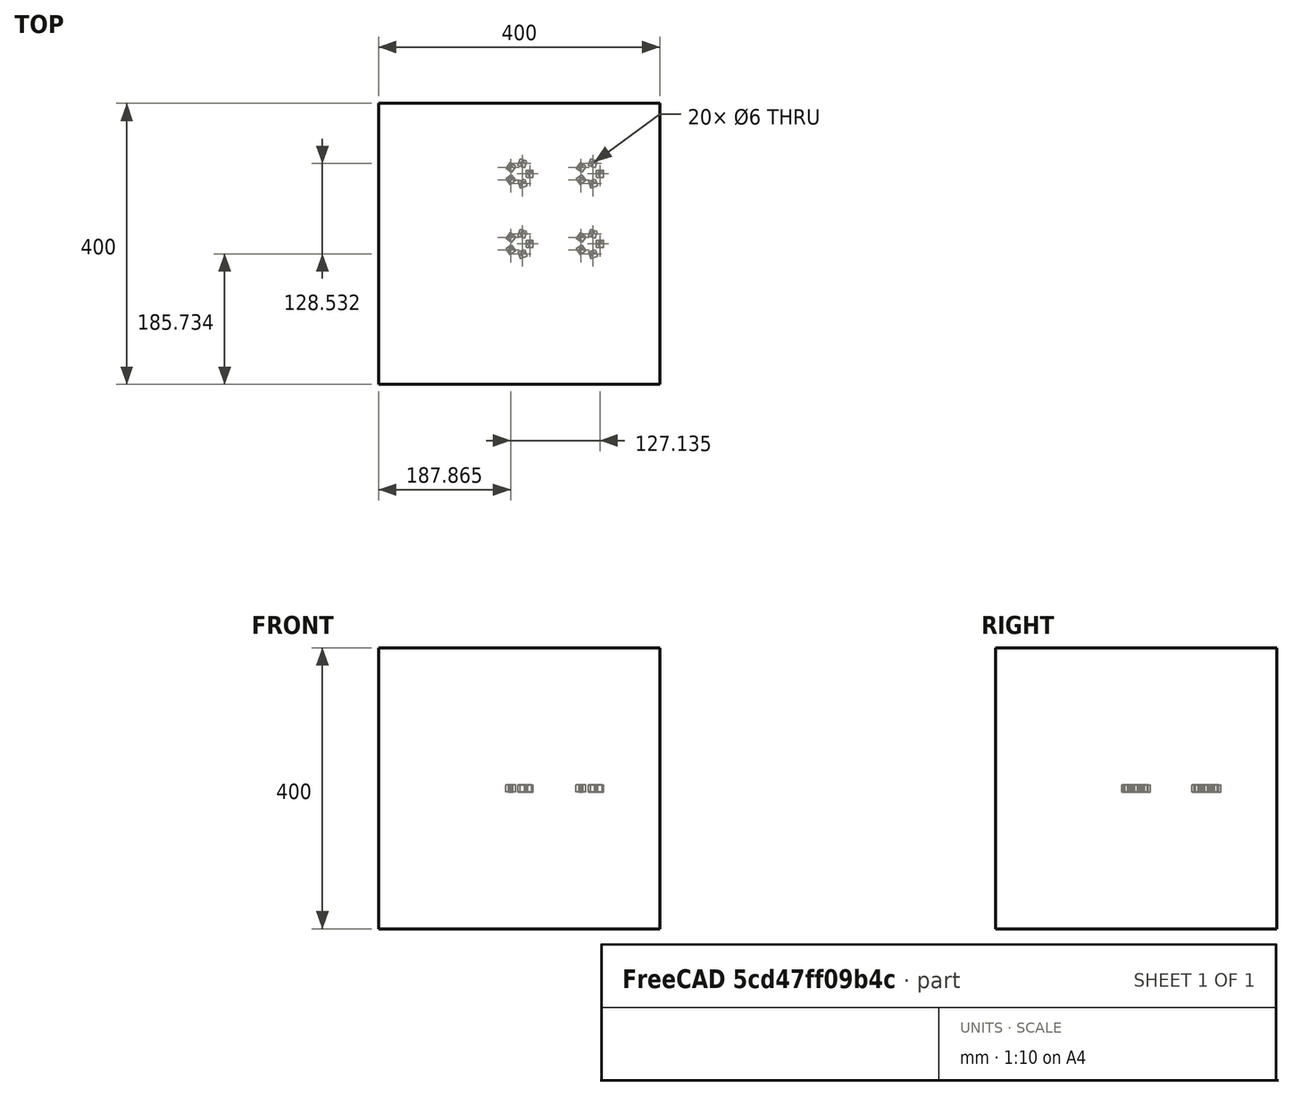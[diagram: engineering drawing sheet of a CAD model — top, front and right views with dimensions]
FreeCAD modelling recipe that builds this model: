
FCSTD DOCUMENT  (FreeCAD 0.19RUnknown)
Label: orthoArray_of_polarArray
License: All rights reserved
LicenseURL: http://en.wikipedia.org/wiki/All_rights_reserved
objects: App::DocumentObjectGroupPython×1248, Part::FeaturePython×5, App::Part×2, Part::Cut×1
note: 6 computed .brp shape members not serialized (recipe doc carries the construction recipe); baked Part::Feature solids carry a one-line shape summary decoded from their .brp

FEATURE [App::DocumentObjectGroupPython] HALFPI  # scripted group (container) (typed FeaturePython)
  name = HALFPI
  value = pi/2.
FEATURE [App::DocumentObjectGroupPython] PI  # scripted group (container) (typed FeaturePython)
  name = PI
  value = 1.*pi
FEATURE [App::DocumentObjectGroupPython] TWOPI  # scripted group (container) (typed FeaturePython)
  name = TWOPI
  value = 2.*pi
FEATURE [App::DocumentObjectGroupPython] Constants  # scripted group (container) (typed FeaturePython)
  Group = -> [HALFPI,PI,TWOPI]
FEATURE [App::DocumentObjectGroupPython] Variables  # scripted group (container) (typed FeaturePython)
FEATURE [App::DocumentObjectGroupPython] Quantities  # scripted group (container) (typed FeaturePython)
FEATURE [App::DocumentObjectGroupPython] Isotopes  # scripted group (container) (typed FeaturePython)
FEATURE [App::DocumentObjectGroupPython] Elements  # scripted group (container) (typed FeaturePython)
FEATURE [App::DocumentObjectGroupPython] G4Isotopes  # scripted group (container) (typed FeaturePython)
FEATURE [App::DocumentObjectGroupPython] H_element  # scripted group (container) (typed FeaturePython)
  Z = 1
  atom_value = 1.008
  formula = H
  name = H_element
FEATURE [App::DocumentObjectGroupPython] He_element  # scripted group (container) (typed FeaturePython)
  Z = 2
  atom_value = 4.0026
  formula = He
  name = He_element
FEATURE [App::DocumentObjectGroupPython] Li_element  # scripted group (container) (typed FeaturePython)
  Z = 3
  atom_value = 6.94
  formula = Li
  name = Li_element
FEATURE [App::DocumentObjectGroupPython] Be_element  # scripted group (container) (typed FeaturePython)
  Z = 4
  atom_value = 9.01218
  formula = Be
  name = Be_element
FEATURE [App::DocumentObjectGroupPython] B_element  # scripted group (container) (typed FeaturePython)
  Z = 5
  atom_value = 10.81
  formula = B
  name = B_element
FEATURE [App::DocumentObjectGroupPython] C_element  # scripted group (container) (typed FeaturePython)
  Z = 6
  atom_value = 12.011
  formula = C
  name = C_element
FEATURE [App::DocumentObjectGroupPython] N_element  # scripted group (container) (typed FeaturePython)
  Z = 7
  atom_value = 14.007
  formula = N
  name = N_element
FEATURE [App::DocumentObjectGroupPython] O_element  # scripted group (container) (typed FeaturePython)
  Z = 8
  atom_value = 15.999
  formula = O
  name = O_element
FEATURE [App::DocumentObjectGroupPython] F_element  # scripted group (container) (typed FeaturePython)
  Z = 9
  atom_value = 18.9984
  formula = F
  name = F_element
FEATURE [App::DocumentObjectGroupPython] Ne_element  # scripted group (container) (typed FeaturePython)
  Z = 10
  atom_value = 20.1797
  formula = Ne
  name = Ne_element
FEATURE [App::DocumentObjectGroupPython] Na_element  # scripted group (container) (typed FeaturePython)
  Z = 11
  atom_value = 22.9898
  formula = Na
  name = Na_element
FEATURE [App::DocumentObjectGroupPython] Mg_element  # scripted group (container) (typed FeaturePython)
  Z = 12
  atom_value = 24.305
  formula = Mg
  name = Mg_element
FEATURE [App::DocumentObjectGroupPython] Al_element  # scripted group (container) (typed FeaturePython)
  Z = 13
  atom_value = 26.9815
  formula = Al
  name = Al_element
FEATURE [App::DocumentObjectGroupPython] Si_element  # scripted group (container) (typed FeaturePython)
  Z = 14
  atom_value = 28.085
  formula = Si
  name = Si_element
FEATURE [App::DocumentObjectGroupPython] P_element  # scripted group (container) (typed FeaturePython)
  Z = 15
  atom_value = 30.9738
  formula = P
  name = P_element
FEATURE [App::DocumentObjectGroupPython] S_element  # scripted group (container) (typed FeaturePython)
  Z = 16
  atom_value = 32.06
  formula = S
  name = S_element
FEATURE [App::DocumentObjectGroupPython] Cl_element  # scripted group (container) (typed FeaturePython)
  Z = 17
  atom_value = 35.45
  formula = Cl
  name = Cl_element
FEATURE [App::DocumentObjectGroupPython] Ar_element  # scripted group (container) (typed FeaturePython)
  Z = 18
  atom_value = 39.95
  formula = Ar
  name = Ar_element
FEATURE [App::DocumentObjectGroupPython] K_element  # scripted group (container) (typed FeaturePython)
  Z = 19
  atom_value = 39.0983
  formula = K
  name = K_element
FEATURE [App::DocumentObjectGroupPython] Ca_element  # scripted group (container) (typed FeaturePython)
  Z = 20
  atom_value = 40.078
  formula = Ca
  name = Ca_element
FEATURE [App::DocumentObjectGroupPython] Sc_element  # scripted group (container) (typed FeaturePython)
  Z = 21
  atom_value = 44.9559
  formula = Sc
  name = Sc_element
FEATURE [App::DocumentObjectGroupPython] Ti_element  # scripted group (container) (typed FeaturePython)
  Z = 22
  atom_value = 47.867
  formula = Ti
  name = Ti_element
FEATURE [App::DocumentObjectGroupPython] V_element  # scripted group (container) (typed FeaturePython)
  Z = 23
  atom_value = 50.9415
  formula = V
  name = V_element
FEATURE [App::DocumentObjectGroupPython] Cr_element  # scripted group (container) (typed FeaturePython)
  Z = 24
  atom_value = 51.9961
  formula = Cr
  name = Cr_element
FEATURE [App::DocumentObjectGroupPython] Mn_element  # scripted group (container) (typed FeaturePython)
  Z = 25
  atom_value = 54.938
  formula = Mn
  name = Mn_element
FEATURE [App::DocumentObjectGroupPython] Fe_element  # scripted group (container) (typed FeaturePython)
  Z = 26
  atom_value = 55.845
  formula = Fe
  name = Fe_element
FEATURE [App::DocumentObjectGroupPython] Co_element  # scripted group (container) (typed FeaturePython)
  Z = 27
  atom_value = 58.9332
  formula = Co
  name = Co_element
FEATURE [App::DocumentObjectGroupPython] Ni_element  # scripted group (container) (typed FeaturePython)
  Z = 28
  atom_value = 58.6934
  formula = Ni
  name = Ni_element
FEATURE [App::DocumentObjectGroupPython] Cu_element  # scripted group (container) (typed FeaturePython)
  Z = 29
  atom_value = 63.546
  formula = Cu
  name = Cu_element
FEATURE [App::DocumentObjectGroupPython] Zn_element  # scripted group (container) (typed FeaturePython)
  Z = 30
  atom_value = 65.38
  formula = Zn
  name = Zn_element
FEATURE [App::DocumentObjectGroupPython] Ga_element  # scripted group (container) (typed FeaturePython)
  Z = 31
  atom_value = 69.723
  formula = Ga
  name = Ga_element
FEATURE [App::DocumentObjectGroupPython] Ge_element  # scripted group (container) (typed FeaturePython)
  Z = 32
  atom_value = 72.63
  formula = Ge
  name = Ge_element
FEATURE [App::DocumentObjectGroupPython] As_element  # scripted group (container) (typed FeaturePython)
  Z = 33
  atom_value = 74.9216
  formula = As
  name = As_element
FEATURE [App::DocumentObjectGroupPython] Se_element  # scripted group (container) (typed FeaturePython)
  Z = 34
  atom_value = 78.971
  formula = Se
  name = Se_element
FEATURE [App::DocumentObjectGroupPython] Br_element  # scripted group (container) (typed FeaturePython)
  Z = 35
  atom_value = 79.904
  formula = Br
  name = Br_element
FEATURE [App::DocumentObjectGroupPython] Kr_element  # scripted group (container) (typed FeaturePython)
  Z = 36
  atom_value = 83.798
  formula = Kr
  name = Kr_element
FEATURE [App::DocumentObjectGroupPython] Rb_element  # scripted group (container) (typed FeaturePython)
  Z = 37
  atom_value = 85.4678
  formula = Rb
  name = Rb_element
FEATURE [App::DocumentObjectGroupPython] Sr_element  # scripted group (container) (typed FeaturePython)
  Z = 38
  atom_value = 87.62
  formula = Sr
  name = Sr_element
FEATURE [App::DocumentObjectGroupPython] Y_element  # scripted group (container) (typed FeaturePython)
  Z = 39
  atom_value = 88.9058
  formula = Y
  name = Y_element
FEATURE [App::DocumentObjectGroupPython] Zr_element  # scripted group (container) (typed FeaturePython)
  Z = 40
  atom_value = 91.224
  formula = Zr
  name = Zr_element
FEATURE [App::DocumentObjectGroupPython] Nb_element  # scripted group (container) (typed FeaturePython)
  Z = 41
  atom_value = 92.9064
  formula = Nb
  name = Nb_element
FEATURE [App::DocumentObjectGroupPython] Mo_element  # scripted group (container) (typed FeaturePython)
  Z = 42
  atom_value = 95.95
  formula = Mo
  name = Mo_element
FEATURE [App::DocumentObjectGroupPython] Tc_element  # scripted group (container) (typed FeaturePython)
  Z = 43
  atom_value = 97
  formula = Tc
  name = Tc_element
FEATURE [App::DocumentObjectGroupPython] Ru_element  # scripted group (container) (typed FeaturePython)
  Z = 44
  atom_value = 101.07
  formula = Ru
  name = Ru_element
FEATURE [App::DocumentObjectGroupPython] Rh_element  # scripted group (container) (typed FeaturePython)
  Z = 45
  atom_value = 102.905
  formula = Rh
  name = Rh_element
FEATURE [App::DocumentObjectGroupPython] Pd_element  # scripted group (container) (typed FeaturePython)
  Z = 46
  atom_value = 106.42
  formula = Pd
  name = Pd_element
FEATURE [App::DocumentObjectGroupPython] Ag_element  # scripted group (container) (typed FeaturePython)
  Z = 47
  atom_value = 107.868
  formula = Ag
  name = Ag_element
FEATURE [App::DocumentObjectGroupPython] Cd_element  # scripted group (container) (typed FeaturePython)
  Z = 48
  atom_value = 112.414
  formula = Cd
  name = Cd_element
FEATURE [App::DocumentObjectGroupPython] In_element  # scripted group (container) (typed FeaturePython)
  Z = 49
  atom_value = 114.818
  formula = In
  name = In_element
FEATURE [App::DocumentObjectGroupPython] Sn_element  # scripted group (container) (typed FeaturePython)
  Z = 50
  atom_value = 118.71
  formula = Sn
  name = Sn_element
FEATURE [App::DocumentObjectGroupPython] Sb_element  # scripted group (container) (typed FeaturePython)
  Z = 51
  atom_value = 121.76
  formula = Sb
  name = Sb_element
FEATURE [App::DocumentObjectGroupPython] Te_element  # scripted group (container) (typed FeaturePython)
  Z = 52
  atom_value = 127.6
  formula = Te
  name = Te_element
FEATURE [App::DocumentObjectGroupPython] I_element  # scripted group (container) (typed FeaturePython)
  Z = 53
  atom_value = 126.904
  formula = I
  name = I_element
FEATURE [App::DocumentObjectGroupPython] Xe_element  # scripted group (container) (typed FeaturePython)
  Z = 54
  atom_value = 131.293
  formula = Xe
  name = Xe_element
FEATURE [App::DocumentObjectGroupPython] Cs_element  # scripted group (container) (typed FeaturePython)
  Z = 55
  atom_value = 132.905
  formula = Cs
  name = Cs_element
FEATURE [App::DocumentObjectGroupPython] Ba_element  # scripted group (container) (typed FeaturePython)
  Z = 56
  atom_value = 137.327
  formula = Ba
  name = Ba_element
FEATURE [App::DocumentObjectGroupPython] La_element  # scripted group (container) (typed FeaturePython)
  Z = 57
  atom_value = 138.905
  formula = La
  name = La_element
FEATURE [App::DocumentObjectGroupPython] Ce_element  # scripted group (container) (typed FeaturePython)
  Z = 58
  atom_value = 140.116
  formula = Ce
  name = Ce_element
FEATURE [App::DocumentObjectGroupPython] Pr_element  # scripted group (container) (typed FeaturePython)
  Z = 59
  atom_value = 140.908
  formula = Pr
  name = Pr_element
FEATURE [App::DocumentObjectGroupPython] Nd_element  # scripted group (container) (typed FeaturePython)
  Z = 60
  atom_value = 144.242
  formula = Nd
  name = Nd_element
FEATURE [App::DocumentObjectGroupPython] Pm_element  # scripted group (container) (typed FeaturePython)
  Z = 61
  atom_value = 145
  formula = Pm
  name = Pm_element
FEATURE [App::DocumentObjectGroupPython] Sm_element  # scripted group (container) (typed FeaturePython)
  Z = 62
  atom_value = 150.36
  formula = Sm
  name = Sm_element
FEATURE [App::DocumentObjectGroupPython] Eu_element  # scripted group (container) (typed FeaturePython)
  Z = 63
  atom_value = 151.964
  formula = Eu
  name = Eu_element
FEATURE [App::DocumentObjectGroupPython] Gd_element  # scripted group (container) (typed FeaturePython)
  Z = 64
  atom_value = 157.25
  formula = Gd
  name = Gd_element
FEATURE [App::DocumentObjectGroupPython] Tb_element  # scripted group (container) (typed FeaturePython)
  Z = 65
  atom_value = 158.925
  formula = Tb
  name = Tb_element
FEATURE [App::DocumentObjectGroupPython] Dy_element  # scripted group (container) (typed FeaturePython)
  Z = 66
  atom_value = 162.5
  formula = Dy
  name = Dy_element
FEATURE [App::DocumentObjectGroupPython] Ho_element  # scripted group (container) (typed FeaturePython)
  Z = 67
  atom_value = 164.93
  formula = Ho
  name = Ho_element
FEATURE [App::DocumentObjectGroupPython] Er_element  # scripted group (container) (typed FeaturePython)
  Z = 68
  atom_value = 167.259
  formula = Er
  name = Er_element
FEATURE [App::DocumentObjectGroupPython] Tm_element  # scripted group (container) (typed FeaturePython)
  Z = 69
  atom_value = 168.934
  formula = Tm
  name = Tm_element
FEATURE [App::DocumentObjectGroupPython] Yb_element  # scripted group (container) (typed FeaturePython)
  Z = 70
  atom_value = 173.045
  formula = Yb
  name = Yb_element
FEATURE [App::DocumentObjectGroupPython] Lu_element  # scripted group (container) (typed FeaturePython)
  Z = 71
  atom_value = 174.967
  formula = Lu
  name = Lu_element
FEATURE [App::DocumentObjectGroupPython] Hf_element  # scripted group (container) (typed FeaturePython)
  Z = 72
  atom_value = 178.49
  formula = Hf
  name = Hf_element
FEATURE [App::DocumentObjectGroupPython] Ta_element  # scripted group (container) (typed FeaturePython)
  Z = 73
  atom_value = 180.948
  formula = Ta
  name = Ta_element
FEATURE [App::DocumentObjectGroupPython] W_element  # scripted group (container) (typed FeaturePython)
  Z = 74
  atom_value = 183.84
  formula = W
  name = W_element
FEATURE [App::DocumentObjectGroupPython] Re_element  # scripted group (container) (typed FeaturePython)
  Z = 75
  atom_value = 186.207
  formula = Re
  name = Re_element
FEATURE [App::DocumentObjectGroupPython] Os_element  # scripted group (container) (typed FeaturePython)
  Z = 76
  atom_value = 190.23
  formula = Os
  name = Os_element
FEATURE [App::DocumentObjectGroupPython] Ir_element  # scripted group (container) (typed FeaturePython)
  Z = 77
  atom_value = 192.217
  formula = Ir
  name = Ir_element
FEATURE [App::DocumentObjectGroupPython] Pt_element  # scripted group (container) (typed FeaturePython)
  Z = 78
  atom_value = 195.084
  formula = Pt
  name = Pt_element
FEATURE [App::DocumentObjectGroupPython] Au_element  # scripted group (container) (typed FeaturePython)
  Z = 79
  atom_value = 196.967
  formula = Au
  name = Au_element
FEATURE [App::DocumentObjectGroupPython] Hg_element  # scripted group (container) (typed FeaturePython)
  Z = 80
  atom_value = 200.592
  formula = Hg
  name = Hg_element
FEATURE [App::DocumentObjectGroupPython] Tl_element  # scripted group (container) (typed FeaturePython)
  Z = 81
  atom_value = 204.38
  formula = Tl
  name = Tl_element
FEATURE [App::DocumentObjectGroupPython] Pb_element  # scripted group (container) (typed FeaturePython)
  Z = 82
  atom_value = 207.2
  formula = Pb
  name = Pb_element
FEATURE [App::DocumentObjectGroupPython] Bi_element  # scripted group (container) (typed FeaturePython)
  Z = 83
  atom_value = 208.98
  formula = Bi
  name = Bi_element
FEATURE [App::DocumentObjectGroupPython] Po_element  # scripted group (container) (typed FeaturePython)
  Z = 84
  atom_value = 209
  formula = Po
  name = Po_element
FEATURE [App::DocumentObjectGroupPython] At_element  # scripted group (container) (typed FeaturePython)
  Z = 85
  atom_value = 210
  formula = At
  name = At_element
FEATURE [App::DocumentObjectGroupPython] Rn_element  # scripted group (container) (typed FeaturePython)
  Z = 86
  atom_value = 222
  formula = Rn
  name = Rn_element
FEATURE [App::DocumentObjectGroupPython] Fr_element  # scripted group (container) (typed FeaturePython)
  Z = 87
  atom_value = 223
  formula = Fr
  name = Fr_element
FEATURE [App::DocumentObjectGroupPython] Ra_element  # scripted group (container) (typed FeaturePython)
  Z = 88
  atom_value = 226
  formula = Ra
  name = Ra_element
FEATURE [App::DocumentObjectGroupPython] Ac_element  # scripted group (container) (typed FeaturePython)
  Z = 89
  atom_value = 227
  formula = Ac
  name = Ac_element
FEATURE [App::DocumentObjectGroupPython] Th_element  # scripted group (container) (typed FeaturePython)
  Z = 90
  atom_value = 232.038
  formula = Th
  name = Th_element
FEATURE [App::DocumentObjectGroupPython] Pa_element  # scripted group (container) (typed FeaturePython)
  Z = 91
  atom_value = 231.036
  formula = Pa
  name = Pa_element
FEATURE [App::DocumentObjectGroupPython] U_element  # scripted group (container) (typed FeaturePython)
  Z = 92
  atom_value = 238.029
  formula = U
  name = U_element
FEATURE [App::DocumentObjectGroupPython] Np_element  # scripted group (container) (typed FeaturePython)
  Z = 93
  atom_value = 237
  formula = Np
  name = Np_element
FEATURE [App::DocumentObjectGroupPython] Pu_element  # scripted group (container) (typed FeaturePython)
  Z = 94
  atom_value = 244
  formula = Pu
  name = Pu_element
FEATURE [App::DocumentObjectGroupPython] Am_element  # scripted group (container) (typed FeaturePython)
  Z = 95
  atom_value = 243
  formula = Am
  name = Am_element
FEATURE [App::DocumentObjectGroupPython] Cm_element  # scripted group (container) (typed FeaturePython)
  Z = 96
  atom_value = 247
  formula = Cm
  name = Cm_element
FEATURE [App::DocumentObjectGroupPython] Bk_element  # scripted group (container) (typed FeaturePython)
  Z = 97
  atom_value = 247
  formula = Bk
  name = Bk_element
FEATURE [App::DocumentObjectGroupPython] Cf_element  # scripted group (container) (typed FeaturePython)
  Z = 98
  atom_value = 251
  formula = Cf
  name = Cf_element
FEATURE [App::DocumentObjectGroupPython] G4Elements  # scripted group (container) (typed FeaturePython)
  Group = -> [H_element,He_element,Li_element,Be_element,B_element,C_element,N_element,O_element,F_element,Ne_element,Na_element,Mg_element,Al_element,Si_element,P_element,S_element,Cl_element,Ar_element,K_element,Ca_element,Sc_element,Ti_element,V_element,Cr_element,Mn_element,Fe_element,Co_element,Ni_element,Cu_element,Zn_element,Ga_element,Ge_element,As_element,Se_element,Br_element,Kr_element,Rb_element,+61 more]
FEATURE [App::DocumentObjectGroupPython] H_element001  label="H_element : 0.101"  # scripted group (container) (typed FeaturePython)
  n = 0.101327
FEATURE [App::DocumentObjectGroupPython] C_element001  label="C_element : 0.775"  # scripted group (container) (typed FeaturePython)
  n = 0.7755
FEATURE [App::DocumentObjectGroupPython] N_element001  label="N_element : 0.035"  # scripted group (container) (typed FeaturePython)
  n = 0.035057
FEATURE [App::DocumentObjectGroupPython] O_element001  label="O_element : 0.052"  # scripted group (container) (typed FeaturePython)
  n = 0.0523159
FEATURE [App::DocumentObjectGroupPython] F_element001  label="F_element : 0.017"  # scripted group (container) (typed FeaturePython)
  n = 0.017422
FEATURE [App::DocumentObjectGroupPython] Ca_element001  label="Ca_element : 0.018"  # scripted group (container) (typed FeaturePython)
  n = 0.018378
FEATURE [App::DocumentObjectGroupPython] G4_A_150_TISSUE  label="G4_A-150_TISSUE"  # scripted group (container) (typed FeaturePython)
  Dunit = g/cm3
  Dvalue = 1.127
  Group = -> [H_element001,C_element001,N_element001,O_element001,F_element001,Ca_element001]
  conduct = 2
  density = 1
  expand = 3
  formula = G4_A-150_TISSUE
  name = G4_A-150_TISSUE
  specific = 4
FEATURE [App::DocumentObjectGroupPython] C_element002  label="C_element : 3"  # scripted group (container) (typed FeaturePython)
  n = 3
  ref = C_element
FEATURE [App::DocumentObjectGroupPython] H_element002  label="H_element : 6"  # scripted group (container) (typed FeaturePython)
  n = 6
  ref = H_element
FEATURE [App::DocumentObjectGroupPython] O_element002  label="O_element : 1"  # scripted group (container) (typed FeaturePython)
  n = 1
  ref = O_element
FEATURE [App::DocumentObjectGroupPython] G4_ACETONE  # scripted group (container) (typed FeaturePython)
  Dunit = g/cm3
  Dvalue = 0.7899
  Group = -> [C_element002,H_element002,O_element002]
  conduct = 2
  density = 1
  expand = 3
  formula = G4_ACETONE
  name = G4_ACETONE
  specific = 4
FEATURE [App::DocumentObjectGroupPython] C_element003  label="C_element : 2"  # scripted group (container) (typed FeaturePython)
  n = 2
  ref = C_element
FEATURE [App::DocumentObjectGroupPython] H_element003  label="H_element : 2"  # scripted group (container) (typed FeaturePython)
  n = 2
  ref = H_element
FEATURE [App::DocumentObjectGroupPython] G4_ACETYLENE  # scripted group (container) (typed FeaturePython)
  Dunit = g/cm3
  Dvalue = 0.0010967
  Group = -> [C_element003,H_element003]
  conduct = 2
  density = 1
  expand = 3
  formula = G4_ACETYLENE
  name = G4_ACETYLENE
  specific = 4
FEATURE [App::DocumentObjectGroupPython] C_element004  label="C_element : 5"  # scripted group (container) (typed FeaturePython)
  n = 5
  ref = C_element
FEATURE [App::DocumentObjectGroupPython] H_element004  label="H_element : 5"  # scripted group (container) (typed FeaturePython)
  n = 5
  ref = H_element
FEATURE [App::DocumentObjectGroupPython] N_element002  label="N_element : 5"  # scripted group (container) (typed FeaturePython)
  n = 5
  ref = N_element
FEATURE [App::DocumentObjectGroupPython] G4_ADENINE  # scripted group (container) (typed FeaturePython)
  Dunit = g/cm3
  Dvalue = 1.6
  Group = -> [C_element004,H_element004,N_element002]
  conduct = 2
  density = 1
  expand = 3
  formula = G4_ADENINE
  name = G4_ADENINE
  specific = 4
FEATURE [App::DocumentObjectGroupPython] H_element005  label="H_element : 0.114"  # scripted group (container) (typed FeaturePython)
  n = 0.114
FEATURE [App::DocumentObjectGroupPython] C_element005  label="C_element : 0.598"  # scripted group (container) (typed FeaturePython)
  n = 0.598
FEATURE [App::DocumentObjectGroupPython] N_element003  label="N_element : 0.007"  # scripted group (container) (typed FeaturePython)
  n = 0.007
FEATURE [App::DocumentObjectGroupPython] O_element003  label="O_element : 0.278"  # scripted group (container) (typed FeaturePython)
  n = 0.278
FEATURE [App::DocumentObjectGroupPython] Na_element001  label="Na_element : 0.001"  # scripted group (container) (typed FeaturePython)
  n = 0.001
FEATURE [App::DocumentObjectGroupPython] S_element001  label="S_element : 0.001"  # scripted group (container) (typed FeaturePython)
  n = 0.001
FEATURE [App::DocumentObjectGroupPython] Cl_element001  label="Cl_element : 0.001"  # scripted group (container) (typed FeaturePython)
  n = 0.001
FEATURE [App::DocumentObjectGroupPython] G4_ADIPOSE_TISSUE_ICRP  # scripted group (container) (typed FeaturePython)
  Dunit = g/cm3
  Dvalue = 0.95
  Group = -> [H_element005,C_element005,N_element003,O_element003,Na_element001,S_element001,Cl_element001]
  conduct = 2
  density = 1
  expand = 3
  formula = G4_ADIPOSE_TISSUE_ICRP
  name = G4_ADIPOSE_TISSUE_ICRP
  specific = 4
FEATURE [App::DocumentObjectGroupPython] C_element006  label="C_element : 0.000"  # scripted group (container) (typed FeaturePython)
  n = 0.000124
FEATURE [App::DocumentObjectGroupPython] N_element004  label="N_element : 0.755"  # scripted group (container) (typed FeaturePython)
  n = 0.755268
FEATURE [App::DocumentObjectGroupPython] O_element004  label="O_element : 0.232"  # scripted group (container) (typed FeaturePython)
  n = 0.231781
FEATURE [App::DocumentObjectGroupPython] Ar_element001  label="Ar_element : 0.013"  # scripted group (container) (typed FeaturePython)
  n = 0.012827
FEATURE [App::DocumentObjectGroupPython] G4_AIR  # scripted group (container) (typed FeaturePython)
  Dunit = g/cm3
  Dvalue = 0.00120479
  Group = -> [C_element006,N_element004,O_element004,Ar_element001]
  conduct = 2
  density = 1
  expand = 3
  formula = G4_AIR
  name = G4_AIR
  specific = 4
FEATURE [App::DocumentObjectGroupPython] C_element007  label="C_element : 006"  # scripted group (container) (typed FeaturePython)
  n = 3
  ref = C_element
FEATURE [App::DocumentObjectGroupPython] H_element006  label="H_element : 7"  # scripted group (container) (typed FeaturePython)
  n = 7
  ref = H_element
FEATURE [App::DocumentObjectGroupPython] N_element005  label="N_element : 1"  # scripted group (container) (typed FeaturePython)
  n = 1
  ref = N_element
FEATURE [App::DocumentObjectGroupPython] O_element005  label="O_element : 2"  # scripted group (container) (typed FeaturePython)
  n = 2
  ref = O_element
FEATURE [App::DocumentObjectGroupPython] G4_ALANINE  # scripted group (container) (typed FeaturePython)
  Dunit = g/cm3
  Dvalue = 1.42
  Group = -> [C_element007,H_element006,N_element005,O_element005]
  conduct = 2
  density = 1
  expand = 3
  formula = G4_ALANINE
  name = G4_ALANINE
  specific = 4
FEATURE [App::DocumentObjectGroupPython] Al_element001  label="Al_element : 2"  # scripted group (container) (typed FeaturePython)
  n = 2
  ref = Al_element
FEATURE [App::DocumentObjectGroupPython] O_element006  label="O_element : 3"  # scripted group (container) (typed FeaturePython)
  n = 3
  ref = O_element
FEATURE [App::DocumentObjectGroupPython] G4_ALUMINUM_OXIDE  # scripted group (container) (typed FeaturePython)
  Dunit = g/cm3
  Dvalue = 3.97
  Group = -> [Al_element001,O_element006]
  conduct = 2
  density = 1
  expand = 3
  formula = G4_ALUMINUM_OXIDE
  name = G4_ALUMINUM_OXIDE
  specific = 4
FEATURE [App::DocumentObjectGroupPython] H_element007  label="H_element : 0.106"  # scripted group (container) (typed FeaturePython)
  n = 0.10593
FEATURE [App::DocumentObjectGroupPython] C_element008  label="C_element : 0.789"  # scripted group (container) (typed FeaturePython)
  n = 0.788974
FEATURE [App::DocumentObjectGroupPython] O_element007  label="O_element : 0.105"  # scripted group (container) (typed FeaturePython)
  n = 0.105096
FEATURE [App::DocumentObjectGroupPython] G4_AMBER  # scripted group (container) (typed FeaturePython)
  Dunit = g/cm3
  Dvalue = 1.1
  Group = -> [H_element007,C_element008,O_element007]
  conduct = 2
  density = 1
  expand = 3
  formula = G4_AMBER
  name = G4_AMBER
  specific = 4
FEATURE [App::DocumentObjectGroupPython] N_element006  label="N_element : 006"  # scripted group (container) (typed FeaturePython)
  n = 1
  ref = N_element
FEATURE [App::DocumentObjectGroupPython] H_element008  label="H_element : 3"  # scripted group (container) (typed FeaturePython)
  n = 3
  ref = H_element
FEATURE [App::DocumentObjectGroupPython] G4_AMMONIA  # scripted group (container) (typed FeaturePython)
  Dunit = g/cm3
  Dvalue = 0.000826019
  Group = -> [N_element006,H_element008]
  conduct = 2
  density = 1
  expand = 3
  formula = G4_AMMONIA
  name = G4_AMMONIA
  specific = 4
FEATURE [App::DocumentObjectGroupPython] C_element009  label="C_element : 6"  # scripted group (container) (typed FeaturePython)
  n = 6
  ref = C_element
FEATURE [App::DocumentObjectGroupPython] H_element009  label="H_element : 008"  # scripted group (container) (typed FeaturePython)
  n = 7
  ref = H_element
FEATURE [App::DocumentObjectGroupPython] N_element007  label="N_element : 007"  # scripted group (container) (typed FeaturePython)
  n = 1
  ref = N_element
FEATURE [App::DocumentObjectGroupPython] G4_ANILINE  # scripted group (container) (typed FeaturePython)
  Dunit = g/cm3
  Dvalue = 1.0235
  Group = -> [C_element009,H_element009,N_element007]
  conduct = 2
  density = 1
  expand = 3
  formula = G4_ANILINE
  name = G4_ANILINE
  specific = 4
FEATURE [App::DocumentObjectGroupPython] C_element010  label="C_element : 14"  # scripted group (container) (typed FeaturePython)
  n = 14
  ref = C_element
FEATURE [App::DocumentObjectGroupPython] H_element010  label="H_element : 10"  # scripted group (container) (typed FeaturePython)
  n = 10
  ref = H_element
FEATURE [App::DocumentObjectGroupPython] G4_ANTHRACENE  # scripted group (container) (typed FeaturePython)
  Dunit = g/cm3
  Dvalue = 1.283
  Group = -> [C_element010,H_element010]
  conduct = 2
  density = 1
  expand = 3
  formula = G4_ANTHRACENE
  name = G4_ANTHRACENE
  specific = 4
FEATURE [App::DocumentObjectGroupPython] H_element011  label="H_element : 0.065"  # scripted group (container) (typed FeaturePython)
  n = 0.0654709
FEATURE [App::DocumentObjectGroupPython] C_element011  label="C_element : 0.537"  # scripted group (container) (typed FeaturePython)
  n = 0.536944
FEATURE [App::DocumentObjectGroupPython] N_element008  label="N_element : 0.021"  # scripted group (container) (typed FeaturePython)
  n = 0.0215
FEATURE [App::DocumentObjectGroupPython] O_element008  label="O_element : 0.032"  # scripted group (container) (typed FeaturePython)
  n = 0.032085
FEATURE [App::DocumentObjectGroupPython] F_element002  label="F_element : 0.167"  # scripted group (container) (typed FeaturePython)
  n = 0.167411
FEATURE [App::DocumentObjectGroupPython] Ca_element002  label="Ca_element : 0.177"  # scripted group (container) (typed FeaturePython)
  n = 0.176589
FEATURE [App::DocumentObjectGroupPython] G4_B_100_BONE  label="G4_B-100_BONE"  # scripted group (container) (typed FeaturePython)
  Dunit = g/cm3
  Dvalue = 1.45
  Group = -> [H_element011,C_element011,N_element008,O_element008,F_element002,Ca_element002]
  conduct = 2
  density = 1
  expand = 3
  formula = G4_B-100_BONE
  name = G4_B-100_BONE
  specific = 4
FEATURE [App::DocumentObjectGroupPython] H_element012  label="H_element : 0.057"  # scripted group (container) (typed FeaturePython)
  n = 0.057441
FEATURE [App::DocumentObjectGroupPython] C_element012  label="C_element : 0.790"  # scripted group (container) (typed FeaturePython)
  n = 0.774591
FEATURE [App::DocumentObjectGroupPython] O_element009  label="O_element : 0.168"  # scripted group (container) (typed FeaturePython)
  n = 0.167968
FEATURE [App::DocumentObjectGroupPython] G4_BAKELITE  # scripted group (container) (typed FeaturePython)
  Dunit = g/cm3
  Dvalue = 1.25
  Group = -> [H_element012,C_element012,O_element009]
  conduct = 2
  density = 1
  expand = 3
  formula = G4_BAKELITE
  name = G4_BAKELITE
  specific = 4
FEATURE [App::DocumentObjectGroupPython] Ba_element001  label="Ba_element : 1"  # scripted group (container) (typed FeaturePython)
  n = 1
  ref = Ba_element
FEATURE [App::DocumentObjectGroupPython] F_element003  label="F_element : 2"  # scripted group (container) (typed FeaturePython)
  n = 2
  ref = F_element
FEATURE [App::DocumentObjectGroupPython] G4_BARIUM_FLUORIDE  # scripted group (container) (typed FeaturePython)
  Dunit = g/cm3
  Dvalue = 4.89
  Group = -> [Ba_element001,F_element003]
  conduct = 2
  density = 1
  expand = 3
  formula = G4_BARIUM_FLUORIDE
  name = G4_BARIUM_FLUORIDE
  specific = 4
FEATURE [App::DocumentObjectGroupPython] Ba_element002  label="Ba_element : 002"  # scripted group (container) (typed FeaturePython)
  n = 1
  ref = Ba_element
FEATURE [App::DocumentObjectGroupPython] S_element002  label="S_element : 1"  # scripted group (container) (typed FeaturePython)
  n = 1
  ref = S_element
FEATURE [App::DocumentObjectGroupPython] O_element010  label="O_element : 4"  # scripted group (container) (typed FeaturePython)
  n = 4
  ref = O_element
FEATURE [App::DocumentObjectGroupPython] G4_BARIUM_SULFATE  # scripted group (container) (typed FeaturePython)
  Dunit = g/cm3
  Dvalue = 4.5
  Group = -> [Ba_element002,S_element002,O_element010]
  conduct = 2
  density = 1
  expand = 3
  formula = G4_BARIUM_SULFATE
  name = G4_BARIUM_SULFATE
  specific = 4
FEATURE [App::DocumentObjectGroupPython] C_element013  label="C_element : 007"  # scripted group (container) (typed FeaturePython)
  n = 6
  ref = C_element
FEATURE [App::DocumentObjectGroupPython] H_element013  label="H_element : 009"  # scripted group (container) (typed FeaturePython)
  n = 6
  ref = H_element
FEATURE [App::DocumentObjectGroupPython] G4_BENZENE  # scripted group (container) (typed FeaturePython)
  Dunit = g/cm3
  Dvalue = 0.87865
  Group = -> [C_element013,H_element013]
  conduct = 2
  density = 1
  expand = 3
  formula = G4_BENZENE
  name = G4_BENZENE
  specific = 4
FEATURE [App::DocumentObjectGroupPython] Be_element001  label="Be_element : 1"  # scripted group (container) (typed FeaturePython)
  n = 1
  ref = Be_element
FEATURE [App::DocumentObjectGroupPython] O_element011  label="O_element : 005"  # scripted group (container) (typed FeaturePython)
  n = 1
  ref = O_element
FEATURE [App::DocumentObjectGroupPython] G4_BERYLLIUM_OXIDE  # scripted group (container) (typed FeaturePython)
  Dunit = g/cm3
  Dvalue = 3.01
  Group = -> [Be_element001,O_element011]
  conduct = 2
  density = 1
  expand = 3
  formula = G4_BERYLLIUM_OXIDE
  name = G4_BERYLLIUM_OXIDE
  specific = 4
FEATURE [App::DocumentObjectGroupPython] Bi_element001  label="Bi_element : 4"  # scripted group (container) (typed FeaturePython)
  n = 4
  ref = Bi_element
FEATURE [App::DocumentObjectGroupPython] Ge_element001  label="Ge_element : 3"  # scripted group (container) (typed FeaturePython)
  n = 3
  ref = Ge_element
FEATURE [App::DocumentObjectGroupPython] O_element012  label="O_element : 12"  # scripted group (container) (typed FeaturePython)
  n = 12
  ref = O_element
FEATURE [App::DocumentObjectGroupPython] G4_BGO  # scripted group (container) (typed FeaturePython)
  Dunit = g/cm3
  Dvalue = 7.13
  Group = -> [Bi_element001,Ge_element001,O_element012]
  conduct = 2
  density = 1
  expand = 3
  formula = G4_BGO
  name = G4_BGO
  specific = 4
FEATURE [App::DocumentObjectGroupPython] H_element014  label="H_element : 0.102"  # scripted group (container) (typed FeaturePython)
  n = 0.102
FEATURE [App::DocumentObjectGroupPython] C_element014  label="C_element : 0.110"  # scripted group (container) (typed FeaturePython)
  n = 0.11
FEATURE [App::DocumentObjectGroupPython] N_element009  label="N_element : 0.033"  # scripted group (container) (typed FeaturePython)
  n = 0.033
FEATURE [App::DocumentObjectGroupPython] O_element013  label="O_element : 0.745"  # scripted group (container) (typed FeaturePython)
  n = 0.745
FEATURE [App::DocumentObjectGroupPython] Na_element002  label="Na_element : 0.002"  # scripted group (container) (typed FeaturePython)
  n = 0.001
FEATURE [App::DocumentObjectGroupPython] P_element001  label="P_element : 0.001"  # scripted group (container) (typed FeaturePython)
  n = 0.001
FEATURE [App::DocumentObjectGroupPython] S_element003  label="S_element : 0.002"  # scripted group (container) (typed FeaturePython)
  n = 0.002
FEATURE [App::DocumentObjectGroupPython] Cl_element002  label="Cl_element : 0.003"  # scripted group (container) (typed FeaturePython)
  n = 0.003
FEATURE [App::DocumentObjectGroupPython] K_element001  label="K_element : 0.002"  # scripted group (container) (typed FeaturePython)
  n = 0.002
FEATURE [App::DocumentObjectGroupPython] Fe_element001  label="Fe_element : 0.001"  # scripted group (container) (typed FeaturePython)
  n = 0.001
FEATURE [App::DocumentObjectGroupPython] G4_BLOOD_ICRP  # scripted group (container) (typed FeaturePython)
  Dunit = g/cm3
  Dvalue = 1.06
  Group = -> [H_element014,C_element014,N_element009,O_element013,Na_element002,P_element001,S_element003,Cl_element002,K_element001,Fe_element001]
  conduct = 2
  density = 1
  expand = 3
  formula = G4_BLOOD_ICRP
  name = G4_BLOOD_ICRP
  specific = 4
FEATURE [App::DocumentObjectGroupPython] H_element015  label="H_element : 0.064"  # scripted group (container) (typed FeaturePython)
  n = 0.064
FEATURE [App::DocumentObjectGroupPython] C_element015  label="C_element : 0.278"  # scripted group (container) (typed FeaturePython)
  n = 0.278
FEATURE [App::DocumentObjectGroupPython] N_element010  label="N_element : 0.027"  # scripted group (container) (typed FeaturePython)
  n = 0.027
FEATURE [App::DocumentObjectGroupPython] O_element014  label="O_element : 0.410"  # scripted group (container) (typed FeaturePython)
  n = 0.41
FEATURE [App::DocumentObjectGroupPython] Mg_element001  label="Mg_element : 0.002"  # scripted group (container) (typed FeaturePython)
  n = 0.002
FEATURE [App::DocumentObjectGroupPython] P_element002  label="P_element : 0.070"  # scripted group (container) (typed FeaturePython)
  n = 0.07
FEATURE [App::DocumentObjectGroupPython] S_element004  label="S_element : 0.003"  # scripted group (container) (typed FeaturePython)
  n = 0.002
FEATURE [App::DocumentObjectGroupPython] Ca_element003  label="Ca_element : 0.147"  # scripted group (container) (typed FeaturePython)
  n = 0.147
FEATURE [App::DocumentObjectGroupPython] G4_BONE_COMPACT_ICRU  # scripted group (container) (typed FeaturePython)
  Dunit = g/cm3
  Dvalue = 1.85
  Group = -> [H_element015,C_element015,N_element010,O_element014,Mg_element001,P_element002,S_element004,Ca_element003]
  conduct = 2
  density = 1
  expand = 3
  formula = G4_BONE_COMPACT_ICRU
  name = G4_BONE_COMPACT_ICRU
  specific = 4
FEATURE [App::DocumentObjectGroupPython] H_element016  label="H_element : 0.034"  # scripted group (container) (typed FeaturePython)
  n = 0.034
FEATURE [App::DocumentObjectGroupPython] C_element016  label="C_element : 0.155"  # scripted group (container) (typed FeaturePython)
  n = 0.155
FEATURE [App::DocumentObjectGroupPython] N_element011  label="N_element : 0.042"  # scripted group (container) (typed FeaturePython)
  n = 0.042
FEATURE [App::DocumentObjectGroupPython] O_element015  label="O_element : 0.435"  # scripted group (container) (typed FeaturePython)
  n = 0.435
FEATURE [App::DocumentObjectGroupPython] Na_element003  label="Na_element : 0.003"  # scripted group (container) (typed FeaturePython)
  n = 0.001
FEATURE [App::DocumentObjectGroupPython] Mg_element002  label="Mg_element : 0.003"  # scripted group (container) (typed FeaturePython)
  n = 0.002
FEATURE [App::DocumentObjectGroupPython] P_element003  label="P_element : 0.103"  # scripted group (container) (typed FeaturePython)
  n = 0.103
FEATURE [App::DocumentObjectGroupPython] S_element005  label="S_element : 0.004"  # scripted group (container) (typed FeaturePython)
  n = 0.003
FEATURE [App::DocumentObjectGroupPython] Ca_element004  label="Ca_element : 0.225"  # scripted group (container) (typed FeaturePython)
  n = 0.225
FEATURE [App::DocumentObjectGroupPython] G4_BONE_CORTICAL_ICRP  # scripted group (container) (typed FeaturePython)
  Dunit = g/cm3
  Dvalue = 1.92
  Group = -> [H_element016,C_element016,N_element011,O_element015,Na_element003,Mg_element002,P_element003,S_element005,Ca_element004]
  conduct = 2
  density = 1
  expand = 3
  formula = G4_BONE_CORTICAL_ICRP
  name = G4_BONE_CORTICAL_ICRP
  specific = 4
FEATURE [App::DocumentObjectGroupPython] B_element001  label="B_element : 4"  # scripted group (container) (typed FeaturePython)
  n = 4
  ref = B_element
FEATURE [App::DocumentObjectGroupPython] C_element017  label="C_element : 1"  # scripted group (container) (typed FeaturePython)
  n = 1
  ref = C_element
FEATURE [App::DocumentObjectGroupPython] G4_BORON_CARBIDE  # scripted group (container) (typed FeaturePython)
  Dunit = g/cm3
  Dvalue = 2.52
  Group = -> [B_element001,C_element017]
  conduct = 2
  density = 1
  expand = 3
  formula = G4_BORON_CARBIDE
  name = G4_BORON_CARBIDE
  specific = 4
FEATURE [App::DocumentObjectGroupPython] B_element002  label="B_element : 2"  # scripted group (container) (typed FeaturePython)
  n = 2
  ref = B_element
FEATURE [App::DocumentObjectGroupPython] O_element016  label="O_element : 006"  # scripted group (container) (typed FeaturePython)
  n = 3
  ref = O_element
FEATURE [App::DocumentObjectGroupPython] G4_BORON_OXIDE  # scripted group (container) (typed FeaturePython)
  Dunit = g/cm3
  Dvalue = 1.812
  Group = -> [B_element002,O_element016]
  conduct = 2
  density = 1
  expand = 3
  formula = G4_BORON_OXIDE
  name = G4_BORON_OXIDE
  specific = 4
FEATURE [App::DocumentObjectGroupPython] H_element017  label="H_element : 0.107"  # scripted group (container) (typed FeaturePython)
  n = 0.107
FEATURE [App::DocumentObjectGroupPython] C_element018  label="C_element : 0.145"  # scripted group (container) (typed FeaturePython)
  n = 0.145
FEATURE [App::DocumentObjectGroupPython] N_element012  label="N_element : 0.022"  # scripted group (container) (typed FeaturePython)
  n = 0.022
FEATURE [App::DocumentObjectGroupPython] O_element017  label="O_element : 0.712"  # scripted group (container) (typed FeaturePython)
  n = 0.712
FEATURE [App::DocumentObjectGroupPython] Na_element004  label="Na_element : 0.004"  # scripted group (container) (typed FeaturePython)
  n = 0.002
FEATURE [App::DocumentObjectGroupPython] P_element004  label="P_element : 0.004"  # scripted group (container) (typed FeaturePython)
  n = 0.004
FEATURE [App::DocumentObjectGroupPython] S_element006  label="S_element : 0.005"  # scripted group (container) (typed FeaturePython)
  n = 0.002
FEATURE [App::DocumentObjectGroupPython] Cl_element003  label="Cl_element : 0.004"  # scripted group (container) (typed FeaturePython)
  n = 0.003
FEATURE [App::DocumentObjectGroupPython] K_element002  label="K_element : 0.003"  # scripted group (container) (typed FeaturePython)
  n = 0.003
FEATURE [App::DocumentObjectGroupPython] G4_BRAIN_ICRP  # scripted group (container) (typed FeaturePython)
  Dunit = g/cm3
  Dvalue = 1.04
  Group = -> [H_element017,C_element018,N_element012,O_element017,Na_element004,P_element004,S_element006,Cl_element003,K_element002]
  conduct = 2
  density = 1
  expand = 3
  formula = G4_BRAIN_ICRP
  name = G4_BRAIN_ICRP
  specific = 4
FEATURE [App::DocumentObjectGroupPython] C_element019  label="C_element : 4"  # scripted group (container) (typed FeaturePython)
  n = 4
  ref = C_element
FEATURE [App::DocumentObjectGroupPython] H_element018  label="H_element : 010"  # scripted group (container) (typed FeaturePython)
  n = 10
  ref = H_element
FEATURE [App::DocumentObjectGroupPython] G4_BUTANE  # scripted group (container) (typed FeaturePython)
  Dunit = g/cm3
  Dvalue = 0.00249343
  Group = -> [C_element019,H_element018]
  conduct = 2
  density = 1
  expand = 3
  formula = G4_BUTANE
  name = G4_BUTANE
  specific = 4
FEATURE [App::DocumentObjectGroupPython] C_element020  label="C_element : 008"  # scripted group (container) (typed FeaturePython)
  n = 4
  ref = C_element
FEATURE [App::DocumentObjectGroupPython] H_element019  label="H_element : 011"  # scripted group (container) (typed FeaturePython)
  n = 10
  ref = H_element
FEATURE [App::DocumentObjectGroupPython] O_element018  label="O_element : 007"  # scripted group (container) (typed FeaturePython)
  n = 1
  ref = O_element
FEATURE [App::DocumentObjectGroupPython] G4_N_BUTYL_ALCOHOL  label="G4_N-BUTYL_ALCOHOL"  # scripted group (container) (typed FeaturePython)
  Dunit = g/cm3
  Dvalue = 0.8098
  Group = -> [C_element020,H_element019,O_element018]
  conduct = 2
  density = 1
  expand = 3
  formula = G4_N-BUTYL_ALCOHOL
  name = G4_N-BUTYL_ALCOHOL
  specific = 4
FEATURE [App::DocumentObjectGroupPython] H_element020  label="H_element : 0.025"  # scripted group (container) (typed FeaturePython)
  n = 0.02468
FEATURE [App::DocumentObjectGroupPython] C_element021  label="C_element : 0.502"  # scripted group (container) (typed FeaturePython)
  n = 0.501611
FEATURE [App::DocumentObjectGroupPython] O_element019  label="O_element : 0.005"  # scripted group (container) (typed FeaturePython)
  n = 0.004527
FEATURE [App::DocumentObjectGroupPython] F_element004  label="F_element : 0.465"  # scripted group (container) (typed FeaturePython)
  n = 0.465209
FEATURE [App::DocumentObjectGroupPython] Si_element001  label="Si_element : 0.004"  # scripted group (container) (typed FeaturePython)
  n = 0.003973
FEATURE [App::DocumentObjectGroupPython] G4_C_552  label="G4_C-552"  # scripted group (container) (typed FeaturePython)
  Dunit = g/cm3
  Dvalue = 1.76
  Group = -> [H_element020,C_element021,O_element019,F_element004,Si_element001]
  conduct = 2
  density = 1
  expand = 3
  formula = G4_C-552
  name = G4_C-552
  specific = 4
FEATURE [App::DocumentObjectGroupPython] Cd_element001  label="Cd_element : 1"  # scripted group (container) (typed FeaturePython)
  n = 1
  ref = Cd_element
FEATURE [App::DocumentObjectGroupPython] Te_element001  label="Te_element : 1"  # scripted group (container) (typed FeaturePython)
  n = 1
  ref = Te_element
FEATURE [App::DocumentObjectGroupPython] G4_CADMIUM_TELLURIDE  # scripted group (container) (typed FeaturePython)
  Dunit = g/cm3
  Dvalue = 6.2
  Group = -> [Cd_element001,Te_element001]
  conduct = 2
  density = 1
  expand = 3
  formula = G4_CADMIUM_TELLURIDE
  name = G4_CADMIUM_TELLURIDE
  specific = 4
FEATURE [App::DocumentObjectGroupPython] Cd_element002  label="Cd_element : 002"  # scripted group (container) (typed FeaturePython)
  n = 1
  ref = Cd_element
FEATURE [App::DocumentObjectGroupPython] W_element001  label="W_element : 1"  # scripted group (container) (typed FeaturePython)
  n = 1
  ref = W_element
FEATURE [App::DocumentObjectGroupPython] O_element020  label="O_element : 008"  # scripted group (container) (typed FeaturePython)
  n = 4
  ref = O_element
FEATURE [App::DocumentObjectGroupPython] G4_CADMIUM_TUNGSTATE  # scripted group (container) (typed FeaturePython)
  Dunit = g/cm3
  Dvalue = 7.9
  Group = -> [Cd_element002,W_element001,O_element020]
  conduct = 2
  density = 1
  expand = 3
  formula = G4_CADMIUM_TUNGSTATE
  name = G4_CADMIUM_TUNGSTATE
  specific = 4
FEATURE [App::DocumentObjectGroupPython] Ca_element005  label="Ca_element : 1"  # scripted group (container) (typed FeaturePython)
  n = 1
  ref = Ca_element
FEATURE [App::DocumentObjectGroupPython] C_element022  label="C_element : 009"  # scripted group (container) (typed FeaturePython)
  n = 1
  ref = C_element
FEATURE [App::DocumentObjectGroupPython] O_element021  label="O_element : 009"  # scripted group (container) (typed FeaturePython)
  n = 3
  ref = O_element
FEATURE [App::DocumentObjectGroupPython] G4_CALCIUM_CARBONATE  # scripted group (container) (typed FeaturePython)
  Dunit = g/cm3
  Dvalue = 2.8
  Group = -> [Ca_element005,C_element022,O_element021]
  conduct = 2
  density = 1
  expand = 3
  formula = G4_CALCIUM_CARBONATE
  name = G4_CALCIUM_CARBONATE
  specific = 4
FEATURE [App::DocumentObjectGroupPython] Ca_element006  label="Ca_element : 002"  # scripted group (container) (typed FeaturePython)
  n = 1
  ref = Ca_element
FEATURE [App::DocumentObjectGroupPython] F_element005  label="F_element : 003"  # scripted group (container) (typed FeaturePython)
  n = 2
  ref = F_element
FEATURE [App::DocumentObjectGroupPython] G4_CALCIUM_FLUORIDE  # scripted group (container) (typed FeaturePython)
  Dunit = g/cm3
  Dvalue = 3.18
  Group = -> [Ca_element006,F_element005]
  conduct = 2
  density = 1
  expand = 3
  formula = G4_CALCIUM_FLUORIDE
  name = G4_CALCIUM_FLUORIDE
  specific = 4
FEATURE [App::DocumentObjectGroupPython] Ca_element007  label="Ca_element : 003"  # scripted group (container) (typed FeaturePython)
  n = 1
  ref = Ca_element
FEATURE [App::DocumentObjectGroupPython] O_element022  label="O_element : 010"  # scripted group (container) (typed FeaturePython)
  n = 1
  ref = O_element
FEATURE [App::DocumentObjectGroupPython] G4_CALCIUM_OXIDE  # scripted group (container) (typed FeaturePython)
  Dunit = g/cm3
  Dvalue = 3.3
  Group = -> [Ca_element007,O_element022]
  conduct = 2
  density = 1
  expand = 3
  formula = G4_CALCIUM_OXIDE
  name = G4_CALCIUM_OXIDE
  specific = 4
FEATURE [App::DocumentObjectGroupPython] Ca_element008  label="Ca_element : 004"  # scripted group (container) (typed FeaturePython)
  n = 1
  ref = Ca_element
FEATURE [App::DocumentObjectGroupPython] S_element007  label="S_element : 002"  # scripted group (container) (typed FeaturePython)
  n = 1
  ref = S_element
FEATURE [App::DocumentObjectGroupPython] O_element023  label="O_element : 011"  # scripted group (container) (typed FeaturePython)
  n = 4
  ref = O_element
FEATURE [App::DocumentObjectGroupPython] G4_CALCIUM_SULFATE  # scripted group (container) (typed FeaturePython)
  Dunit = g/cm3
  Dvalue = 2.96
  Group = -> [Ca_element008,S_element007,O_element023]
  conduct = 2
  density = 1
  expand = 3
  formula = G4_CALCIUM_SULFATE
  name = G4_CALCIUM_SULFATE
  specific = 4
FEATURE [App::DocumentObjectGroupPython] Ca_element009  label="Ca_element : 005"  # scripted group (container) (typed FeaturePython)
  n = 1
  ref = Ca_element
FEATURE [App::DocumentObjectGroupPython] W_element002  label="W_element : 002"  # scripted group (container) (typed FeaturePython)
  n = 1
  ref = W_element
FEATURE [App::DocumentObjectGroupPython] O_element024  label="O_element : 012"  # scripted group (container) (typed FeaturePython)
  n = 4
  ref = O_element
FEATURE [App::DocumentObjectGroupPython] G4_CALCIUM_TUNGSTATE  # scripted group (container) (typed FeaturePython)
  Dunit = g/cm3
  Dvalue = 6.062
  Group = -> [Ca_element009,W_element002,O_element024]
  conduct = 2
  density = 1
  expand = 3
  formula = G4_CALCIUM_TUNGSTATE
  name = G4_CALCIUM_TUNGSTATE
  specific = 4
FEATURE [App::DocumentObjectGroupPython] C_element023  label="C_element : 010"  # scripted group (container) (typed FeaturePython)
  n = 1
  ref = C_element
FEATURE [App::DocumentObjectGroupPython] O_element025  label="O_element : 013"  # scripted group (container) (typed FeaturePython)
  n = 2
  ref = O_element
FEATURE [App::DocumentObjectGroupPython] G4_CARBON_DIOXIDE  # scripted group (container) (typed FeaturePython)
  Dunit = g/cm3
  Dvalue = 0.00184212
  Group = -> [C_element023,O_element025]
  conduct = 2
  density = 1
  expand = 3
  formula = G4_CARBON_DIOXIDE
  name = G4_CARBON_DIOXIDE
  specific = 4
FEATURE [App::DocumentObjectGroupPython] C_element024  label="C_element : 011"  # scripted group (container) (typed FeaturePython)
  n = 1
  ref = C_element
FEATURE [App::DocumentObjectGroupPython] Cl_element004  label="Cl_element : 4"  # scripted group (container) (typed FeaturePython)
  n = 4
  ref = Cl_element
FEATURE [App::DocumentObjectGroupPython] G4_CARBON_TETRACHLORIDE  # scripted group (container) (typed FeaturePython)
  Dunit = g/cm3
  Dvalue = 1.594
  Group = -> [C_element024,Cl_element004]
  conduct = 2
  density = 1
  expand = 3
  formula = G4_CARBON_TETRACHLORIDE
  name = G4_CARBON_TETRACHLORIDE
  specific = 4
FEATURE [App::DocumentObjectGroupPython] C_element025  label="C_element : 012"  # scripted group (container) (typed FeaturePython)
  n = 6
  ref = C_element
FEATURE [App::DocumentObjectGroupPython] H_element021  label="H_element : 012"  # scripted group (container) (typed FeaturePython)
  n = 10
  ref = H_element
FEATURE [App::DocumentObjectGroupPython] O_element026  label="O_element : 5"  # scripted group (container) (typed FeaturePython)
  n = 5
  ref = O_element
FEATURE [App::DocumentObjectGroupPython] G4_CELLULOSE_CELLOPHANE  # scripted group (container) (typed FeaturePython)
  Dunit = g/cm3
  Dvalue = 1.42
  Group = -> [C_element025,H_element021,O_element026]
  conduct = 2
  density = 1
  expand = 3
  formula = G4_CELLULOSE_CELLOPHANE
  name = G4_CELLULOSE_CELLOPHANE
  specific = 4
FEATURE [App::DocumentObjectGroupPython] H_element022  label="H_element : 0.067"  # scripted group (container) (typed FeaturePython)
  n = 0.067125
FEATURE [App::DocumentObjectGroupPython] C_element026  label="C_element : 0.545"  # scripted group (container) (typed FeaturePython)
  n = 0.545403
FEATURE [App::DocumentObjectGroupPython] O_element027  label="O_element : 0.387"  # scripted group (container) (typed FeaturePython)
  n = 0.387472
FEATURE [App::DocumentObjectGroupPython] G4_CELLULOSE_BUTYRATE  # scripted group (container) (typed FeaturePython)
  Dunit = g/cm3
  Dvalue = 1.2
  Group = -> [H_element022,C_element026,O_element027]
  conduct = 2
  density = 1
  expand = 3
  formula = G4_CELLULOSE_BUTYRATE
  name = G4_CELLULOSE_BUTYRATE
  specific = 4
FEATURE [App::DocumentObjectGroupPython] H_element023  label="H_element : 0.029"  # scripted group (container) (typed FeaturePython)
  n = 0.029216
FEATURE [App::DocumentObjectGroupPython] C_element027  label="C_element : 0.271"  # scripted group (container) (typed FeaturePython)
  n = 0.271296
FEATURE [App::DocumentObjectGroupPython] N_element013  label="N_element : 0.121"  # scripted group (container) (typed FeaturePython)
  n = 0.121276
FEATURE [App::DocumentObjectGroupPython] O_element028  label="O_element : 0.578"  # scripted group (container) (typed FeaturePython)
  n = 0.578212
FEATURE [App::DocumentObjectGroupPython] G4_CELLULOSE_NITRATE  # scripted group (container) (typed FeaturePython)
  Dunit = g/cm3
  Dvalue = 1.49
  Group = -> [H_element023,C_element027,N_element013,O_element028]
  conduct = 2
  density = 1
  expand = 3
  formula = G4_CELLULOSE_NITRATE
  name = G4_CELLULOSE_NITRATE
  specific = 4
FEATURE [App::DocumentObjectGroupPython] H_element024  label="H_element : 0.108"  # scripted group (container) (typed FeaturePython)
  n = 0.107596
FEATURE [App::DocumentObjectGroupPython] N_element014  label="N_element : 0.001"  # scripted group (container) (typed FeaturePython)
  n = 0.0008
FEATURE [App::DocumentObjectGroupPython] O_element029  label="O_element : 0.875"  # scripted group (container) (typed FeaturePython)
  n = 0.874976
FEATURE [App::DocumentObjectGroupPython] S_element008  label="S_element : 0.015"  # scripted group (container) (typed FeaturePython)
  n = 0.014627
FEATURE [App::DocumentObjectGroupPython] Ce_element001  label="Ce_element : 0.002"  # scripted group (container) (typed FeaturePython)
  n = 0.002001
FEATURE [App::DocumentObjectGroupPython] G4_CERIC_SULFATE  # scripted group (container) (typed FeaturePython)
  Dunit = g/cm3
  Dvalue = 1.03
  Group = -> [H_element024,N_element014,O_element029,S_element008,Ce_element001]
  conduct = 2
  density = 1
  expand = 3
  formula = G4_CERIC_SULFATE
  name = G4_CERIC_SULFATE
  specific = 4
FEATURE [App::DocumentObjectGroupPython] Cs_element001  label="Cs_element : 1"  # scripted group (container) (typed FeaturePython)
  n = 1
  ref = Cs_element
FEATURE [App::DocumentObjectGroupPython] F_element006  label="F_element : 1"  # scripted group (container) (typed FeaturePython)
  n = 1
  ref = F_element
FEATURE [App::DocumentObjectGroupPython] G4_CESIUM_FLUORIDE  # scripted group (container) (typed FeaturePython)
  Dunit = g/cm3
  Dvalue = 4.115
  Group = -> [Cs_element001,F_element006]
  conduct = 2
  density = 1
  expand = 3
  formula = G4_CESIUM_FLUORIDE
  name = G4_CESIUM_FLUORIDE
  specific = 4
FEATURE [App::DocumentObjectGroupPython] Cs_element002  label="Cs_element : 002"  # scripted group (container) (typed FeaturePython)
  n = 1
  ref = Cs_element
FEATURE [App::DocumentObjectGroupPython] I_element001  label="I_element : 1"  # scripted group (container) (typed FeaturePython)
  n = 1
  ref = I_element
FEATURE [App::DocumentObjectGroupPython] G4_CESIUM_IODIDE  # scripted group (container) (typed FeaturePython)
  Dunit = g/cm3
  Dvalue = 4.51
  Group = -> [Cs_element002,I_element001]
  conduct = 2
  density = 1
  expand = 3
  formula = G4_CESIUM_IODIDE
  name = G4_CESIUM_IODIDE
  specific = 4
FEATURE [App::DocumentObjectGroupPython] C_element028  label="C_element : 013"  # scripted group (container) (typed FeaturePython)
  n = 6
  ref = C_element
FEATURE [App::DocumentObjectGroupPython] H_element025  label="H_element : 013"  # scripted group (container) (typed FeaturePython)
  n = 5
  ref = H_element
FEATURE [App::DocumentObjectGroupPython] Cl_element005  label="Cl_element : 1"  # scripted group (container) (typed FeaturePython)
  n = 1
  ref = Cl_element
FEATURE [App::DocumentObjectGroupPython] G4_CHLOROBENZENE  # scripted group (container) (typed FeaturePython)
  Dunit = g/cm3
  Dvalue = 1.1058
  Group = -> [C_element028,H_element025,Cl_element005]
  conduct = 2
  density = 1
  expand = 3
  formula = G4_CHLOROBENZENE
  name = G4_CHLOROBENZENE
  specific = 4
FEATURE [App::DocumentObjectGroupPython] C_element029  label="C_element : 014"  # scripted group (container) (typed FeaturePython)
  n = 1
  ref = C_element
FEATURE [App::DocumentObjectGroupPython] H_element026  label="H_element : 1"  # scripted group (container) (typed FeaturePython)
  n = 1
  ref = H_element
FEATURE [App::DocumentObjectGroupPython] Cl_element006  label="Cl_element : 3"  # scripted group (container) (typed FeaturePython)
  n = 3
  ref = Cl_element
FEATURE [App::DocumentObjectGroupPython] G4_CHLOROFORM  # scripted group (container) (typed FeaturePython)
  Dunit = g/cm3
  Dvalue = 1.4832
  Group = -> [C_element029,H_element026,Cl_element006]
  conduct = 2
  density = 1
  expand = 3
  formula = G4_CHLOROFORM
  name = G4_CHLOROFORM
  specific = 4
FEATURE [App::DocumentObjectGroupPython] H_element027  label="H_element : 0.010"  # scripted group (container) (typed FeaturePython)
  n = 0.01
FEATURE [App::DocumentObjectGroupPython] C_element030  label="C_element : 0.001"  # scripted group (container) (typed FeaturePython)
  n = 0.001
FEATURE [App::DocumentObjectGroupPython] O_element030  label="O_element : 0.529"  # scripted group (container) (typed FeaturePython)
  n = 0.529107
FEATURE [App::DocumentObjectGroupPython] Na_element005  label="Na_element : 0.016"  # scripted group (container) (typed FeaturePython)
  n = 0.016
FEATURE [App::DocumentObjectGroupPython] Mg_element003  label="Mg_element : 0.004"  # scripted group (container) (typed FeaturePython)
  n = 0.002
FEATURE [App::DocumentObjectGroupPython] Al_element002  label="Al_element : 0.034"  # scripted group (container) (typed FeaturePython)
  n = 0.033872
FEATURE [App::DocumentObjectGroupPython] Si_element002  label="Si_element : 0.337"  # scripted group (container) (typed FeaturePython)
  n = 0.337021
FEATURE [App::DocumentObjectGroupPython] K_element003  label="K_element : 0.013"  # scripted group (container) (typed FeaturePython)
  n = 0.013
FEATURE [App::DocumentObjectGroupPython] Ca_element010  label="Ca_element : 0.044"  # scripted group (container) (typed FeaturePython)
  n = 0.044
FEATURE [App::DocumentObjectGroupPython] Fe_element002  label="Fe_element : 0.014"  # scripted group (container) (typed FeaturePython)
  n = 0.014
FEATURE [App::DocumentObjectGroupPython] G4_CONCRETE  # scripted group (container) (typed FeaturePython)
  Dunit = g/cm3
  Dvalue = 2.3
  Group = -> [H_element027,C_element030,O_element030,Na_element005,Mg_element003,Al_element002,Si_element002,K_element003,Ca_element010,Fe_element002]
  conduct = 2
  density = 1
  expand = 3
  formula = G4_CONCRETE
  name = G4_CONCRETE
  specific = 4
FEATURE [App::DocumentObjectGroupPython] C_element031  label="C_element : 015"  # scripted group (container) (typed FeaturePython)
  n = 6
  ref = C_element
FEATURE [App::DocumentObjectGroupPython] H_element028  label="H_element : 12"  # scripted group (container) (typed FeaturePython)
  n = 12
  ref = H_element
FEATURE [App::DocumentObjectGroupPython] G4_CYCLOHEXANE  # scripted group (container) (typed FeaturePython)
  Dunit = g/cm3
  Dvalue = 0.779
  Group = -> [C_element031,H_element028]
  conduct = 2
  density = 1
  expand = 3
  formula = G4_CYCLOHEXANE
  name = G4_CYCLOHEXANE
  specific = 4
FEATURE [App::DocumentObjectGroupPython] C_element032  label="C_element : 016"  # scripted group (container) (typed FeaturePython)
  n = 6
  ref = C_element
FEATURE [App::DocumentObjectGroupPython] H_element029  label="H_element : 4"  # scripted group (container) (typed FeaturePython)
  n = 4
  ref = H_element
FEATURE [App::DocumentObjectGroupPython] Cl_element007  label="Cl_element : 2"  # scripted group (container) (typed FeaturePython)
  n = 2
  ref = Cl_element
FEATURE [App::DocumentObjectGroupPython] G4_1_2_DICHLOROBENZENE  label="G4_1.2-DICHLOROBENZENE"  # scripted group (container) (typed FeaturePython)
  Dunit = g/cm3
  Dvalue = 1.3048
  Group = -> [C_element032,H_element029,Cl_element007]
  conduct = 2
  density = 1
  expand = 3
  formula = G4_1.2-DICHLOROBENZENE
  name = G4_1.2-DICHLOROBENZENE
  specific = 4
FEATURE [App::DocumentObjectGroupPython] C_element033  label="C_element : 017"  # scripted group (container) (typed FeaturePython)
  n = 4
  ref = C_element
FEATURE [App::DocumentObjectGroupPython] H_element030  label="H_element : 8"  # scripted group (container) (typed FeaturePython)
  n = 8
  ref = H_element
FEATURE [App::DocumentObjectGroupPython] O_element031  label="O_element : 014"  # scripted group (container) (typed FeaturePython)
  n = 1
  ref = O_element
FEATURE [App::DocumentObjectGroupPython] Cl_element008  label="Cl_element : 005"  # scripted group (container) (typed FeaturePython)
  n = 2
  ref = Cl_element
FEATURE [App::DocumentObjectGroupPython] G4_DICHLORODIETHYL_ETHER  # scripted group (container) (typed FeaturePython)
  Dunit = g/cm3
  Dvalue = 1.2199
  Group = -> [C_element033,H_element030,O_element031,Cl_element008]
  conduct = 2
  density = 1
  expand = 3
  formula = G4_DICHLORODIETHYL_ETHER
  name = G4_DICHLORODIETHYL_ETHER
  specific = 4
FEATURE [App::DocumentObjectGroupPython] C_element034  label="C_element : 018"  # scripted group (container) (typed FeaturePython)
  n = 2
  ref = C_element
FEATURE [App::DocumentObjectGroupPython] H_element031  label="H_element : 014"  # scripted group (container) (typed FeaturePython)
  n = 4
  ref = H_element
FEATURE [App::DocumentObjectGroupPython] Cl_element009  label="Cl_element : 006"  # scripted group (container) (typed FeaturePython)
  n = 2
  ref = Cl_element
FEATURE [App::DocumentObjectGroupPython] G4_1_2_DICHLOROETHANE  label="G4_1.2-DICHLOROETHANE"  # scripted group (container) (typed FeaturePython)
  Dunit = g/cm3
  Dvalue = 1.2351
  Group = -> [C_element034,H_element031,Cl_element009]
  conduct = 2
  density = 1
  expand = 3
  formula = G4_1.2-DICHLOROETHANE
  name = G4_1.2-DICHLOROETHANE
  specific = 4
FEATURE [App::DocumentObjectGroupPython] C_element035  label="C_element : 019"  # scripted group (container) (typed FeaturePython)
  n = 4
  ref = C_element
FEATURE [App::DocumentObjectGroupPython] H_element032  label="H_element : 015"  # scripted group (container) (typed FeaturePython)
  n = 10
  ref = H_element
FEATURE [App::DocumentObjectGroupPython] O_element032  label="O_element : 015"  # scripted group (container) (typed FeaturePython)
  n = 1
  ref = O_element
FEATURE [App::DocumentObjectGroupPython] G4_DIETHYL_ETHER  # scripted group (container) (typed FeaturePython)
  Dunit = g/cm3
  Dvalue = 0.71378
  Group = -> [C_element035,H_element032,O_element032]
  conduct = 2
  density = 1
  expand = 3
  formula = G4_DIETHYL_ETHER
  name = G4_DIETHYL_ETHER
  specific = 4
FEATURE [App::DocumentObjectGroupPython] C_element036  label="C_element : 020"  # scripted group (container) (typed FeaturePython)
  n = 3
  ref = C_element
FEATURE [App::DocumentObjectGroupPython] H_element033  label="H_element : 016"  # scripted group (container) (typed FeaturePython)
  n = 7
  ref = H_element
FEATURE [App::DocumentObjectGroupPython] N_element015  label="N_element : 008"  # scripted group (container) (typed FeaturePython)
  n = 1
  ref = N_element
FEATURE [App::DocumentObjectGroupPython] O_element033  label="O_element : 016"  # scripted group (container) (typed FeaturePython)
  n = 1
  ref = O_element
FEATURE [App::DocumentObjectGroupPython] G4_N_N_DIMETHYL_FORMAMIDE  label="G4_N.N-DIMETHYL_FORMAMIDE"  # scripted group (container) (typed FeaturePython)
  Dunit = g/cm3
  Dvalue = 0.9487
  Group = -> [C_element036,H_element033,N_element015,O_element033]
  conduct = 2
  density = 1
  expand = 3
  formula = G4_N.N-DIMETHYL_FORMAMIDE
  name = G4_N.N-DIMETHYL_FORMAMIDE
  specific = 4
FEATURE [App::DocumentObjectGroupPython] C_element037  label="C_element : 021"  # scripted group (container) (typed FeaturePython)
  n = 2
  ref = C_element
FEATURE [App::DocumentObjectGroupPython] H_element034  label="H_element : 017"  # scripted group (container) (typed FeaturePython)
  n = 6
  ref = H_element
FEATURE [App::DocumentObjectGroupPython] O_element034  label="O_element : 017"  # scripted group (container) (typed FeaturePython)
  n = 1
  ref = O_element
FEATURE [App::DocumentObjectGroupPython] S_element009  label="S_element : 003"  # scripted group (container) (typed FeaturePython)
  n = 1
  ref = S_element
FEATURE [App::DocumentObjectGroupPython] G4_DIMETHYL_SULFOXIDE  # scripted group (container) (typed FeaturePython)
  Dunit = g/cm3
  Dvalue = 1.1014
  Group = -> [C_element037,H_element034,O_element034,S_element009]
  conduct = 2
  density = 1
  expand = 3
  formula = G4_DIMETHYL_SULFOXIDE
  name = G4_DIMETHYL_SULFOXIDE
  specific = 4
FEATURE [App::DocumentObjectGroupPython] C_element038  label="C_element : 022"  # scripted group (container) (typed FeaturePython)
  n = 2
  ref = C_element
FEATURE [App::DocumentObjectGroupPython] H_element035  label="H_element : 018"  # scripted group (container) (typed FeaturePython)
  n = 6
  ref = H_element
FEATURE [App::DocumentObjectGroupPython] G4_ETHANE  # scripted group (container) (typed FeaturePython)
  Dunit = g/cm3
  Dvalue = 0.00125324
  Group = -> [C_element038,H_element035]
  conduct = 2
  density = 1
  expand = 3
  formula = G4_ETHANE
  name = G4_ETHANE
  specific = 4
FEATURE [App::DocumentObjectGroupPython] C_element039  label="C_element : 023"  # scripted group (container) (typed FeaturePython)
  n = 2
  ref = C_element
FEATURE [App::DocumentObjectGroupPython] H_element036  label="H_element : 019"  # scripted group (container) (typed FeaturePython)
  n = 6
  ref = H_element
FEATURE [App::DocumentObjectGroupPython] O_element035  label="O_element : 018"  # scripted group (container) (typed FeaturePython)
  n = 1
  ref = O_element
FEATURE [App::DocumentObjectGroupPython] G4_ETHYL_ALCOHOL  # scripted group (container) (typed FeaturePython)
  Dunit = g/cm3
  Dvalue = 0.7893
  Group = -> [C_element039,H_element036,O_element035]
  conduct = 2
  density = 1
  expand = 3
  formula = G4_ETHYL_ALCOHOL
  name = G4_ETHYL_ALCOHOL
  specific = 4
FEATURE [App::DocumentObjectGroupPython] H_element037  label="H_element : 0.090"  # scripted group (container) (typed FeaturePython)
  n = 0.090027
FEATURE [App::DocumentObjectGroupPython] C_element040  label="C_element : 0.585"  # scripted group (container) (typed FeaturePython)
  n = 0.585182
FEATURE [App::DocumentObjectGroupPython] O_element036  label="O_element : 0.325"  # scripted group (container) (typed FeaturePython)
  n = 0.324791
FEATURE [App::DocumentObjectGroupPython] G4_ETHYL_CELLULOSE  # scripted group (container) (typed FeaturePython)
  Dunit = g/cm3
  Dvalue = 1.13
  Group = -> [H_element037,C_element040,O_element036]
  conduct = 2
  density = 1
  expand = 3
  formula = G4_ETHYL_CELLULOSE
  name = G4_ETHYL_CELLULOSE
  specific = 4
FEATURE [App::DocumentObjectGroupPython] C_element041  label="C_element : 024"  # scripted group (container) (typed FeaturePython)
  n = 2
  ref = C_element
FEATURE [App::DocumentObjectGroupPython] H_element038  label="H_element : 020"  # scripted group (container) (typed FeaturePython)
  n = 4
  ref = H_element
FEATURE [App::DocumentObjectGroupPython] G4_ETHYLENE  # scripted group (container) (typed FeaturePython)
  Dunit = g/cm3
  Dvalue = 0.00117497
  Group = -> [C_element041,H_element038]
  conduct = 2
  density = 1
  expand = 3
  formula = G4_ETHYLENE
  name = G4_ETHYLENE
  specific = 4
FEATURE [App::DocumentObjectGroupPython] H_element039  label="H_element : 0.096"  # scripted group (container) (typed FeaturePython)
  n = 0.096
FEATURE [App::DocumentObjectGroupPython] C_element042  label="C_element : 0.195"  # scripted group (container) (typed FeaturePython)
  n = 0.195
FEATURE [App::DocumentObjectGroupPython] N_element016  label="N_element : 0.057"  # scripted group (container) (typed FeaturePython)
  n = 0.057
FEATURE [App::DocumentObjectGroupPython] O_element037  label="O_element : 0.646"  # scripted group (container) (typed FeaturePython)
  n = 0.646
FEATURE [App::DocumentObjectGroupPython] Na_element006  label="Na_element : 0.017"  # scripted group (container) (typed FeaturePython)
  n = 0.001
FEATURE [App::DocumentObjectGroupPython] P_element005  label="P_element : 0.104"  # scripted group (container) (typed FeaturePython)
  n = 0.001
FEATURE [App::DocumentObjectGroupPython] S_element010  label="S_element : 0.016"  # scripted group (container) (typed FeaturePython)
  n = 0.003
FEATURE [App::DocumentObjectGroupPython] Cl_element010  label="Cl_element : 0.005"  # scripted group (container) (typed FeaturePython)
  n = 0.001
FEATURE [App::DocumentObjectGroupPython] G4_EYE_LENS_ICRP  # scripted group (container) (typed FeaturePython)
  Dunit = g/cm3
  Dvalue = 1.07
  Group = -> [H_element039,C_element042,N_element016,O_element037,Na_element006,P_element005,S_element010,Cl_element010]
  conduct = 2
  density = 1
  expand = 3
  formula = G4_EYE_LENS_ICRP
  name = G4_EYE_LENS_ICRP
  specific = 4
FEATURE [App::DocumentObjectGroupPython] Fe_element003  label="Fe_element : 2"  # scripted group (container) (typed FeaturePython)
  n = 2
  ref = Fe_element
FEATURE [App::DocumentObjectGroupPython] O_element038  label="O_element : 019"  # scripted group (container) (typed FeaturePython)
  n = 3
  ref = O_element
FEATURE [App::DocumentObjectGroupPython] G4_FERRIC_OXIDE  # scripted group (container) (typed FeaturePython)
  Dunit = g/cm3
  Dvalue = 5.2
  Group = -> [Fe_element003,O_element038]
  conduct = 2
  density = 1
  expand = 3
  formula = G4_FERRIC_OXIDE
  name = G4_FERRIC_OXIDE
  specific = 4
FEATURE [App::DocumentObjectGroupPython] Fe_element004  label="Fe_element : 1"  # scripted group (container) (typed FeaturePython)
  n = 1
  ref = Fe_element
FEATURE [App::DocumentObjectGroupPython] B_element003  label="B_element : 1"  # scripted group (container) (typed FeaturePython)
  n = 1
  ref = B_element
FEATURE [App::DocumentObjectGroupPython] G4_FERROBORIDE  # scripted group (container) (typed FeaturePython)
  Dunit = g/cm3
  Dvalue = 7.15
  Group = -> [Fe_element004,B_element003]
  conduct = 2
  density = 1
  expand = 3
  formula = G4_FERROBORIDE
  name = G4_FERROBORIDE
  specific = 4
FEATURE [App::DocumentObjectGroupPython] Fe_element005  label="Fe_element : 003"  # scripted group (container) (typed FeaturePython)
  n = 1
  ref = Fe_element
FEATURE [App::DocumentObjectGroupPython] O_element039  label="O_element : 020"  # scripted group (container) (typed FeaturePython)
  n = 1
  ref = O_element
FEATURE [App::DocumentObjectGroupPython] G4_FERROUS_OXIDE  # scripted group (container) (typed FeaturePython)
  Dunit = g/cm3
  Dvalue = 5.7
  Group = -> [Fe_element005,O_element039]
  conduct = 2
  density = 1
  expand = 3
  formula = G4_FERROUS_OXIDE
  name = G4_FERROUS_OXIDE
  specific = 4
FEATURE [App::DocumentObjectGroupPython] H_element040  label="H_element : 0.115"  # scripted group (container) (typed FeaturePython)
  n = 0.108259
FEATURE [App::DocumentObjectGroupPython] N_element017  label="N_element : 0.000"  # scripted group (container) (typed FeaturePython)
  n = 2.7e-05
FEATURE [App::DocumentObjectGroupPython] O_element040  label="O_element : 0.879"  # scripted group (container) (typed FeaturePython)
  n = 0.878636
FEATURE [App::DocumentObjectGroupPython] Na_element007  label="Na_element : 0.000"  # scripted group (container) (typed FeaturePython)
  n = 2.2e-05
FEATURE [App::DocumentObjectGroupPython] S_element011  label="S_element : 0.013"  # scripted group (container) (typed FeaturePython)
  n = 0.012968
FEATURE [App::DocumentObjectGroupPython] Cl_element011  label="Cl_element : 0.000"  # scripted group (container) (typed FeaturePython)
  n = 3.4e-05
FEATURE [App::DocumentObjectGroupPython] Fe_element006  label="Fe_element : 0.000"  # scripted group (container) (typed FeaturePython)
  n = 5.4e-05
FEATURE [App::DocumentObjectGroupPython] G4_FERROUS_SULFATE  # scripted group (container) (typed FeaturePython)
  Dunit = g/cm3
  Dvalue = 1.024
  Group = -> [H_element040,N_element017,O_element040,Na_element007,S_element011,Cl_element011,Fe_element006]
  conduct = 2
  density = 1
  expand = 3
  formula = G4_FERROUS_SULFATE
  name = G4_FERROUS_SULFATE
  specific = 4
FEATURE [App::DocumentObjectGroupPython] C_element043  label="C_element : 0.099"  # scripted group (container) (typed FeaturePython)
  n = 0.099335
FEATURE [App::DocumentObjectGroupPython] F_element007  label="F_element : 0.314"  # scripted group (container) (typed FeaturePython)
  n = 0.314247
FEATURE [App::DocumentObjectGroupPython] Cl_element012  label="Cl_element : 0.586"  # scripted group (container) (typed FeaturePython)
  n = 0.586418
FEATURE [App::DocumentObjectGroupPython] G4_FREON_12  label="G4_FREON-12"  # scripted group (container) (typed FeaturePython)
  Dunit = g/cm3
  Dvalue = 1.12
  Group = -> [C_element043,F_element007,Cl_element012]
  conduct = 2
  density = 1
  expand = 3
  formula = G4_FREON-12
  name = G4_FREON-12
  specific = 4
FEATURE [App::DocumentObjectGroupPython] C_element044  label="C_element : 0.057"  # scripted group (container) (typed FeaturePython)
  n = 0.057245
FEATURE [App::DocumentObjectGroupPython] F_element008  label="F_element : 0.181"  # scripted group (container) (typed FeaturePython)
  n = 0.181096
FEATURE [App::DocumentObjectGroupPython] Br_element001  label="Br_element : 0.762"  # scripted group (container) (typed FeaturePython)
  n = 0.761659
FEATURE [App::DocumentObjectGroupPython] G4_FREON_12B2  label="G4_FREON-12B2"  # scripted group (container) (typed FeaturePython)
  Dunit = g/cm3
  Dvalue = 1.8
  Group = -> [C_element044,F_element008,Br_element001]
  conduct = 2
  density = 1
  expand = 3
  formula = G4_FREON-12B2
  name = G4_FREON-12B2
  specific = 4
FEATURE [App::DocumentObjectGroupPython] C_element045  label="C_element : 0.115"  # scripted group (container) (typed FeaturePython)
  n = 0.114983
FEATURE [App::DocumentObjectGroupPython] F_element009  label="F_element : 0.546"  # scripted group (container) (typed FeaturePython)
  n = 0.545621
FEATURE [App::DocumentObjectGroupPython] Cl_element013  label="Cl_element : 0.339"  # scripted group (container) (typed FeaturePython)
  n = 0.339396
FEATURE [App::DocumentObjectGroupPython] G4_FREON_13  label="G4_FREON-13"  # scripted group (container) (typed FeaturePython)
  Dunit = g/cm3
  Dvalue = 0.95
  Group = -> [C_element045,F_element009,Cl_element013]
  conduct = 2
  density = 1
  expand = 3
  formula = G4_FREON-13
  name = G4_FREON-13
  specific = 4
FEATURE [App::DocumentObjectGroupPython] C_element046  label="C_element : 025"  # scripted group (container) (typed FeaturePython)
  n = 1
  ref = C_element
FEATURE [App::DocumentObjectGroupPython] F_element010  label="F_element : 3"  # scripted group (container) (typed FeaturePython)
  n = 3
  ref = F_element
FEATURE [App::DocumentObjectGroupPython] Br_element002  label="Br_element : 1"  # scripted group (container) (typed FeaturePython)
  n = 1
  ref = Br_element
FEATURE [App::DocumentObjectGroupPython] G4_FREON_13B1  label="G4_FREON-13B1"  # scripted group (container) (typed FeaturePython)
  Dunit = g/cm3
  Dvalue = 1.5
  Group = -> [C_element046,F_element010,Br_element002]
  conduct = 2
  density = 1
  expand = 3
  formula = G4_FREON-13B1
  name = G4_FREON-13B1
  specific = 4
FEATURE [App::DocumentObjectGroupPython] C_element047  label="C_element : 0.061"  # scripted group (container) (typed FeaturePython)
  n = 0.061309
FEATURE [App::DocumentObjectGroupPython] F_element011  label="F_element : 0.291"  # scripted group (container) (typed FeaturePython)
  n = 0.290924
FEATURE [App::DocumentObjectGroupPython] I_element002  label="I_element : 0.648"  # scripted group (container) (typed FeaturePython)
  n = 0.647767
FEATURE [App::DocumentObjectGroupPython] G4_FREON_13I1  label="G4_FREON-13I1"  # scripted group (container) (typed FeaturePython)
  Dunit = g/cm3
  Dvalue = 1.8
  Group = -> [C_element047,F_element011,I_element002]
  conduct = 2
  density = 1
  expand = 3
  formula = G4_FREON-13I1
  name = G4_FREON-13I1
  specific = 4
FEATURE [App::DocumentObjectGroupPython] Gd_element001  label="Gd_element : 2"  # scripted group (container) (typed FeaturePython)
  n = 2
  ref = Gd_element
FEATURE [App::DocumentObjectGroupPython] O_element041  label="O_element : 021"  # scripted group (container) (typed FeaturePython)
  n = 2
  ref = O_element
FEATURE [App::DocumentObjectGroupPython] S_element012  label="S_element : 004"  # scripted group (container) (typed FeaturePython)
  n = 1
  ref = S_element
FEATURE [App::DocumentObjectGroupPython] G4_GADOLINIUM_OXYSULFIDE  # scripted group (container) (typed FeaturePython)
  Dunit = g/cm3
  Dvalue = 7.44
  Group = -> [Gd_element001,O_element041,S_element012]
  conduct = 2
  density = 1
  expand = 3
  formula = G4_GADOLINIUM_OXYSULFIDE
  name = G4_GADOLINIUM_OXYSULFIDE
  specific = 4
FEATURE [App::DocumentObjectGroupPython] Ga_element001  label="Ga_element : 1"  # scripted group (container) (typed FeaturePython)
  n = 1
  ref = Ga_element
FEATURE [App::DocumentObjectGroupPython] As_element001  label="As_element : 1"  # scripted group (container) (typed FeaturePython)
  n = 1
  ref = As_element
FEATURE [App::DocumentObjectGroupPython] G4_GALLIUM_ARSENIDE  # scripted group (container) (typed FeaturePython)
  Dunit = g/cm3
  Dvalue = 5.31
  Group = -> [Ga_element001,As_element001]
  conduct = 2
  density = 1
  expand = 3
  formula = G4_GALLIUM_ARSENIDE
  name = G4_GALLIUM_ARSENIDE
  specific = 4
FEATURE [App::DocumentObjectGroupPython] H_element041  label="H_element : 0.081"  # scripted group (container) (typed FeaturePython)
  n = 0.08118
FEATURE [App::DocumentObjectGroupPython] C_element048  label="C_element : 0.416"  # scripted group (container) (typed FeaturePython)
  n = 0.41606
FEATURE [App::DocumentObjectGroupPython] N_element018  label="N_element : 0.111"  # scripted group (container) (typed FeaturePython)
  n = 0.11124
FEATURE [App::DocumentObjectGroupPython] O_element042  label="O_element : 0.381"  # scripted group (container) (typed FeaturePython)
  n = 0.38064
FEATURE [App::DocumentObjectGroupPython] S_element013  label="S_element : 0.011"  # scripted group (container) (typed FeaturePython)
  n = 0.01088
FEATURE [App::DocumentObjectGroupPython] G4_GEL_PHOTO_EMULSION  # scripted group (container) (typed FeaturePython)
  Dunit = g/cm3
  Dvalue = 1.2914
  Group = -> [H_element041,C_element048,N_element018,O_element042,S_element013]
  conduct = 2
  density = 1
  expand = 3
  formula = G4_GEL_PHOTO_EMULSION
  name = G4_GEL_PHOTO_EMULSION
  specific = 4
FEATURE [App::DocumentObjectGroupPython] B_element004  label="B_element : 0.040"  # scripted group (container) (typed FeaturePython)
  n = 0.0400639
FEATURE [App::DocumentObjectGroupPython] O_element043  label="O_element : 0.540"  # scripted group (container) (typed FeaturePython)
  n = 0.539561
FEATURE [App::DocumentObjectGroupPython] Na_element008  label="Na_element : 0.028"  # scripted group (container) (typed FeaturePython)
  n = 0.0281909
FEATURE [App::DocumentObjectGroupPython] Al_element003  label="Al_element : 0.012"  # scripted group (container) (typed FeaturePython)
  n = 0.011644
FEATURE [App::DocumentObjectGroupPython] Si_element003  label="Si_element : 0.377"  # scripted group (container) (typed FeaturePython)
  n = 0.377219
FEATURE [App::DocumentObjectGroupPython] K_element004  label="K_element : 0.014"  # scripted group (container) (typed FeaturePython)
  n = 0.00332099
FEATURE [App::DocumentObjectGroupPython] G4_Pyrex_Glass  # scripted group (container) (typed FeaturePython)
  Dunit = g/cm3
  Dvalue = 2.23
  Group = -> [B_element004,O_element043,Na_element008,Al_element003,Si_element003,K_element004]
  conduct = 2
  density = 1
  expand = 3
  formula = G4_Pyrex_Glass
  name = G4_Pyrex_Glass
  specific = 4
FEATURE [App::DocumentObjectGroupPython] O_element044  label="O_element : 0.156"  # scripted group (container) (typed FeaturePython)
  n = 0.156453
FEATURE [App::DocumentObjectGroupPython] Si_element004  label="Si_element : 0.081"  # scripted group (container) (typed FeaturePython)
  n = 0.080866
FEATURE [App::DocumentObjectGroupPython] Ti_element001  label="Ti_element : 0.008"  # scripted group (container) (typed FeaturePython)
  n = 0.008092
FEATURE [App::DocumentObjectGroupPython] As_element002  label="As_element : 0.003"  # scripted group (container) (typed FeaturePython)
  n = 0.002651
FEATURE [App::DocumentObjectGroupPython] Pb_element001  label="Pb_element : 0.752"  # scripted group (container) (typed FeaturePython)
  n = 0.751938
FEATURE [App::DocumentObjectGroupPython] G4_GLASS_LEAD  # scripted group (container) (typed FeaturePython)
  Dunit = g/cm3
  Dvalue = 6.22
  Group = -> [O_element044,Si_element004,Ti_element001,As_element002,Pb_element001]
  conduct = 2
  density = 1
  expand = 3
  formula = G4_GLASS_LEAD
  name = G4_GLASS_LEAD
  specific = 4
FEATURE [App::DocumentObjectGroupPython] O_element045  label="O_element : 0.460"  # scripted group (container) (typed FeaturePython)
  n = 0.4598
FEATURE [App::DocumentObjectGroupPython] Na_element009  label="Na_element : 0.096"  # scripted group (container) (typed FeaturePython)
  n = 0.0964411
FEATURE [App::DocumentObjectGroupPython] Si_element005  label="Si_element : 0.378"  # scripted group (container) (typed FeaturePython)
  n = 0.336553
FEATURE [App::DocumentObjectGroupPython] Ca_element011  label="Ca_element : 0.107"  # scripted group (container) (typed FeaturePython)
  n = 0.107205
FEATURE [App::DocumentObjectGroupPython] G4_GLASS_PLATE  # scripted group (container) (typed FeaturePython)
  Dunit = g/cm3
  Dvalue = 2.4
  Group = -> [O_element045,Na_element009,Si_element005,Ca_element011]
  conduct = 2
  density = 1
  expand = 3
  formula = G4_GLASS_PLATE
  name = G4_GLASS_PLATE
  specific = 4
FEATURE [App::DocumentObjectGroupPython] C_element049  label="C_element : 026"  # scripted group (container) (typed FeaturePython)
  n = 5
  ref = C_element
FEATURE [App::DocumentObjectGroupPython] H_element042  label="H_element : 021"  # scripted group (container) (typed FeaturePython)
  n = 10
  ref = H_element
FEATURE [App::DocumentObjectGroupPython] N_element019  label="N_element : 2"  # scripted group (container) (typed FeaturePython)
  n = 2
  ref = N_element
FEATURE [App::DocumentObjectGroupPython] O_element046  label="O_element : 022"  # scripted group (container) (typed FeaturePython)
  n = 3
  ref = O_element
FEATURE [App::DocumentObjectGroupPython] G4_GLUTAMINE  # scripted group (container) (typed FeaturePython)
  Dunit = g/cm3
  Dvalue = 1.46
  Group = -> [C_element049,H_element042,N_element019,O_element046]
  conduct = 2
  density = 1
  expand = 3
  formula = G4_GLUTAMINE
  name = G4_GLUTAMINE
  specific = 4
FEATURE [App::DocumentObjectGroupPython] C_element050  label="C_element : 027"  # scripted group (container) (typed FeaturePython)
  n = 3
  ref = C_element
FEATURE [App::DocumentObjectGroupPython] H_element043  label="H_element : 022"  # scripted group (container) (typed FeaturePython)
  n = 8
  ref = H_element
FEATURE [App::DocumentObjectGroupPython] O_element047  label="O_element : 023"  # scripted group (container) (typed FeaturePython)
  n = 3
  ref = O_element
FEATURE [App::DocumentObjectGroupPython] G4_GLYCEROL  # scripted group (container) (typed FeaturePython)
  Dunit = g/cm3
  Dvalue = 1.2613
  Group = -> [C_element050,H_element043,O_element047]
  conduct = 2
  density = 1
  expand = 3
  formula = G4_GLYCEROL
  name = G4_GLYCEROL
  specific = 4
FEATURE [App::DocumentObjectGroupPython] C_element051  label="C_element : 028"  # scripted group (container) (typed FeaturePython)
  n = 5
  ref = C_element
FEATURE [App::DocumentObjectGroupPython] H_element044  label="H_element : 023"  # scripted group (container) (typed FeaturePython)
  n = 5
  ref = H_element
FEATURE [App::DocumentObjectGroupPython] N_element020  label="N_element : 009"  # scripted group (container) (typed FeaturePython)
  n = 5
  ref = N_element
FEATURE [App::DocumentObjectGroupPython] O_element048  label="O_element : 024"  # scripted group (container) (typed FeaturePython)
  n = 1
  ref = O_element
FEATURE [App::DocumentObjectGroupPython] G4_GUANINE  # scripted group (container) (typed FeaturePython)
  Dunit = g/cm3
  Dvalue = 2.2
  Group = -> [C_element051,H_element044,N_element020,O_element048]
  conduct = 2
  density = 1
  expand = 3
  formula = G4_GUANINE
  name = G4_GUANINE
  specific = 4
FEATURE [App::DocumentObjectGroupPython] Ca_element012  label="Ca_element : 006"  # scripted group (container) (typed FeaturePython)
  n = 1
  ref = Ca_element
FEATURE [App::DocumentObjectGroupPython] S_element014  label="S_element : 005"  # scripted group (container) (typed FeaturePython)
  n = 1
  ref = S_element
FEATURE [App::DocumentObjectGroupPython] O_element049  label="O_element : 6"  # scripted group (container) (typed FeaturePython)
  n = 6
  ref = O_element
FEATURE [App::DocumentObjectGroupPython] H_element045  label="H_element : 024"  # scripted group (container) (typed FeaturePython)
  n = 4
  ref = H_element
FEATURE [App::DocumentObjectGroupPython] G4_GYPSUM  # scripted group (container) (typed FeaturePython)
  Dunit = g/cm3
  Dvalue = 2.32
  Group = -> [Ca_element012,S_element014,O_element049,H_element045]
  conduct = 2
  density = 1
  expand = 3
  formula = G4_GYPSUM
  name = G4_GYPSUM
  specific = 4
FEATURE [App::DocumentObjectGroupPython] C_element052  label="C_element : 7"  # scripted group (container) (typed FeaturePython)
  n = 7
  ref = C_element
FEATURE [App::DocumentObjectGroupPython] H_element046  label="H_element : 16"  # scripted group (container) (typed FeaturePython)
  n = 16
  ref = H_element
FEATURE [App::DocumentObjectGroupPython] G4_N_HEPTANE  label="G4_N-HEPTANE"  # scripted group (container) (typed FeaturePython)
  Dunit = g/cm3
  Dvalue = 0.68376
  Group = -> [C_element052,H_element046]
  conduct = 2
  density = 1
  expand = 3
  formula = G4_N-HEPTANE
  name = G4_N-HEPTANE
  specific = 4
FEATURE [App::DocumentObjectGroupPython] C_element053  label="C_element : 029"  # scripted group (container) (typed FeaturePython)
  n = 6
  ref = C_element
FEATURE [App::DocumentObjectGroupPython] H_element047  label="H_element : 14"  # scripted group (container) (typed FeaturePython)
  n = 14
  ref = H_element
FEATURE [App::DocumentObjectGroupPython] G4_N_HEXANE  label="G4_N-HEXANE"  # scripted group (container) (typed FeaturePython)
  Dunit = g/cm3
  Dvalue = 0.6603
  Group = -> [C_element053,H_element047]
  conduct = 2
  density = 1
  expand = 3
  formula = G4_N-HEXANE
  name = G4_N-HEXANE
  specific = 4
FEATURE [App::DocumentObjectGroupPython] C_element054  label="C_element : 22"  # scripted group (container) (typed FeaturePython)
  n = 22
  ref = C_element
FEATURE [App::DocumentObjectGroupPython] H_element048  label="H_element : 025"  # scripted group (container) (typed FeaturePython)
  n = 10
  ref = H_element
FEATURE [App::DocumentObjectGroupPython] N_element021  label="N_element : 010"  # scripted group (container) (typed FeaturePython)
  n = 2
  ref = N_element
FEATURE [App::DocumentObjectGroupPython] O_element050  label="O_element : 025"  # scripted group (container) (typed FeaturePython)
  n = 5
  ref = O_element
FEATURE [App::DocumentObjectGroupPython] G4_KAPTON  # scripted group (container) (typed FeaturePython)
  Dunit = g/cm3
  Dvalue = 1.42
  Group = -> [C_element054,H_element048,N_element021,O_element050]
  conduct = 2
  density = 1
  expand = 3
  formula = G4_KAPTON
  name = G4_KAPTON
  specific = 4
FEATURE [App::DocumentObjectGroupPython] La_element001  label="La_element : 1"  # scripted group (container) (typed FeaturePython)
  n = 1
  ref = La_element
FEATURE [App::DocumentObjectGroupPython] Br_element003  label="Br_element : 002"  # scripted group (container) (typed FeaturePython)
  n = 1
  ref = Br_element
FEATURE [App::DocumentObjectGroupPython] O_element051  label="O_element : 026"  # scripted group (container) (typed FeaturePython)
  n = 1
  ref = O_element
FEATURE [App::DocumentObjectGroupPython] G4_LANTHANUM_OXYBROMIDE  # scripted group (container) (typed FeaturePython)
  Dunit = g/cm3
  Dvalue = 6.28
  Group = -> [La_element001,Br_element003,O_element051]
  conduct = 2
  density = 1
  expand = 3
  formula = G4_LANTHANUM_OXYBROMIDE
  name = G4_LANTHANUM_OXYBROMIDE
  specific = 4
FEATURE [App::DocumentObjectGroupPython] La_element002  label="La_element : 2"  # scripted group (container) (typed FeaturePython)
  n = 2
  ref = La_element
FEATURE [App::DocumentObjectGroupPython] O_element052  label="O_element : 027"  # scripted group (container) (typed FeaturePython)
  n = 2
  ref = O_element
FEATURE [App::DocumentObjectGroupPython] S_element015  label="S_element : 006"  # scripted group (container) (typed FeaturePython)
  n = 1
  ref = S_element
FEATURE [App::DocumentObjectGroupPython] G4_LANTHANUM_OXYSULFIDE  # scripted group (container) (typed FeaturePython)
  Dunit = g/cm3
  Dvalue = 5.86
  Group = -> [La_element002,O_element052,S_element015]
  conduct = 2
  density = 1
  expand = 3
  formula = G4_LANTHANUM_OXYSULFIDE
  name = G4_LANTHANUM_OXYSULFIDE
  specific = 4
FEATURE [App::DocumentObjectGroupPython] O_element053  label="O_element : 0.072"  # scripted group (container) (typed FeaturePython)
  n = 0.071682
FEATURE [App::DocumentObjectGroupPython] Pb_element002  label="Pb_element : 0.928"  # scripted group (container) (typed FeaturePython)
  n = 0.928318
FEATURE [App::DocumentObjectGroupPython] G4_LEAD_OXIDE  # scripted group (container) (typed FeaturePython)
  Dunit = g/cm3
  Dvalue = 9.53
  Group = -> [O_element053,Pb_element002]
  conduct = 2
  density = 1
  expand = 3
  formula = G4_LEAD_OXIDE
  name = G4_LEAD_OXIDE
  specific = 4
FEATURE [App::DocumentObjectGroupPython] Li_element001  label="Li_element : 1"  # scripted group (container) (typed FeaturePython)
  n = 1
  ref = Li_element
FEATURE [App::DocumentObjectGroupPython] N_element022  label="N_element : 011"  # scripted group (container) (typed FeaturePython)
  n = 1
  ref = N_element
FEATURE [App::DocumentObjectGroupPython] H_element049  label="H_element : 026"  # scripted group (container) (typed FeaturePython)
  n = 2
  ref = H_element
FEATURE [App::DocumentObjectGroupPython] G4_LITHIUM_AMIDE  # scripted group (container) (typed FeaturePython)
  Dunit = g/cm3
  Dvalue = 1.178
  Group = -> [Li_element001,N_element022,H_element049]
  conduct = 2
  density = 1
  expand = 3
  formula = G4_LITHIUM_AMIDE
  name = G4_LITHIUM_AMIDE
  specific = 4
FEATURE [App::DocumentObjectGroupPython] Li_element002  label="Li_element : 2"  # scripted group (container) (typed FeaturePython)
  n = 2
  ref = Li_element
FEATURE [App::DocumentObjectGroupPython] C_element055  label="C_element : 030"  # scripted group (container) (typed FeaturePython)
  n = 1
  ref = C_element
FEATURE [App::DocumentObjectGroupPython] O_element054  label="O_element : 028"  # scripted group (container) (typed FeaturePython)
  n = 3
  ref = O_element
FEATURE [App::DocumentObjectGroupPython] G4_LITHIUM_CARBONATE  # scripted group (container) (typed FeaturePython)
  Dunit = g/cm3
  Dvalue = 2.11
  Group = -> [Li_element002,C_element055,O_element054]
  conduct = 2
  density = 1
  expand = 3
  formula = G4_LITHIUM_CARBONATE
  name = G4_LITHIUM_CARBONATE
  specific = 4
FEATURE [App::DocumentObjectGroupPython] Li_element003  label="Li_element : 003"  # scripted group (container) (typed FeaturePython)
  n = 1
  ref = Li_element
FEATURE [App::DocumentObjectGroupPython] F_element012  label="F_element : 004"  # scripted group (container) (typed FeaturePython)
  n = 1
  ref = F_element
FEATURE [App::DocumentObjectGroupPython] G4_LITHIUM_FLUORIDE  # scripted group (container) (typed FeaturePython)
  Dunit = g/cm3
  Dvalue = 2.635
  Group = -> [Li_element003,F_element012]
  conduct = 2
  density = 1
  expand = 3
  formula = G4_LITHIUM_FLUORIDE
  name = G4_LITHIUM_FLUORIDE
  specific = 4
FEATURE [App::DocumentObjectGroupPython] Li_element004  label="Li_element : 004"  # scripted group (container) (typed FeaturePython)
  n = 1
  ref = Li_element
FEATURE [App::DocumentObjectGroupPython] H_element050  label="H_element : 027"  # scripted group (container) (typed FeaturePython)
  n = 1
  ref = H_element
FEATURE [App::DocumentObjectGroupPython] G4_LITHIUM_HYDRIDE  # scripted group (container) (typed FeaturePython)
  Dunit = g/cm3
  Dvalue = 0.82
  Group = -> [Li_element004,H_element050]
  conduct = 2
  density = 1
  expand = 3
  formula = G4_LITHIUM_HYDRIDE
  name = G4_LITHIUM_HYDRIDE
  specific = 4
FEATURE [App::DocumentObjectGroupPython] Li_element005  label="Li_element : 005"  # scripted group (container) (typed FeaturePython)
  n = 1
  ref = Li_element
FEATURE [App::DocumentObjectGroupPython] I_element003  label="I_element : 002"  # scripted group (container) (typed FeaturePython)
  n = 1
  ref = I_element
FEATURE [App::DocumentObjectGroupPython] G4_LITHIUM_IODIDE  # scripted group (container) (typed FeaturePython)
  Dunit = g/cm3
  Dvalue = 3.494
  Group = -> [Li_element005,I_element003]
  conduct = 2
  density = 1
  expand = 3
  formula = G4_LITHIUM_IODIDE
  name = G4_LITHIUM_IODIDE
  specific = 4
FEATURE [App::DocumentObjectGroupPython] Li_element006  label="Li_element : 006"  # scripted group (container) (typed FeaturePython)
  n = 2
  ref = Li_element
FEATURE [App::DocumentObjectGroupPython] O_element055  label="O_element : 029"  # scripted group (container) (typed FeaturePython)
  n = 1
  ref = O_element
FEATURE [App::DocumentObjectGroupPython] G4_LITHIUM_OXIDE  # scripted group (container) (typed FeaturePython)
  Dunit = g/cm3
  Dvalue = 2.013
  Group = -> [Li_element006,O_element055]
  conduct = 2
  density = 1
  expand = 3
  formula = G4_LITHIUM_OXIDE
  name = G4_LITHIUM_OXIDE
  specific = 4
FEATURE [App::DocumentObjectGroupPython] Li_element007  label="Li_element : 007"  # scripted group (container) (typed FeaturePython)
  n = 2
  ref = Li_element
FEATURE [App::DocumentObjectGroupPython] B_element005  label="B_element : 005"  # scripted group (container) (typed FeaturePython)
  n = 4
  ref = B_element
FEATURE [App::DocumentObjectGroupPython] O_element056  label="O_element : 7"  # scripted group (container) (typed FeaturePython)
  n = 7
  ref = O_element
FEATURE [App::DocumentObjectGroupPython] G4_LITHIUM_TETRABORATE  # scripted group (container) (typed FeaturePython)
  Dunit = g/cm3
  Dvalue = 2.44
  Group = -> [Li_element007,B_element005,O_element056]
  conduct = 2
  density = 1
  expand = 3
  formula = G4_LITHIUM_TETRABORATE
  name = G4_LITHIUM_TETRABORATE
  specific = 4
FEATURE [App::DocumentObjectGroupPython] H_element051  label="H_element : 0.105"  # scripted group (container) (typed FeaturePython)
  n = 0.105
FEATURE [App::DocumentObjectGroupPython] C_element056  label="C_element : 0.083"  # scripted group (container) (typed FeaturePython)
  n = 0.083
FEATURE [App::DocumentObjectGroupPython] N_element023  label="N_element : 0.023"  # scripted group (container) (typed FeaturePython)
  n = 0.023
FEATURE [App::DocumentObjectGroupPython] O_element057  label="O_element : 0.779"  # scripted group (container) (typed FeaturePython)
  n = 0.779
FEATURE [App::DocumentObjectGroupPython] Na_element010  label="Na_element : 0.097"  # scripted group (container) (typed FeaturePython)
  n = 0.002
FEATURE [App::DocumentObjectGroupPython] P_element006  label="P_element : 0.105"  # scripted group (container) (typed FeaturePython)
  n = 0.001
FEATURE [App::DocumentObjectGroupPython] S_element016  label="S_element : 0.017"  # scripted group (container) (typed FeaturePython)
  n = 0.002
FEATURE [App::DocumentObjectGroupPython] Cl_element014  label="Cl_element : 0.587"  # scripted group (container) (typed FeaturePython)
  n = 0.003
FEATURE [App::DocumentObjectGroupPython] K_element005  label="K_element : 0.015"  # scripted group (container) (typed FeaturePython)
  n = 0.002
FEATURE [App::DocumentObjectGroupPython] G4_LUNG_ICRP  # scripted group (container) (typed FeaturePython)
  Dunit = g/cm3
  Dvalue = 1.04
  Group = -> [H_element051,C_element056,N_element023,O_element057,Na_element010,P_element006,S_element016,Cl_element014,K_element005]
  conduct = 2
  density = 1
  expand = 3
  formula = G4_LUNG_ICRP
  name = G4_LUNG_ICRP
  specific = 4
FEATURE [App::DocumentObjectGroupPython] H_element052  label="H_element : 0.116"  # scripted group (container) (typed FeaturePython)
  n = 0.114318
FEATURE [App::DocumentObjectGroupPython] C_element057  label="C_element : 0.656"  # scripted group (container) (typed FeaturePython)
  n = 0.655824
FEATURE [App::DocumentObjectGroupPython] O_element058  label="O_element : 0.092"  # scripted group (container) (typed FeaturePython)
  n = 0.0921831
FEATURE [App::DocumentObjectGroupPython] Mg_element004  label="Mg_element : 0.135"  # scripted group (container) (typed FeaturePython)
  n = 0.134792
FEATURE [App::DocumentObjectGroupPython] Ca_element013  label="Ca_element : 0.003"  # scripted group (container) (typed FeaturePython)
  n = 0.002883
FEATURE [App::DocumentObjectGroupPython] G4_M3_WAX  # scripted group (container) (typed FeaturePython)
  Dunit = g/cm3
  Dvalue = 1.05
  Group = -> [H_element052,C_element057,O_element058,Mg_element004,Ca_element013]
  conduct = 2
  density = 1
  expand = 3
  formula = G4_M3_WAX
  name = G4_M3_WAX
  specific = 4
FEATURE [App::DocumentObjectGroupPython] Mg_element005  label="Mg_element : 1"  # scripted group (container) (typed FeaturePython)
  n = 1
  ref = Mg_element
FEATURE [App::DocumentObjectGroupPython] C_element058  label="C_element : 031"  # scripted group (container) (typed FeaturePython)
  n = 1
  ref = C_element
FEATURE [App::DocumentObjectGroupPython] O_element059  label="O_element : 030"  # scripted group (container) (typed FeaturePython)
  n = 3
  ref = O_element
FEATURE [App::DocumentObjectGroupPython] G4_MAGNESIUM_CARBONATE  # scripted group (container) (typed FeaturePython)
  Dunit = g/cm3
  Dvalue = 2.958
  Group = -> [Mg_element005,C_element058,O_element059]
  conduct = 2
  density = 1
  expand = 3
  formula = G4_MAGNESIUM_CARBONATE
  name = G4_MAGNESIUM_CARBONATE
  specific = 4
FEATURE [App::DocumentObjectGroupPython] Mg_element006  label="Mg_element : 002"  # scripted group (container) (typed FeaturePython)
  n = 1
  ref = Mg_element
FEATURE [App::DocumentObjectGroupPython] F_element013  label="F_element : 005"  # scripted group (container) (typed FeaturePython)
  n = 2
  ref = F_element
FEATURE [App::DocumentObjectGroupPython] G4_MAGNESIUM_FLUORIDE  # scripted group (container) (typed FeaturePython)
  Dunit = g/cm3
  Dvalue = 3
  Group = -> [Mg_element006,F_element013]
  conduct = 2
  density = 1
  expand = 3
  formula = G4_MAGNESIUM_FLUORIDE
  name = G4_MAGNESIUM_FLUORIDE
  specific = 4
FEATURE [App::DocumentObjectGroupPython] Mg_element007  label="Mg_element : 003"  # scripted group (container) (typed FeaturePython)
  n = 1
  ref = Mg_element
FEATURE [App::DocumentObjectGroupPython] O_element060  label="O_element : 031"  # scripted group (container) (typed FeaturePython)
  n = 1
  ref = O_element
FEATURE [App::DocumentObjectGroupPython] G4_MAGNESIUM_OXIDE  # scripted group (container) (typed FeaturePython)
  Dunit = g/cm3
  Dvalue = 3.58
  Group = -> [Mg_element007,O_element060]
  conduct = 2
  density = 1
  expand = 3
  formula = G4_MAGNESIUM_OXIDE
  name = G4_MAGNESIUM_OXIDE
  specific = 4
FEATURE [App::DocumentObjectGroupPython] Mg_element008  label="Mg_element : 004"  # scripted group (container) (typed FeaturePython)
  n = 1
  ref = Mg_element
FEATURE [App::DocumentObjectGroupPython] B_element006  label="B_element : 006"  # scripted group (container) (typed FeaturePython)
  n = 4
  ref = B_element
FEATURE [App::DocumentObjectGroupPython] O_element061  label="O_element : 032"  # scripted group (container) (typed FeaturePython)
  n = 7
  ref = O_element
FEATURE [App::DocumentObjectGroupPython] G4_MAGNESIUM_TETRABORATE  # scripted group (container) (typed FeaturePython)
  Dunit = g/cm3
  Dvalue = 2.53
  Group = -> [Mg_element008,B_element006,O_element061]
  conduct = 2
  density = 1
  expand = 3
  formula = G4_MAGNESIUM_TETRABORATE
  name = G4_MAGNESIUM_TETRABORATE
  specific = 4
FEATURE [App::DocumentObjectGroupPython] Hg_element001  label="Hg_element : 1"  # scripted group (container) (typed FeaturePython)
  n = 1
  ref = Hg_element
FEATURE [App::DocumentObjectGroupPython] I_element004  label="I_element : 2"  # scripted group (container) (typed FeaturePython)
  n = 2
  ref = I_element
FEATURE [App::DocumentObjectGroupPython] G4_MERCURIC_IODIDE  # scripted group (container) (typed FeaturePython)
  Dunit = g/cm3
  Dvalue = 6.36
  Group = -> [Hg_element001,I_element004]
  conduct = 2
  density = 1
  expand = 3
  formula = G4_MERCURIC_IODIDE
  name = G4_MERCURIC_IODIDE
  specific = 4
FEATURE [App::DocumentObjectGroupPython] C_element059  label="C_element : 032"  # scripted group (container) (typed FeaturePython)
  n = 1
  ref = C_element
FEATURE [App::DocumentObjectGroupPython] H_element053  label="H_element : 028"  # scripted group (container) (typed FeaturePython)
  n = 4
  ref = H_element
FEATURE [App::DocumentObjectGroupPython] G4_METHANE  # scripted group (container) (typed FeaturePython)
  Dunit = g/cm3
  Dvalue = 0.000667151
  Group = -> [C_element059,H_element053]
  conduct = 2
  density = 1
  expand = 3
  formula = G4_METHANE
  name = G4_METHANE
  specific = 4
FEATURE [App::DocumentObjectGroupPython] C_element060  label="C_element : 033"  # scripted group (container) (typed FeaturePython)
  n = 1
  ref = C_element
FEATURE [App::DocumentObjectGroupPython] H_element054  label="H_element : 029"  # scripted group (container) (typed FeaturePython)
  n = 4
  ref = H_element
FEATURE [App::DocumentObjectGroupPython] O_element062  label="O_element : 033"  # scripted group (container) (typed FeaturePython)
  n = 1
  ref = O_element
FEATURE [App::DocumentObjectGroupPython] G4_METHANOL  # scripted group (container) (typed FeaturePython)
  Dunit = g/cm3
  Dvalue = 0.7914
  Group = -> [C_element060,H_element054,O_element062]
  conduct = 2
  density = 1
  expand = 3
  formula = G4_METHANOL
  name = G4_METHANOL
  specific = 4
FEATURE [App::DocumentObjectGroupPython] H_element055  label="H_element : 0.134"  # scripted group (container) (typed FeaturePython)
  n = 0.13404
FEATURE [App::DocumentObjectGroupPython] C_element061  label="C_element : 0.778"  # scripted group (container) (typed FeaturePython)
  n = 0.77796
FEATURE [App::DocumentObjectGroupPython] O_element063  label="O_element : 0.035"  # scripted group (container) (typed FeaturePython)
  n = 0.03502
FEATURE [App::DocumentObjectGroupPython] Mg_element009  label="Mg_element : 0.039"  # scripted group (container) (typed FeaturePython)
  n = 0.038594
FEATURE [App::DocumentObjectGroupPython] Ti_element002  label="Ti_element : 0.014"  # scripted group (container) (typed FeaturePython)
  n = 0.014386
FEATURE [App::DocumentObjectGroupPython] G4_MIX_D_WAX  # scripted group (container) (typed FeaturePython)
  Dunit = g/cm3
  Dvalue = 0.99
  Group = -> [H_element055,C_element061,O_element063,Mg_element009,Ti_element002]
  conduct = 2
  density = 1
  expand = 3
  formula = G4_MIX_D_WAX
  name = G4_MIX_D_WAX
  specific = 4
FEATURE [App::DocumentObjectGroupPython] H_element056  label="H_element : 0.135"  # scripted group (container) (typed FeaturePython)
  n = 0.081192
FEATURE [App::DocumentObjectGroupPython] C_element062  label="C_element : 0.583"  # scripted group (container) (typed FeaturePython)
  n = 0.583442
FEATURE [App::DocumentObjectGroupPython] N_element024  label="N_element : 0.018"  # scripted group (container) (typed FeaturePython)
  n = 0.017798
FEATURE [App::DocumentObjectGroupPython] O_element064  label="O_element : 0.186"  # scripted group (container) (typed FeaturePython)
  n = 0.186381
FEATURE [App::DocumentObjectGroupPython] Mg_element010  label="Mg_element : 0.130"  # scripted group (container) (typed FeaturePython)
  n = 0.130287
FEATURE [App::DocumentObjectGroupPython] Cl_element015  label="Cl_element : 0.588"  # scripted group (container) (typed FeaturePython)
  n = 0.0009
FEATURE [App::DocumentObjectGroupPython] G4_MS20_TISSUE  # scripted group (container) (typed FeaturePython)
  Dunit = g/cm3
  Dvalue = 1
  Group = -> [H_element056,C_element062,N_element024,O_element064,Mg_element010,Cl_element015]
  conduct = 2
  density = 1
  expand = 3
  formula = G4_MS20_TISSUE
  name = G4_MS20_TISSUE
  specific = 4
FEATURE [App::DocumentObjectGroupPython] H_element057  label="H_element : 0.136"  # scripted group (container) (typed FeaturePython)
  n = 0.102
FEATURE [App::DocumentObjectGroupPython] C_element063  label="C_element : 0.143"  # scripted group (container) (typed FeaturePython)
  n = 0.143
FEATURE [App::DocumentObjectGroupPython] N_element025  label="N_element : 0.034"  # scripted group (container) (typed FeaturePython)
  n = 0.034
FEATURE [App::DocumentObjectGroupPython] O_element065  label="O_element : 0.710"  # scripted group (container) (typed FeaturePython)
  n = 0.71
FEATURE [App::DocumentObjectGroupPython] Na_element011  label="Na_element : 0.098"  # scripted group (container) (typed FeaturePython)
  n = 0.001
FEATURE [App::DocumentObjectGroupPython] P_element007  label="P_element : 0.002"  # scripted group (container) (typed FeaturePython)
  n = 0.002
FEATURE [App::DocumentObjectGroupPython] S_element017  label="S_element : 0.018"  # scripted group (container) (typed FeaturePython)
  n = 0.003
FEATURE [App::DocumentObjectGroupPython] Cl_element016  label="Cl_element : 0.589"  # scripted group (container) (typed FeaturePython)
  n = 0.001
FEATURE [App::DocumentObjectGroupPython] K_element006  label="K_element : 0.004"  # scripted group (container) (typed FeaturePython)
  n = 0.004
FEATURE [App::DocumentObjectGroupPython] G4_MUSCLE_SKELETAL_ICRP  # scripted group (container) (typed FeaturePython)
  Dunit = g/cm3
  Dvalue = 1.05
  Group = -> [H_element057,C_element063,N_element025,O_element065,Na_element011,P_element007,S_element017,Cl_element016,K_element006]
  conduct = 2
  density = 1
  expand = 3
  formula = G4_MUSCLE_SKELETAL_ICRP
  name = G4_MUSCLE_SKELETAL_ICRP
  specific = 4
FEATURE [App::DocumentObjectGroupPython] H_element058  label="H_element : 0.137"  # scripted group (container) (typed FeaturePython)
  n = 0.102102
FEATURE [App::DocumentObjectGroupPython] C_element064  label="C_element : 0.123"  # scripted group (container) (typed FeaturePython)
  n = 0.123123
FEATURE [App::DocumentObjectGroupPython] N_element026  label="N_element : 0.756"  # scripted group (container) (typed FeaturePython)
  n = 0.035035
FEATURE [App::DocumentObjectGroupPython] O_element066  label="O_element : 0.730"  # scripted group (container) (typed FeaturePython)
  n = 0.72973
FEATURE [App::DocumentObjectGroupPython] Na_element012  label="Na_element : 0.099"  # scripted group (container) (typed FeaturePython)
  n = 0.001001
FEATURE [App::DocumentObjectGroupPython] P_element008  label="P_element : 0.106"  # scripted group (container) (typed FeaturePython)
  n = 0.002002
FEATURE [App::DocumentObjectGroupPython] S_element018  label="S_element : 0.019"  # scripted group (container) (typed FeaturePython)
  n = 0.004004
FEATURE [App::DocumentObjectGroupPython] K_element007  label="K_element : 0.016"  # scripted group (container) (typed FeaturePython)
  n = 0.003003
FEATURE [App::DocumentObjectGroupPython] G4_MUSCLE_STRIATED_ICRU  # scripted group (container) (typed FeaturePython)
  Dunit = g/cm3
  Dvalue = 1.04
  Group = -> [H_element058,C_element064,N_element026,O_element066,Na_element012,P_element008,S_element018,K_element007]
  conduct = 2
  density = 1
  expand = 3
  formula = G4_MUSCLE_STRIATED_ICRU
  name = G4_MUSCLE_STRIATED_ICRU
  specific = 4
FEATURE [App::DocumentObjectGroupPython] H_element059  label="H_element : 0.098"  # scripted group (container) (typed FeaturePython)
  n = 0.0982341
FEATURE [App::DocumentObjectGroupPython] C_element065  label="C_element : 0.156"  # scripted group (container) (typed FeaturePython)
  n = 0.156214
FEATURE [App::DocumentObjectGroupPython] N_element027  label="N_element : 0.757"  # scripted group (container) (typed FeaturePython)
  n = 0.035451
FEATURE [App::DocumentObjectGroupPython] O_element067  label="O_element : 0.880"  # scripted group (container) (typed FeaturePython)
  n = 0.710101
FEATURE [App::DocumentObjectGroupPython] G4_MUSCLE_WITH_SUCROSE  # scripted group (container) (typed FeaturePython)
  Dunit = g/cm3
  Dvalue = 1.11
  Group = -> [H_element059,C_element065,N_element027,O_element067]
  conduct = 2
  density = 1
  expand = 3
  formula = G4_MUSCLE_WITH_SUCROSE
  name = G4_MUSCLE_WITH_SUCROSE
  specific = 4
FEATURE [App::DocumentObjectGroupPython] H_element060  label="H_element : 0.138"  # scripted group (container) (typed FeaturePython)
  n = 0.101969
FEATURE [App::DocumentObjectGroupPython] C_element066  label="C_element : 0.120"  # scripted group (container) (typed FeaturePython)
  n = 0.120058
FEATURE [App::DocumentObjectGroupPython] N_element028  label="N_element : 0.758"  # scripted group (container) (typed FeaturePython)
  n = 0.035451
FEATURE [App::DocumentObjectGroupPython] O_element068  label="O_element : 0.743"  # scripted group (container) (typed FeaturePython)
  n = 0.742522
FEATURE [App::DocumentObjectGroupPython] G4_MUSCLE_WITHOUT_SUCROSE  # scripted group (container) (typed FeaturePython)
  Dunit = g/cm3
  Dvalue = 1.07
  Group = -> [H_element060,C_element066,N_element028,O_element068]
  conduct = 2
  density = 1
  expand = 3
  formula = G4_MUSCLE_WITHOUT_SUCROSE
  name = G4_MUSCLE_WITHOUT_SUCROSE
  specific = 4
FEATURE [App::DocumentObjectGroupPython] C_element067  label="C_element : 10"  # scripted group (container) (typed FeaturePython)
  n = 10
  ref = C_element
FEATURE [App::DocumentObjectGroupPython] H_element061  label="H_element : 030"  # scripted group (container) (typed FeaturePython)
  n = 8
  ref = H_element
FEATURE [App::DocumentObjectGroupPython] G4_NAPHTHALENE  # scripted group (container) (typed FeaturePython)
  Dunit = g/cm3
  Dvalue = 1.145
  Group = -> [C_element067,H_element061]
  conduct = 2
  density = 1
  expand = 3
  formula = G4_NAPHTHALENE
  name = G4_NAPHTHALENE
  specific = 4
FEATURE [App::DocumentObjectGroupPython] C_element068  label="C_element : 034"  # scripted group (container) (typed FeaturePython)
  n = 6
  ref = C_element
FEATURE [App::DocumentObjectGroupPython] H_element062  label="H_element : 031"  # scripted group (container) (typed FeaturePython)
  n = 5
  ref = H_element
FEATURE [App::DocumentObjectGroupPython] N_element029  label="N_element : 012"  # scripted group (container) (typed FeaturePython)
  n = 1
  ref = N_element
FEATURE [App::DocumentObjectGroupPython] O_element069  label="O_element : 034"  # scripted group (container) (typed FeaturePython)
  n = 2
  ref = O_element
FEATURE [App::DocumentObjectGroupPython] G4_NITROBENZENE  # scripted group (container) (typed FeaturePython)
  Dunit = g/cm3
  Dvalue = 1.19867
  Group = -> [C_element068,H_element062,N_element029,O_element069]
  conduct = 2
  density = 1
  expand = 3
  formula = G4_NITROBENZENE
  name = G4_NITROBENZENE
  specific = 4
FEATURE [App::DocumentObjectGroupPython] N_element030  label="N_element : 013"  # scripted group (container) (typed FeaturePython)
  n = 2
  ref = N_element
FEATURE [App::DocumentObjectGroupPython] O_element070  label="O_element : 035"  # scripted group (container) (typed FeaturePython)
  n = 1
  ref = O_element
FEATURE [App::DocumentObjectGroupPython] G4_NITROUS_OXIDE  # scripted group (container) (typed FeaturePython)
  Dunit = g/cm3
  Dvalue = 0.00183094
  Group = -> [N_element030,O_element070]
  conduct = 2
  density = 1
  expand = 3
  formula = G4_NITROUS_OXIDE
  name = G4_NITROUS_OXIDE
  specific = 4
FEATURE [App::DocumentObjectGroupPython] H_element063  label="H_element : 0.104"  # scripted group (container) (typed FeaturePython)
  n = 0.103509
FEATURE [App::DocumentObjectGroupPython] C_element069  label="C_element : 0.648"  # scripted group (container) (typed FeaturePython)
  n = 0.648416
FEATURE [App::DocumentObjectGroupPython] N_element031  label="N_element : 0.100"  # scripted group (container) (typed FeaturePython)
  n = 0.0995361
FEATURE [App::DocumentObjectGroupPython] O_element071  label="O_element : 0.149"  # scripted group (container) (typed FeaturePython)
  n = 0.148539
FEATURE [App::DocumentObjectGroupPython] G4_NYLON_8062  label="G4_NYLON-8062"  # scripted group (container) (typed FeaturePython)
  Dunit = g/cm3
  Dvalue = 1.08
  Group = -> [H_element063,C_element069,N_element031,O_element071]
  conduct = 2
  density = 1
  expand = 3
  formula = G4_NYLON-8062
  name = G4_NYLON-8062
  specific = 4
FEATURE [App::DocumentObjectGroupPython] C_element070  label="C_element : 035"  # scripted group (container) (typed FeaturePython)
  n = 6
  ref = C_element
FEATURE [App::DocumentObjectGroupPython] H_element064  label="H_element : 11"  # scripted group (container) (typed FeaturePython)
  n = 11
  ref = H_element
FEATURE [App::DocumentObjectGroupPython] N_element032  label="N_element : 014"  # scripted group (container) (typed FeaturePython)
  n = 1
  ref = N_element
FEATURE [App::DocumentObjectGroupPython] O_element072  label="O_element : 036"  # scripted group (container) (typed FeaturePython)
  n = 1
  ref = O_element
FEATURE [App::DocumentObjectGroupPython] G4_NYLON_6_6  label="G4_NYLON-6-6"  # scripted group (container) (typed FeaturePython)
  Dunit = g/cm3
  Dvalue = 1.14
  Group = -> [C_element070,H_element064,N_element032,O_element072]
  conduct = 2
  density = 1
  expand = 3
  formula = G4_NYLON-6-6
  name = G4_NYLON-6-6
  specific = 4
FEATURE [App::DocumentObjectGroupPython] H_element065  label="H_element : 0.139"  # scripted group (container) (typed FeaturePython)
  n = 0.107062
FEATURE [App::DocumentObjectGroupPython] C_element071  label="C_element : 0.680"  # scripted group (container) (typed FeaturePython)
  n = 0.680449
FEATURE [App::DocumentObjectGroupPython] N_element033  label="N_element : 0.099"  # scripted group (container) (typed FeaturePython)
  n = 0.099189
FEATURE [App::DocumentObjectGroupPython] O_element073  label="O_element : 0.113"  # scripted group (container) (typed FeaturePython)
  n = 0.1133
FEATURE [App::DocumentObjectGroupPython] G4_NYLON_6_10  label="G4_NYLON-6-10"  # scripted group (container) (typed FeaturePython)
  Dunit = g/cm3
  Dvalue = 1.14
  Group = -> [H_element065,C_element071,N_element033,O_element073]
  conduct = 2
  density = 1
  expand = 3
  formula = G4_NYLON-6-10
  name = G4_NYLON-6-10
  specific = 4
FEATURE [App::DocumentObjectGroupPython] H_element066  label="H_element : 0.140"  # scripted group (container) (typed FeaturePython)
  n = 0.115476
FEATURE [App::DocumentObjectGroupPython] C_element072  label="C_element : 0.721"  # scripted group (container) (typed FeaturePython)
  n = 0.720818
FEATURE [App::DocumentObjectGroupPython] N_element034  label="N_element : 0.076"  # scripted group (container) (typed FeaturePython)
  n = 0.0764169
FEATURE [App::DocumentObjectGroupPython] O_element074  label="O_element : 0.087"  # scripted group (container) (typed FeaturePython)
  n = 0.0872889
FEATURE [App::DocumentObjectGroupPython] G4_NYLON_11_RILSAN  label="G4_NYLON-11_RILSAN"  # scripted group (container) (typed FeaturePython)
  Dunit = g/cm3
  Dvalue = 1.425
  Group = -> [H_element066,C_element072,N_element034,O_element074]
  conduct = 2
  density = 1
  expand = 3
  formula = G4_NYLON-11_RILSAN
  name = G4_NYLON-11_RILSAN
  specific = 4
FEATURE [App::DocumentObjectGroupPython] C_element073  label="C_element : 8"  # scripted group (container) (typed FeaturePython)
  n = 8
  ref = C_element
FEATURE [App::DocumentObjectGroupPython] H_element067  label="H_element : 18"  # scripted group (container) (typed FeaturePython)
  n = 18
  ref = H_element
FEATURE [App::DocumentObjectGroupPython] G4_OCTANE  # scripted group (container) (typed FeaturePython)
  Dunit = g/cm3
  Dvalue = 0.7026
  Group = -> [C_element073,H_element067]
  conduct = 2
  density = 1
  expand = 3
  formula = G4_OCTANE
  name = G4_OCTANE
  specific = 4
FEATURE [App::DocumentObjectGroupPython] C_element074  label="C_element : 25"  # scripted group (container) (typed FeaturePython)
  n = 25
  ref = C_element
FEATURE [App::DocumentObjectGroupPython] H_element068  label="H_element : 52"  # scripted group (container) (typed FeaturePython)
  n = 52
  ref = H_element
FEATURE [App::DocumentObjectGroupPython] G4_PARAFFIN  # scripted group (container) (typed FeaturePython)
  Dunit = g/cm3
  Dvalue = 0.93
  Group = -> [C_element074,H_element068]
  conduct = 2
  density = 1
  expand = 3
  formula = G4_PARAFFIN
  name = G4_PARAFFIN
  specific = 4
FEATURE [App::DocumentObjectGroupPython] C_element075  label="C_element : 036"  # scripted group (container) (typed FeaturePython)
  n = 5
  ref = C_element
FEATURE [App::DocumentObjectGroupPython] H_element069  label="H_element : 032"  # scripted group (container) (typed FeaturePython)
  n = 12
  ref = H_element
FEATURE [App::DocumentObjectGroupPython] G4_N_PENTANE  label="G4_N-PENTANE"  # scripted group (container) (typed FeaturePython)
  Dunit = g/cm3
  Dvalue = 0.6262
  Group = -> [C_element075,H_element069]
  conduct = 2
  density = 1
  expand = 3
  formula = G4_N-PENTANE
  name = G4_N-PENTANE
  specific = 4
FEATURE [App::DocumentObjectGroupPython] H_element070  label="H_element : 0.014"  # scripted group (container) (typed FeaturePython)
  n = 0.0141
FEATURE [App::DocumentObjectGroupPython] C_element076  label="C_element : 0.072"  # scripted group (container) (typed FeaturePython)
  n = 0.072261
FEATURE [App::DocumentObjectGroupPython] N_element035  label="N_element : 0.019"  # scripted group (container) (typed FeaturePython)
  n = 0.01932
FEATURE [App::DocumentObjectGroupPython] O_element075  label="O_element : 0.066"  # scripted group (container) (typed FeaturePython)
  n = 0.066101
FEATURE [App::DocumentObjectGroupPython] S_element019  label="S_element : 0.020"  # scripted group (container) (typed FeaturePython)
  n = 0.00189
FEATURE [App::DocumentObjectGroupPython] Br_element004  label="Br_element : 0.349"  # scripted group (container) (typed FeaturePython)
  n = 0.349103
FEATURE [App::DocumentObjectGroupPython] Ag_element001  label="Ag_element : 0.474"  # scripted group (container) (typed FeaturePython)
  n = 0.474105
FEATURE [App::DocumentObjectGroupPython] I_element005  label="I_element : 0.003"  # scripted group (container) (typed FeaturePython)
  n = 0.00312
FEATURE [App::DocumentObjectGroupPython] G4_PHOTO_EMULSION  # scripted group (container) (typed FeaturePython)
  Dunit = g/cm3
  Dvalue = 3.815
  Group = -> [H_element070,C_element076,N_element035,O_element075,S_element019,Br_element004,Ag_element001,I_element005]
  conduct = 2
  density = 1
  expand = 3
  formula = G4_PHOTO_EMULSION
  name = G4_PHOTO_EMULSION
  specific = 4
FEATURE [App::DocumentObjectGroupPython] C_element077  label="C_element : 9"  # scripted group (container) (typed FeaturePython)
  n = 9
  ref = C_element
FEATURE [App::DocumentObjectGroupPython] H_element071  label="H_element : 033"  # scripted group (container) (typed FeaturePython)
  n = 10
  ref = H_element
FEATURE [App::DocumentObjectGroupPython] G4_PLASTIC_SC_VINYLTOLUENE  # scripted group (container) (typed FeaturePython)
  Dunit = g/cm3
  Dvalue = 1.032
  Group = -> [C_element077,H_element071]
  conduct = 2
  density = 1
  expand = 3
  formula = G4_PLASTIC_SC_VINYLTOLUENE
  name = G4_PLASTIC_SC_VINYLTOLUENE
  specific = 4
FEATURE [App::DocumentObjectGroupPython] Pu_element001  label="Pu_element : 1"  # scripted group (container) (typed FeaturePython)
  n = 1
  ref = Pu_element
FEATURE [App::DocumentObjectGroupPython] O_element076  label="O_element : 037"  # scripted group (container) (typed FeaturePython)
  n = 2
  ref = O_element
FEATURE [App::DocumentObjectGroupPython] G4_PLUTONIUM_DIOXIDE  # scripted group (container) (typed FeaturePython)
  Dunit = g/cm3
  Dvalue = 11.46
  Group = -> [Pu_element001,O_element076]
  conduct = 2
  density = 1
  expand = 3
  formula = G4_PLUTONIUM_DIOXIDE
  name = G4_PLUTONIUM_DIOXIDE
  specific = 4
FEATURE [App::DocumentObjectGroupPython] C_element078  label="C_element : 037"  # scripted group (container) (typed FeaturePython)
  n = 3
  ref = C_element
FEATURE [App::DocumentObjectGroupPython] H_element072  label="H_element : 034"  # scripted group (container) (typed FeaturePython)
  n = 3
  ref = H_element
FEATURE [App::DocumentObjectGroupPython] N_element036  label="N_element : 015"  # scripted group (container) (typed FeaturePython)
  n = 1
  ref = N_element
FEATURE [App::DocumentObjectGroupPython] G4_POLYACRYLONITRILE  # scripted group (container) (typed FeaturePython)
  Dunit = g/cm3
  Dvalue = 1.17
  Group = -> [C_element078,H_element072,N_element036]
  conduct = 2
  density = 1
  expand = 3
  formula = G4_POLYACRYLONITRILE
  name = G4_POLYACRYLONITRILE
  specific = 4
FEATURE [App::DocumentObjectGroupPython] C_element079  label="C_element : 16"  # scripted group (container) (typed FeaturePython)
  n = 16
  ref = C_element
FEATURE [App::DocumentObjectGroupPython] H_element073  label="H_element : 035"  # scripted group (container) (typed FeaturePython)
  n = 14
  ref = H_element
FEATURE [App::DocumentObjectGroupPython] O_element077  label="O_element : 038"  # scripted group (container) (typed FeaturePython)
  n = 3
  ref = O_element
FEATURE [App::DocumentObjectGroupPython] G4_POLYCARBONATE  # scripted group (container) (typed FeaturePython)
  Dunit = g/cm3
  Dvalue = 1.2
  Group = -> [C_element079,H_element073,O_element077]
  conduct = 2
  density = 1
  expand = 3
  formula = G4_POLYCARBONATE
  name = G4_POLYCARBONATE
  specific = 4
FEATURE [App::DocumentObjectGroupPython] C_element080  label="C_element : 038"  # scripted group (container) (typed FeaturePython)
  n = 8
  ref = C_element
FEATURE [App::DocumentObjectGroupPython] H_element074  label="H_element : 036"  # scripted group (container) (typed FeaturePython)
  n = 7
  ref = H_element
FEATURE [App::DocumentObjectGroupPython] Cl_element017  label="Cl_element : 007"  # scripted group (container) (typed FeaturePython)
  n = 1
  ref = Cl_element
FEATURE [App::DocumentObjectGroupPython] G4_POLYCHLOROSTYRENE  # scripted group (container) (typed FeaturePython)
  Dunit = g/cm3
  Dvalue = 1.3
  Group = -> [C_element080,H_element074,Cl_element017]
  conduct = 2
  density = 1
  expand = 3
  formula = G4_POLYCHLOROSTYRENE
  name = G4_POLYCHLOROSTYRENE
  specific = 4
FEATURE [App::DocumentObjectGroupPython] C_element081  label="C_element : 039"  # scripted group (container) (typed FeaturePython)
  n = 1
  ref = C_element
FEATURE [App::DocumentObjectGroupPython] H_element075  label="H_element : 037"  # scripted group (container) (typed FeaturePython)
  n = 2
  ref = H_element
FEATURE [App::DocumentObjectGroupPython] G4_POLYETHYLENE  # scripted group (container) (typed FeaturePython)
  Dunit = g/cm3
  Dvalue = 0.94
  Group = -> [C_element081,H_element075]
  conduct = 2
  density = 1
  expand = 3
  formula = G4_POLYETHYLENE
  name = G4_POLYETHYLENE
  specific = 4
FEATURE [App::DocumentObjectGroupPython] C_element082  label="C_element : 040"  # scripted group (container) (typed FeaturePython)
  n = 10
  ref = C_element
FEATURE [App::DocumentObjectGroupPython] H_element076  label="H_element : 038"  # scripted group (container) (typed FeaturePython)
  n = 8
  ref = H_element
FEATURE [App::DocumentObjectGroupPython] O_element078  label="O_element : 039"  # scripted group (container) (typed FeaturePython)
  n = 4
  ref = O_element
FEATURE [App::DocumentObjectGroupPython] G4_MYLAR  # scripted group (container) (typed FeaturePython)
  Dunit = g/cm3
  Dvalue = 1.4
  Group = -> [C_element082,H_element076,O_element078]
  conduct = 2
  density = 1
  expand = 3
  formula = G4_MYLAR
  name = G4_MYLAR
  specific = 4
FEATURE [App::DocumentObjectGroupPython] C_element083  label="C_element : 041"  # scripted group (container) (typed FeaturePython)
  n = 5
  ref = C_element
FEATURE [App::DocumentObjectGroupPython] H_element077  label="H_element : 039"  # scripted group (container) (typed FeaturePython)
  n = 8
  ref = H_element
FEATURE [App::DocumentObjectGroupPython] O_element079  label="O_element : 040"  # scripted group (container) (typed FeaturePython)
  n = 2
  ref = O_element
FEATURE [App::DocumentObjectGroupPython] G4_PLEXIGLASS  # scripted group (container) (typed FeaturePython)
  Dunit = g/cm3
  Dvalue = 1.19
  Group = -> [C_element083,H_element077,O_element079]
  conduct = 2
  density = 1
  expand = 3
  formula = G4_PLEXIGLASS
  name = G4_PLEXIGLASS
  specific = 4
FEATURE [App::DocumentObjectGroupPython] C_element084  label="C_element : 042"  # scripted group (container) (typed FeaturePython)
  n = 1
  ref = C_element
FEATURE [App::DocumentObjectGroupPython] H_element078  label="H_element : 040"  # scripted group (container) (typed FeaturePython)
  n = 2
  ref = H_element
FEATURE [App::DocumentObjectGroupPython] O_element080  label="O_element : 041"  # scripted group (container) (typed FeaturePython)
  n = 1
  ref = O_element
FEATURE [App::DocumentObjectGroupPython] G4_POLYOXYMETHYLENE  # scripted group (container) (typed FeaturePython)
  Dunit = g/cm3
  Dvalue = 1.425
  Group = -> [C_element084,H_element078,O_element080]
  conduct = 2
  density = 1
  expand = 3
  formula = G4_POLYOXYMETHYLENE
  name = G4_POLYOXYMETHYLENE
  specific = 4
FEATURE [App::DocumentObjectGroupPython] C_element085  label="C_element : 043"  # scripted group (container) (typed FeaturePython)
  n = 2
  ref = C_element
FEATURE [App::DocumentObjectGroupPython] H_element079  label="H_element : 041"  # scripted group (container) (typed FeaturePython)
  n = 4
  ref = H_element
FEATURE [App::DocumentObjectGroupPython] G4_POLYPROPYLENE  # scripted group (container) (typed FeaturePython)
  Dunit = g/cm3
  Dvalue = 0.9
  Group = -> [C_element085,H_element079]
  conduct = 2
  density = 1
  expand = 3
  formula = G4_POLYPROPYLENE
  name = G4_POLYPROPYLENE
  specific = 4
FEATURE [App::DocumentObjectGroupPython] C_element086  label="C_element : 044"  # scripted group (container) (typed FeaturePython)
  n = 8
  ref = C_element
FEATURE [App::DocumentObjectGroupPython] H_element080  label="H_element : 042"  # scripted group (container) (typed FeaturePython)
  n = 8
  ref = H_element
FEATURE [App::DocumentObjectGroupPython] G4_POLYSTYRENE  # scripted group (container) (typed FeaturePython)
  Dunit = g/cm3
  Dvalue = 1.06
  Group = -> [C_element086,H_element080]
  conduct = 2
  density = 1
  expand = 3
  formula = G4_POLYSTYRENE
  name = G4_POLYSTYRENE
  specific = 4
FEATURE [App::DocumentObjectGroupPython] C_element087  label="C_element : 045"  # scripted group (container) (typed FeaturePython)
  n = 2
  ref = C_element
FEATURE [App::DocumentObjectGroupPython] F_element014  label="F_element : 4"  # scripted group (container) (typed FeaturePython)
  n = 4
  ref = F_element
FEATURE [App::DocumentObjectGroupPython] G4_TEFLON  # scripted group (container) (typed FeaturePython)
  Dunit = g/cm3
  Dvalue = 2.2
  Group = -> [C_element087,F_element014]
  conduct = 2
  density = 1
  expand = 3
  formula = G4_TEFLON
  name = G4_TEFLON
  specific = 4
FEATURE [App::DocumentObjectGroupPython] C_element088  label="C_element : 046"  # scripted group (container) (typed FeaturePython)
  n = 2
  ref = C_element
FEATURE [App::DocumentObjectGroupPython] F_element015  label="F_element : 006"  # scripted group (container) (typed FeaturePython)
  n = 3
  ref = F_element
FEATURE [App::DocumentObjectGroupPython] Cl_element018  label="Cl_element : 008"  # scripted group (container) (typed FeaturePython)
  n = 1
  ref = Cl_element
FEATURE [App::DocumentObjectGroupPython] G4_POLYTRIFLUOROCHLOROETHYLENE  # scripted group (container) (typed FeaturePython)
  Dunit = g/cm3
  Dvalue = 2.1
  Group = -> [C_element088,F_element015,Cl_element018]
  conduct = 2
  density = 1
  expand = 3
  formula = G4_POLYTRIFLUOROCHLOROETHYLENE
  name = G4_POLYTRIFLUOROCHLOROETHYLENE
  specific = 4
FEATURE [App::DocumentObjectGroupPython] C_element089  label="C_element : 047"  # scripted group (container) (typed FeaturePython)
  n = 4
  ref = C_element
FEATURE [App::DocumentObjectGroupPython] H_element081  label="H_element : 043"  # scripted group (container) (typed FeaturePython)
  n = 6
  ref = H_element
FEATURE [App::DocumentObjectGroupPython] O_element081  label="O_element : 042"  # scripted group (container) (typed FeaturePython)
  n = 2
  ref = O_element
FEATURE [App::DocumentObjectGroupPython] G4_POLYVINYL_ACETATE  # scripted group (container) (typed FeaturePython)
  Dunit = g/cm3
  Dvalue = 1.19
  Group = -> [C_element089,H_element081,O_element081]
  conduct = 2
  density = 1
  expand = 3
  formula = G4_POLYVINYL_ACETATE
  name = G4_POLYVINYL_ACETATE
  specific = 4
FEATURE [App::DocumentObjectGroupPython] C_element090  label="C_element : 048"  # scripted group (container) (typed FeaturePython)
  n = 2
  ref = C_element
FEATURE [App::DocumentObjectGroupPython] H_element082  label="H_element : 044"  # scripted group (container) (typed FeaturePython)
  n = 4
  ref = H_element
FEATURE [App::DocumentObjectGroupPython] O_element082  label="O_element : 043"  # scripted group (container) (typed FeaturePython)
  n = 1
  ref = O_element
FEATURE [App::DocumentObjectGroupPython] G4_POLYVINYL_ALCOHOL  # scripted group (container) (typed FeaturePython)
  Dunit = g/cm3
  Dvalue = 1.3
  Group = -> [C_element090,H_element082,O_element082]
  conduct = 2
  density = 1
  expand = 3
  formula = G4_POLYVINYL_ALCOHOL
  name = G4_POLYVINYL_ALCOHOL
  specific = 4
FEATURE [App::DocumentObjectGroupPython] C_element091  label="C_element : 049"  # scripted group (container) (typed FeaturePython)
  n = 8
  ref = C_element
FEATURE [App::DocumentObjectGroupPython] H_element083  label="H_element : 045"  # scripted group (container) (typed FeaturePython)
  n = 14
  ref = H_element
FEATURE [App::DocumentObjectGroupPython] O_element083  label="O_element : 044"  # scripted group (container) (typed FeaturePython)
  n = 2
  ref = O_element
FEATURE [App::DocumentObjectGroupPython] G4_POLYVINYL_BUTYRAL  # scripted group (container) (typed FeaturePython)
  Dunit = g/cm3
  Dvalue = 1.12
  Group = -> [C_element091,H_element083,O_element083]
  conduct = 2
  density = 1
  expand = 3
  formula = G4_POLYVINYL_BUTYRAL
  name = G4_POLYVINYL_BUTYRAL
  specific = 4
FEATURE [App::DocumentObjectGroupPython] C_element092  label="C_element : 050"  # scripted group (container) (typed FeaturePython)
  n = 2
  ref = C_element
FEATURE [App::DocumentObjectGroupPython] H_element084  label="H_element : 046"  # scripted group (container) (typed FeaturePython)
  n = 3
  ref = H_element
FEATURE [App::DocumentObjectGroupPython] Cl_element019  label="Cl_element : 009"  # scripted group (container) (typed FeaturePython)
  n = 1
  ref = Cl_element
FEATURE [App::DocumentObjectGroupPython] G4_POLYVINYL_CHLORIDE  # scripted group (container) (typed FeaturePython)
  Dunit = g/cm3
  Dvalue = 1.3
  Group = -> [C_element092,H_element084,Cl_element019]
  conduct = 2
  density = 1
  expand = 3
  formula = G4_POLYVINYL_CHLORIDE
  name = G4_POLYVINYL_CHLORIDE
  specific = 4
FEATURE [App::DocumentObjectGroupPython] C_element093  label="C_element : 051"  # scripted group (container) (typed FeaturePython)
  n = 2
  ref = C_element
FEATURE [App::DocumentObjectGroupPython] H_element085  label="H_element : 047"  # scripted group (container) (typed FeaturePython)
  n = 2
  ref = H_element
FEATURE [App::DocumentObjectGroupPython] Cl_element020  label="Cl_element : 010"  # scripted group (container) (typed FeaturePython)
  n = 2
  ref = Cl_element
FEATURE [App::DocumentObjectGroupPython] G4_POLYVINYLIDENE_CHLORIDE  # scripted group (container) (typed FeaturePython)
  Dunit = g/cm3
  Dvalue = 1.7
  Group = -> [C_element093,H_element085,Cl_element020]
  conduct = 2
  density = 1
  expand = 3
  formula = G4_POLYVINYLIDENE_CHLORIDE
  name = G4_POLYVINYLIDENE_CHLORIDE
  specific = 4
FEATURE [App::DocumentObjectGroupPython] C_element094  label="C_element : 052"  # scripted group (container) (typed FeaturePython)
  n = 2
  ref = C_element
FEATURE [App::DocumentObjectGroupPython] H_element086  label="H_element : 048"  # scripted group (container) (typed FeaturePython)
  n = 2
  ref = H_element
FEATURE [App::DocumentObjectGroupPython] F_element016  label="F_element : 007"  # scripted group (container) (typed FeaturePython)
  n = 2
  ref = F_element
FEATURE [App::DocumentObjectGroupPython] G4_POLYVINYLIDENE_FLUORIDE  # scripted group (container) (typed FeaturePython)
  Dunit = g/cm3
  Dvalue = 1.76
  Group = -> [C_element094,H_element086,F_element016]
  conduct = 2
  density = 1
  expand = 3
  formula = G4_POLYVINYLIDENE_FLUORIDE
  name = G4_POLYVINYLIDENE_FLUORIDE
  specific = 4
FEATURE [App::DocumentObjectGroupPython] C_element095  label="C_element : 053"  # scripted group (container) (typed FeaturePython)
  n = 6
  ref = C_element
FEATURE [App::DocumentObjectGroupPython] H_element087  label="H_element : 9"  # scripted group (container) (typed FeaturePython)
  n = 9
  ref = H_element
FEATURE [App::DocumentObjectGroupPython] N_element037  label="N_element : 016"  # scripted group (container) (typed FeaturePython)
  n = 1
  ref = N_element
FEATURE [App::DocumentObjectGroupPython] O_element084  label="O_element : 045"  # scripted group (container) (typed FeaturePython)
  n = 1
  ref = O_element
FEATURE [App::DocumentObjectGroupPython] G4_POLYVINYL_PYRROLIDONE  # scripted group (container) (typed FeaturePython)
  Dunit = g/cm3
  Dvalue = 1.25
  Group = -> [C_element095,H_element087,N_element037,O_element084]
  conduct = 2
  density = 1
  expand = 3
  formula = G4_POLYVINYL_PYRROLIDONE
  name = G4_POLYVINYL_PYRROLIDONE
  specific = 4
FEATURE [App::DocumentObjectGroupPython] K_element008  label="K_element : 1"  # scripted group (container) (typed FeaturePython)
  n = 1
  ref = K_element
FEATURE [App::DocumentObjectGroupPython] I_element006  label="I_element : 003"  # scripted group (container) (typed FeaturePython)
  n = 1
  ref = I_element
FEATURE [App::DocumentObjectGroupPython] G4_POTASSIUM_IODIDE  # scripted group (container) (typed FeaturePython)
  Dunit = g/cm3
  Dvalue = 3.13
  Group = -> [K_element008,I_element006]
  conduct = 2
  density = 1
  expand = 3
  formula = G4_POTASSIUM_IODIDE
  name = G4_POTASSIUM_IODIDE
  specific = 4
FEATURE [App::DocumentObjectGroupPython] K_element009  label="K_element : 2"  # scripted group (container) (typed FeaturePython)
  n = 2
  ref = K_element
FEATURE [App::DocumentObjectGroupPython] O_element085  label="O_element : 046"  # scripted group (container) (typed FeaturePython)
  n = 1
  ref = O_element
FEATURE [App::DocumentObjectGroupPython] G4_POTASSIUM_OXIDE  # scripted group (container) (typed FeaturePython)
  Dunit = g/cm3
  Dvalue = 2.32
  Group = -> [K_element009,O_element085]
  conduct = 2
  density = 1
  expand = 3
  formula = G4_POTASSIUM_OXIDE
  name = G4_POTASSIUM_OXIDE
  specific = 4
FEATURE [App::DocumentObjectGroupPython] C_element096  label="C_element : 054"  # scripted group (container) (typed FeaturePython)
  n = 3
  ref = C_element
FEATURE [App::DocumentObjectGroupPython] H_element088  label="H_element : 049"  # scripted group (container) (typed FeaturePython)
  n = 8
  ref = H_element
FEATURE [App::DocumentObjectGroupPython] G4_PROPANE  # scripted group (container) (typed FeaturePython)
  Dunit = g/cm3
  Dvalue = 0.00187939
  Group = -> [C_element096,H_element088]
  conduct = 2
  density = 1
  expand = 3
  formula = G4_PROPANE
  name = G4_PROPANE
  specific = 4
FEATURE [App::DocumentObjectGroupPython] C_element097  label="C_element : 055"  # scripted group (container) (typed FeaturePython)
  n = 3
  ref = C_element
FEATURE [App::DocumentObjectGroupPython] H_element089  label="H_element : 050"  # scripted group (container) (typed FeaturePython)
  n = 8
  ref = H_element
FEATURE [App::DocumentObjectGroupPython] G4_lPROPANE  # scripted group (container) (typed FeaturePython)
  Dunit = g/cm3
  Dvalue = 0.43
  Group = -> [C_element097,H_element089]
  conduct = 2
  density = 1
  expand = 3
  formula = G4_lPROPANE
  name = G4_lPROPANE
  specific = 4
FEATURE [App::DocumentObjectGroupPython] C_element098  label="C_element : 056"  # scripted group (container) (typed FeaturePython)
  n = 3
  ref = C_element
FEATURE [App::DocumentObjectGroupPython] H_element090  label="H_element : 051"  # scripted group (container) (typed FeaturePython)
  n = 8
  ref = H_element
FEATURE [App::DocumentObjectGroupPython] O_element086  label="O_element : 047"  # scripted group (container) (typed FeaturePython)
  n = 1
  ref = O_element
FEATURE [App::DocumentObjectGroupPython] G4_N_PROPYL_ALCOHOL  label="G4_N-PROPYL_ALCOHOL"  # scripted group (container) (typed FeaturePython)
  Dunit = g/cm3
  Dvalue = 0.8035
  Group = -> [C_element098,H_element090,O_element086]
  conduct = 2
  density = 1
  expand = 3
  formula = G4_N-PROPYL_ALCOHOL
  name = G4_N-PROPYL_ALCOHOL
  specific = 4
FEATURE [App::DocumentObjectGroupPython] C_element099  label="C_element : 057"  # scripted group (container) (typed FeaturePython)
  n = 5
  ref = C_element
FEATURE [App::DocumentObjectGroupPython] H_element091  label="H_element : 052"  # scripted group (container) (typed FeaturePython)
  n = 5
  ref = H_element
FEATURE [App::DocumentObjectGroupPython] N_element038  label="N_element : 017"  # scripted group (container) (typed FeaturePython)
  n = 1
  ref = N_element
FEATURE [App::DocumentObjectGroupPython] G4_PYRIDINE  # scripted group (container) (typed FeaturePython)
  Dunit = g/cm3
  Dvalue = 0.9819
  Group = -> [C_element099,H_element091,N_element038]
  conduct = 2
  density = 1
  expand = 3
  formula = G4_PYRIDINE
  name = G4_PYRIDINE
  specific = 4
FEATURE [App::DocumentObjectGroupPython] H_element092  label="H_element : 0.144"  # scripted group (container) (typed FeaturePython)
  n = 0.143711
FEATURE [App::DocumentObjectGroupPython] C_element100  label="C_element : 0.856"  # scripted group (container) (typed FeaturePython)
  n = 0.856289
FEATURE [App::DocumentObjectGroupPython] G4_RUBBER_BUTYL  # scripted group (container) (typed FeaturePython)
  Dunit = g/cm3
  Dvalue = 0.92
  Group = -> [H_element092,C_element100]
  conduct = 2
  density = 1
  expand = 3
  formula = G4_RUBBER_BUTYL
  name = G4_RUBBER_BUTYL
  specific = 4
FEATURE [App::DocumentObjectGroupPython] H_element093  label="H_element : 0.118"  # scripted group (container) (typed FeaturePython)
  n = 0.118371
FEATURE [App::DocumentObjectGroupPython] C_element101  label="C_element : 0.882"  # scripted group (container) (typed FeaturePython)
  n = 0.881629
FEATURE [App::DocumentObjectGroupPython] G4_RUBBER_NATURAL  # scripted group (container) (typed FeaturePython)
  Dunit = g/cm3
  Dvalue = 0.92
  Group = -> [H_element093,C_element101]
  conduct = 2
  density = 1
  expand = 3
  formula = G4_RUBBER_NATURAL
  name = G4_RUBBER_NATURAL
  specific = 4
FEATURE [App::DocumentObjectGroupPython] H_element094  label="H_element : 0.145"  # scripted group (container) (typed FeaturePython)
  n = 0.05692
FEATURE [App::DocumentObjectGroupPython] C_element102  label="C_element : 0.543"  # scripted group (container) (typed FeaturePython)
  n = 0.542646
FEATURE [App::DocumentObjectGroupPython] Cl_element021  label="Cl_element : 0.400"  # scripted group (container) (typed FeaturePython)
  n = 0.400434
FEATURE [App::DocumentObjectGroupPython] G4_RUBBER_NEOPRENE  # scripted group (container) (typed FeaturePython)
  Dunit = g/cm3
  Dvalue = 1.23
  Group = -> [H_element094,C_element102,Cl_element021]
  conduct = 2
  density = 1
  expand = 3
  formula = G4_RUBBER_NEOPRENE
  name = G4_RUBBER_NEOPRENE
  specific = 4
FEATURE [App::DocumentObjectGroupPython] Si_element006  label="Si_element : 1"  # scripted group (container) (typed FeaturePython)
  n = 1
  ref = Si_element
FEATURE [App::DocumentObjectGroupPython] O_element087  label="O_element : 048"  # scripted group (container) (typed FeaturePython)
  n = 2
  ref = O_element
FEATURE [App::DocumentObjectGroupPython] G4_SILICON_DIOXIDE  # scripted group (container) (typed FeaturePython)
  Dunit = g/cm3
  Dvalue = 2.32
  Group = -> [Si_element006,O_element087]
  conduct = 2
  density = 1
  expand = 3
  formula = G4_SILICON_DIOXIDE
  name = G4_SILICON_DIOXIDE
  specific = 4
FEATURE [App::DocumentObjectGroupPython] Ag_element002  label="Ag_element : 1"  # scripted group (container) (typed FeaturePython)
  n = 1
  ref = Ag_element
FEATURE [App::DocumentObjectGroupPython] Br_element005  label="Br_element : 003"  # scripted group (container) (typed FeaturePython)
  n = 1
  ref = Br_element
FEATURE [App::DocumentObjectGroupPython] G4_SILVER_BROMIDE  # scripted group (container) (typed FeaturePython)
  Dunit = g/cm3
  Dvalue = 6.473
  Group = -> [Ag_element002,Br_element005]
  conduct = 2
  density = 1
  expand = 3
  formula = G4_SILVER_BROMIDE
  name = G4_SILVER_BROMIDE
  specific = 4
FEATURE [App::DocumentObjectGroupPython] Ag_element003  label="Ag_element : 002"  # scripted group (container) (typed FeaturePython)
  n = 1
  ref = Ag_element
FEATURE [App::DocumentObjectGroupPython] Cl_element022  label="Cl_element : 011"  # scripted group (container) (typed FeaturePython)
  n = 1
  ref = Cl_element
FEATURE [App::DocumentObjectGroupPython] G4_SILVER_CHLORIDE  # scripted group (container) (typed FeaturePython)
  Dunit = g/cm3
  Dvalue = 5.56
  Group = -> [Ag_element003,Cl_element022]
  conduct = 2
  density = 1
  expand = 3
  formula = G4_SILVER_CHLORIDE
  name = G4_SILVER_CHLORIDE
  specific = 4
FEATURE [App::DocumentObjectGroupPython] Br_element006  label="Br_element : 0.423"  # scripted group (container) (typed FeaturePython)
  n = 0.422895
FEATURE [App::DocumentObjectGroupPython] Ag_element004  label="Ag_element : 0.574"  # scripted group (container) (typed FeaturePython)
  n = 0.573748
FEATURE [App::DocumentObjectGroupPython] I_element007  label="I_element : 0.649"  # scripted group (container) (typed FeaturePython)
  n = 0.003357
FEATURE [App::DocumentObjectGroupPython] G4_SILVER_HALIDES  # scripted group (container) (typed FeaturePython)
  Dunit = g/cm3
  Dvalue = 6.47
  Group = -> [Br_element006,Ag_element004,I_element007]
  conduct = 2
  density = 1
  expand = 3
  formula = G4_SILVER_HALIDES
  name = G4_SILVER_HALIDES
  specific = 4
FEATURE [App::DocumentObjectGroupPython] Ag_element005  label="Ag_element : 003"  # scripted group (container) (typed FeaturePython)
  n = 1
  ref = Ag_element
FEATURE [App::DocumentObjectGroupPython] I_element008  label="I_element : 004"  # scripted group (container) (typed FeaturePython)
  n = 1
  ref = I_element
FEATURE [App::DocumentObjectGroupPython] G4_SILVER_IODIDE  # scripted group (container) (typed FeaturePython)
  Dunit = g/cm3
  Dvalue = 6.01
  Group = -> [Ag_element005,I_element008]
  conduct = 2
  density = 1
  expand = 3
  formula = G4_SILVER_IODIDE
  name = G4_SILVER_IODIDE
  specific = 4
FEATURE [App::DocumentObjectGroupPython] H_element095  label="H_element : 0.100"  # scripted group (container) (typed FeaturePython)
  n = 0.1
FEATURE [App::DocumentObjectGroupPython] C_element103  label="C_element : 0.204"  # scripted group (container) (typed FeaturePython)
  n = 0.204
FEATURE [App::DocumentObjectGroupPython] N_element039  label="N_element : 0.759"  # scripted group (container) (typed FeaturePython)
  n = 0.042
FEATURE [App::DocumentObjectGroupPython] O_element088  label="O_element : 0.645"  # scripted group (container) (typed FeaturePython)
  n = 0.645
FEATURE [App::DocumentObjectGroupPython] Na_element013  label="Na_element : 0.100"  # scripted group (container) (typed FeaturePython)
  n = 0.002
FEATURE [App::DocumentObjectGroupPython] P_element009  label="P_element : 0.107"  # scripted group (container) (typed FeaturePython)
  n = 0.001
FEATURE [App::DocumentObjectGroupPython] S_element020  label="S_element : 0.021"  # scripted group (container) (typed FeaturePython)
  n = 0.002
FEATURE [App::DocumentObjectGroupPython] Cl_element023  label="Cl_element : 0.590"  # scripted group (container) (typed FeaturePython)
  n = 0.003
FEATURE [App::DocumentObjectGroupPython] K_element010  label="K_element : 0.001"  # scripted group (container) (typed FeaturePython)
  n = 0.001
FEATURE [App::DocumentObjectGroupPython] G4_SKIN_ICRP  # scripted group (container) (typed FeaturePython)
  Dunit = g/cm3
  Dvalue = 1.09
  Group = -> [H_element095,C_element103,N_element039,O_element088,Na_element013,P_element009,S_element020,Cl_element023,K_element010]
  conduct = 2
  density = 1
  expand = 3
  formula = G4_SKIN_ICRP
  name = G4_SKIN_ICRP
  specific = 4
FEATURE [App::DocumentObjectGroupPython] Na_element014  label="Na_element : 2"  # scripted group (container) (typed FeaturePython)
  n = 2
  ref = Na_element
FEATURE [App::DocumentObjectGroupPython] C_element104  label="C_element : 058"  # scripted group (container) (typed FeaturePython)
  n = 1
  ref = C_element
FEATURE [App::DocumentObjectGroupPython] O_element089  label="O_element : 049"  # scripted group (container) (typed FeaturePython)
  n = 3
  ref = O_element
FEATURE [App::DocumentObjectGroupPython] G4_SODIUM_CARBONATE  # scripted group (container) (typed FeaturePython)
  Dunit = g/cm3
  Dvalue = 2.532
  Group = -> [Na_element014,C_element104,O_element089]
  conduct = 2
  density = 1
  expand = 3
  formula = G4_SODIUM_CARBONATE
  name = G4_SODIUM_CARBONATE
  specific = 4
FEATURE [App::DocumentObjectGroupPython] Na_element015  label="Na_element : 1"  # scripted group (container) (typed FeaturePython)
  n = 1
  ref = Na_element
FEATURE [App::DocumentObjectGroupPython] I_element009  label="I_element : 005"  # scripted group (container) (typed FeaturePython)
  n = 1
  ref = I_element
FEATURE [App::DocumentObjectGroupPython] G4_SODIUM_IODIDE  # scripted group (container) (typed FeaturePython)
  Dunit = g/cm3
  Dvalue = 3.667
  Group = -> [Na_element015,I_element009]
  conduct = 2
  density = 1
  expand = 3
  formula = G4_SODIUM_IODIDE
  name = G4_SODIUM_IODIDE
  specific = 4
FEATURE [App::DocumentObjectGroupPython] Na_element016  label="Na_element : 003"  # scripted group (container) (typed FeaturePython)
  n = 2
  ref = Na_element
FEATURE [App::DocumentObjectGroupPython] O_element090  label="O_element : 050"  # scripted group (container) (typed FeaturePython)
  n = 1
  ref = O_element
FEATURE [App::DocumentObjectGroupPython] G4_SODIUM_MONOXIDE  # scripted group (container) (typed FeaturePython)
  Dunit = g/cm3
  Dvalue = 2.27
  Group = -> [Na_element016,O_element090]
  conduct = 2
  density = 1
  expand = 3
  formula = G4_SODIUM_MONOXIDE
  name = G4_SODIUM_MONOXIDE
  specific = 4
FEATURE [App::DocumentObjectGroupPython] Na_element017  label="Na_element : 004"  # scripted group (container) (typed FeaturePython)
  n = 1
  ref = Na_element
FEATURE [App::DocumentObjectGroupPython] N_element040  label="N_element : 018"  # scripted group (container) (typed FeaturePython)
  n = 1
  ref = N_element
FEATURE [App::DocumentObjectGroupPython] O_element091  label="O_element : 051"  # scripted group (container) (typed FeaturePython)
  n = 3
  ref = O_element
FEATURE [App::DocumentObjectGroupPython] G4_SODIUM_NITRATE  # scripted group (container) (typed FeaturePython)
  Dunit = g/cm3
  Dvalue = 2.261
  Group = -> [Na_element017,N_element040,O_element091]
  conduct = 2
  density = 1
  expand = 3
  formula = G4_SODIUM_NITRATE
  name = G4_SODIUM_NITRATE
  specific = 4
FEATURE [App::DocumentObjectGroupPython] C_element105  label="C_element : 059"  # scripted group (container) (typed FeaturePython)
  n = 14
  ref = C_element
FEATURE [App::DocumentObjectGroupPython] H_element096  label="H_element : 053"  # scripted group (container) (typed FeaturePython)
  n = 12
  ref = H_element
FEATURE [App::DocumentObjectGroupPython] G4_STILBENE  # scripted group (container) (typed FeaturePython)
  Dunit = g/cm3
  Dvalue = 0.9707
  Group = -> [C_element105,H_element096]
  conduct = 2
  density = 1
  expand = 3
  formula = G4_STILBENE
  name = G4_STILBENE
  specific = 4
FEATURE [App::DocumentObjectGroupPython] C_element106  label="C_element : 12"  # scripted group (container) (typed FeaturePython)
  n = 12
  ref = C_element
FEATURE [App::DocumentObjectGroupPython] H_element097  label="H_element : 22"  # scripted group (container) (typed FeaturePython)
  n = 22
  ref = H_element
FEATURE [App::DocumentObjectGroupPython] O_element092  label="O_element : 11"  # scripted group (container) (typed FeaturePython)
  n = 11
  ref = O_element
FEATURE [App::DocumentObjectGroupPython] G4_SUCROSE  # scripted group (container) (typed FeaturePython)
  Dunit = g/cm3
  Dvalue = 1.5805
  Group = -> [C_element106,H_element097,O_element092]
  conduct = 2
  density = 1
  expand = 3
  formula = G4_SUCROSE
  name = G4_SUCROSE
  specific = 4
FEATURE [App::DocumentObjectGroupPython] C_element107  label="C_element : 18"  # scripted group (container) (typed FeaturePython)
  n = 18
  ref = C_element
FEATURE [App::DocumentObjectGroupPython] H_element098  label="H_element : 054"  # scripted group (container) (typed FeaturePython)
  n = 14
  ref = H_element
FEATURE [App::DocumentObjectGroupPython] G4_TERPHENYL  # scripted group (container) (typed FeaturePython)
  Dunit = g/cm3
  Dvalue = 1.24
  Group = -> [C_element107,H_element098]
  conduct = 2
  density = 1
  expand = 3
  formula = G4_TERPHENYL
  name = G4_TERPHENYL
  specific = 4
FEATURE [App::DocumentObjectGroupPython] H_element099  label="H_element : 0.146"  # scripted group (container) (typed FeaturePython)
  n = 0.106
FEATURE [App::DocumentObjectGroupPython] C_element108  label="C_element : 0.883"  # scripted group (container) (typed FeaturePython)
  n = 0.099
FEATURE [App::DocumentObjectGroupPython] N_element041  label="N_element : 0.020"  # scripted group (container) (typed FeaturePython)
  n = 0.02
FEATURE [App::DocumentObjectGroupPython] O_element093  label="O_element : 0.766"  # scripted group (container) (typed FeaturePython)
  n = 0.766
FEATURE [App::DocumentObjectGroupPython] Na_element018  label="Na_element : 0.101"  # scripted group (container) (typed FeaturePython)
  n = 0.002
FEATURE [App::DocumentObjectGroupPython] P_element010  label="P_element : 0.108"  # scripted group (container) (typed FeaturePython)
  n = 0.001
FEATURE [App::DocumentObjectGroupPython] S_element021  label="S_element : 0.022"  # scripted group (container) (typed FeaturePython)
  n = 0.002
FEATURE [App::DocumentObjectGroupPython] Cl_element024  label="Cl_element : 0.002"  # scripted group (container) (typed FeaturePython)
  n = 0.002
FEATURE [App::DocumentObjectGroupPython] K_element011  label="K_element : 0.017"  # scripted group (container) (typed FeaturePython)
  n = 0.002
FEATURE [App::DocumentObjectGroupPython] G4_TESTIS_ICRP  # scripted group (container) (typed FeaturePython)
  Dunit = g/cm3
  Dvalue = 1.04
  Group = -> [H_element099,C_element108,N_element041,O_element093,Na_element018,P_element010,S_element021,Cl_element024,K_element011]
  conduct = 2
  density = 1
  expand = 3
  formula = G4_TESTIS_ICRP
  name = G4_TESTIS_ICRP
  specific = 4
FEATURE [App::DocumentObjectGroupPython] C_element109  label="C_element : 060"  # scripted group (container) (typed FeaturePython)
  n = 2
  ref = C_element
FEATURE [App::DocumentObjectGroupPython] Cl_element025  label="Cl_element : 012"  # scripted group (container) (typed FeaturePython)
  n = 4
  ref = Cl_element
FEATURE [App::DocumentObjectGroupPython] G4_TETRACHLOROETHYLENE  # scripted group (container) (typed FeaturePython)
  Dunit = g/cm3
  Dvalue = 1.625
  Group = -> [C_element109,Cl_element025]
  conduct = 2
  density = 1
  expand = 3
  formula = G4_TETRACHLOROETHYLENE
  name = G4_TETRACHLOROETHYLENE
  specific = 4
FEATURE [App::DocumentObjectGroupPython] Tl_element001  label="Tl_element : 1"  # scripted group (container) (typed FeaturePython)
  n = 1
  ref = Tl_element
FEATURE [App::DocumentObjectGroupPython] Cl_element026  label="Cl_element : 013"  # scripted group (container) (typed FeaturePython)
  n = 1
  ref = Cl_element
FEATURE [App::DocumentObjectGroupPython] G4_THALLIUM_CHLORIDE  # scripted group (container) (typed FeaturePython)
  Dunit = g/cm3
  Dvalue = 7.004
  Group = -> [Tl_element001,Cl_element026]
  conduct = 2
  density = 1
  expand = 3
  formula = G4_THALLIUM_CHLORIDE
  name = G4_THALLIUM_CHLORIDE
  specific = 4
FEATURE [App::DocumentObjectGroupPython] H_element100  label="H_element : 0.147"  # scripted group (container) (typed FeaturePython)
  n = 0.105
FEATURE [App::DocumentObjectGroupPython] C_element110  label="C_element : 0.256"  # scripted group (container) (typed FeaturePython)
  n = 0.256
FEATURE [App::DocumentObjectGroupPython] N_element042  label="N_element : 0.760"  # scripted group (container) (typed FeaturePython)
  n = 0.027
FEATURE [App::DocumentObjectGroupPython] O_element094  label="O_element : 0.602"  # scripted group (container) (typed FeaturePython)
  n = 0.602
FEATURE [App::DocumentObjectGroupPython] Na_element019  label="Na_element : 0.102"  # scripted group (container) (typed FeaturePython)
  n = 0.001
FEATURE [App::DocumentObjectGroupPython] P_element011  label="P_element : 0.109"  # scripted group (container) (typed FeaturePython)
  n = 0.002
FEATURE [App::DocumentObjectGroupPython] S_element022  label="S_element : 0.023"  # scripted group (container) (typed FeaturePython)
  n = 0.003
FEATURE [App::DocumentObjectGroupPython] Cl_element027  label="Cl_element : 0.591"  # scripted group (container) (typed FeaturePython)
  n = 0.002
FEATURE [App::DocumentObjectGroupPython] K_element012  label="K_element : 0.018"  # scripted group (container) (typed FeaturePython)
  n = 0.002
FEATURE [App::DocumentObjectGroupPython] G4_TISSUE_SOFT_ICRP  # scripted group (container) (typed FeaturePython)
  Dunit = g/cm3
  Dvalue = 1.03
  Group = -> [H_element100,C_element110,N_element042,O_element094,Na_element019,P_element011,S_element022,Cl_element027,K_element012]
  conduct = 2
  density = 1
  expand = 3
  formula = G4_TISSUE_SOFT_ICRP
  name = G4_TISSUE_SOFT_ICRP
  specific = 4
FEATURE [App::DocumentObjectGroupPython] H_element101  label="H_element : 0.148"  # scripted group (container) (typed FeaturePython)
  n = 0.101
FEATURE [App::DocumentObjectGroupPython] C_element111  label="C_element : 0.111"  # scripted group (container) (typed FeaturePython)
  n = 0.111
FEATURE [App::DocumentObjectGroupPython] N_element043  label="N_element : 0.026"  # scripted group (container) (typed FeaturePython)
  n = 0.026
FEATURE [App::DocumentObjectGroupPython] O_element095  label="O_element : 0.762"  # scripted group (container) (typed FeaturePython)
  n = 0.762
FEATURE [App::DocumentObjectGroupPython] G4_TISSUE_SOFT_ICRU_4  label="G4_TISSUE_SOFT_ICRU-4"  # scripted group (container) (typed FeaturePython)
  Dunit = g/cm3
  Dvalue = 1
  Group = -> [H_element101,C_element111,N_element043,O_element095]
  conduct = 2
  density = 1
  expand = 3
  formula = G4_TISSUE_SOFT_ICRU-4
  name = G4_TISSUE_SOFT_ICRU-4
  specific = 4
FEATURE [App::DocumentObjectGroupPython] H_element102  label="H_element : 0.149"  # scripted group (container) (typed FeaturePython)
  n = 0.101869
FEATURE [App::DocumentObjectGroupPython] C_element112  label="C_element : 0.456"  # scripted group (container) (typed FeaturePython)
  n = 0.456179
FEATURE [App::DocumentObjectGroupPython] N_element044  label="N_element : 0.761"  # scripted group (container) (typed FeaturePython)
  n = 0.035172
FEATURE [App::DocumentObjectGroupPython] O_element096  label="O_element : 0.407"  # scripted group (container) (typed FeaturePython)
  n = 0.40678
FEATURE [App::DocumentObjectGroupPython] G4_TISSUE_METHANE  label="G4_TISSUE-METHANE"  # scripted group (container) (typed FeaturePython)
  Dunit = g/cm3
  Dvalue = 0.00106409
  Group = -> [H_element102,C_element112,N_element044,O_element096]
  conduct = 2
  density = 1
  expand = 3
  formula = G4_TISSUE-METHANE
  name = G4_TISSUE-METHANE
  specific = 4
FEATURE [App::DocumentObjectGroupPython] H_element103  label="H_element : 0.103"  # scripted group (container) (typed FeaturePython)
  n = 0.102672
FEATURE [App::DocumentObjectGroupPython] C_element113  label="C_element : 0.569"  # scripted group (container) (typed FeaturePython)
  n = 0.56894
FEATURE [App::DocumentObjectGroupPython] N_element045  label="N_element : 0.762"  # scripted group (container) (typed FeaturePython)
  n = 0.035022
FEATURE [App::DocumentObjectGroupPython] O_element097  label="O_element : 0.293"  # scripted group (container) (typed FeaturePython)
  n = 0.293366
FEATURE [App::DocumentObjectGroupPython] G4_TISSUE_PROPANE  label="G4_TISSUE-PROPANE"  # scripted group (container) (typed FeaturePython)
  Dunit = g/cm3
  Dvalue = 0.00182628
  Group = -> [H_element103,C_element113,N_element045,O_element097]
  conduct = 2
  density = 1
  expand = 3
  formula = G4_TISSUE-PROPANE
  name = G4_TISSUE-PROPANE
  specific = 4
FEATURE [App::DocumentObjectGroupPython] Ti_element003  label="Ti_element : 1"  # scripted group (container) (typed FeaturePython)
  n = 1
  ref = Ti_element
FEATURE [App::DocumentObjectGroupPython] O_element098  label="O_element : 052"  # scripted group (container) (typed FeaturePython)
  n = 2
  ref = O_element
FEATURE [App::DocumentObjectGroupPython] G4_TITANIUM_DIOXIDE  # scripted group (container) (typed FeaturePython)
  Dunit = g/cm3
  Dvalue = 4.26
  Group = -> [Ti_element003,O_element098]
  conduct = 2
  density = 1
  expand = 3
  formula = G4_TITANIUM_DIOXIDE
  name = G4_TITANIUM_DIOXIDE
  specific = 4
FEATURE [App::DocumentObjectGroupPython] C_element114  label="C_element : 061"  # scripted group (container) (typed FeaturePython)
  n = 7
  ref = C_element
FEATURE [App::DocumentObjectGroupPython] H_element104  label="H_element : 055"  # scripted group (container) (typed FeaturePython)
  n = 8
  ref = H_element
FEATURE [App::DocumentObjectGroupPython] G4_TOLUENE  # scripted group (container) (typed FeaturePython)
  Dunit = g/cm3
  Dvalue = 0.8669
  Group = -> [C_element114,H_element104]
  conduct = 2
  density = 1
  expand = 3
  formula = G4_TOLUENE
  name = G4_TOLUENE
  specific = 4
FEATURE [App::DocumentObjectGroupPython] C_element115  label="C_element : 062"  # scripted group (container) (typed FeaturePython)
  n = 2
  ref = C_element
FEATURE [App::DocumentObjectGroupPython] H_element105  label="H_element : 056"  # scripted group (container) (typed FeaturePython)
  n = 1
  ref = H_element
FEATURE [App::DocumentObjectGroupPython] Cl_element028  label="Cl_element : 014"  # scripted group (container) (typed FeaturePython)
  n = 3
  ref = Cl_element
FEATURE [App::DocumentObjectGroupPython] G4_TRICHLOROETHYLENE  # scripted group (container) (typed FeaturePython)
  Dunit = g/cm3
  Dvalue = 1.46
  Group = -> [C_element115,H_element105,Cl_element028]
  conduct = 2
  density = 1
  expand = 3
  formula = G4_TRICHLOROETHYLENE
  name = G4_TRICHLOROETHYLENE
  specific = 4
FEATURE [App::DocumentObjectGroupPython] C_element116  label="C_element : 063"  # scripted group (container) (typed FeaturePython)
  n = 6
  ref = C_element
FEATURE [App::DocumentObjectGroupPython] H_element106  label="H_element : 15"  # scripted group (container) (typed FeaturePython)
  n = 15
  ref = H_element
FEATURE [App::DocumentObjectGroupPython] O_element099  label="O_element : 053"  # scripted group (container) (typed FeaturePython)
  n = 4
  ref = O_element
FEATURE [App::DocumentObjectGroupPython] P_element012  label="P_element : 1"  # scripted group (container) (typed FeaturePython)
  n = 1
  ref = P_element
FEATURE [App::DocumentObjectGroupPython] G4_TRIETHYL_PHOSPHATE  # scripted group (container) (typed FeaturePython)
  Dunit = g/cm3
  Dvalue = 1.07
  Group = -> [C_element116,H_element106,O_element099,P_element012]
  conduct = 2
  density = 1
  expand = 3
  formula = G4_TRIETHYL_PHOSPHATE
  name = G4_TRIETHYL_PHOSPHATE
  specific = 4
FEATURE [App::DocumentObjectGroupPython] W_element003  label="W_element : 003"  # scripted group (container) (typed FeaturePython)
  n = 1
  ref = W_element
FEATURE [App::DocumentObjectGroupPython] F_element017  label="F_element : 6"  # scripted group (container) (typed FeaturePython)
  n = 6
  ref = F_element
FEATURE [App::DocumentObjectGroupPython] G4_TUNGSTEN_HEXAFLUORIDE  # scripted group (container) (typed FeaturePython)
  Dunit = g/cm3
  Dvalue = 2.4
  Group = -> [W_element003,F_element017]
  conduct = 2
  density = 1
  expand = 3
  formula = G4_TUNGSTEN_HEXAFLUORIDE
  name = G4_TUNGSTEN_HEXAFLUORIDE
  specific = 4
FEATURE [App::DocumentObjectGroupPython] U_element001  label="U_element : 1"  # scripted group (container) (typed FeaturePython)
  n = 1
  ref = U_element
FEATURE [App::DocumentObjectGroupPython] C_element117  label="C_element : 064"  # scripted group (container) (typed FeaturePython)
  n = 2
  ref = C_element
FEATURE [App::DocumentObjectGroupPython] G4_URANIUM_DICARBIDE  # scripted group (container) (typed FeaturePython)
  Dunit = g/cm3
  Dvalue = 11.28
  Group = -> [U_element001,C_element117]
  conduct = 2
  density = 1
  expand = 3
  formula = G4_URANIUM_DICARBIDE
  name = G4_URANIUM_DICARBIDE
  specific = 4
FEATURE [App::DocumentObjectGroupPython] U_element002  label="U_element : 002"  # scripted group (container) (typed FeaturePython)
  n = 1
  ref = U_element
FEATURE [App::DocumentObjectGroupPython] C_element118  label="C_element : 065"  # scripted group (container) (typed FeaturePython)
  n = 1
  ref = C_element
FEATURE [App::DocumentObjectGroupPython] G4_URANIUM_MONOCARBIDE  # scripted group (container) (typed FeaturePython)
  Dunit = g/cm3
  Dvalue = 13.63
  Group = -> [U_element002,C_element118]
  conduct = 2
  density = 1
  expand = 3
  formula = G4_URANIUM_MONOCARBIDE
  name = G4_URANIUM_MONOCARBIDE
  specific = 4
FEATURE [App::DocumentObjectGroupPython] U_element003  label="U_element : 003"  # scripted group (container) (typed FeaturePython)
  n = 1
  ref = U_element
FEATURE [App::DocumentObjectGroupPython] O_element100  label="O_element : 054"  # scripted group (container) (typed FeaturePython)
  n = 2
  ref = O_element
FEATURE [App::DocumentObjectGroupPython] G4_URANIUM_OXIDE  # scripted group (container) (typed FeaturePython)
  Dunit = g/cm3
  Dvalue = 10.96
  Group = -> [U_element003,O_element100]
  conduct = 2
  density = 1
  expand = 3
  formula = G4_URANIUM_OXIDE
  name = G4_URANIUM_OXIDE
  specific = 4
FEATURE [App::DocumentObjectGroupPython] C_element119  label="C_element : 066"  # scripted group (container) (typed FeaturePython)
  n = 1
  ref = C_element
FEATURE [App::DocumentObjectGroupPython] H_element107  label="H_element : 057"  # scripted group (container) (typed FeaturePython)
  n = 4
  ref = H_element
FEATURE [App::DocumentObjectGroupPython] N_element046  label="N_element : 019"  # scripted group (container) (typed FeaturePython)
  n = 2
  ref = N_element
FEATURE [App::DocumentObjectGroupPython] O_element101  label="O_element : 055"  # scripted group (container) (typed FeaturePython)
  n = 1
  ref = O_element
FEATURE [App::DocumentObjectGroupPython] G4_UREA  # scripted group (container) (typed FeaturePython)
  Dunit = g/cm3
  Dvalue = 1.323
  Group = -> [C_element119,H_element107,N_element046,O_element101]
  conduct = 2
  density = 1
  expand = 3
  formula = G4_UREA
  name = G4_UREA
  specific = 4
FEATURE [App::DocumentObjectGroupPython] C_element120  label="C_element : 067"  # scripted group (container) (typed FeaturePython)
  n = 5
  ref = C_element
FEATURE [App::DocumentObjectGroupPython] H_element108  label="H_element : 058"  # scripted group (container) (typed FeaturePython)
  n = 11
  ref = H_element
FEATURE [App::DocumentObjectGroupPython] N_element047  label="N_element : 020"  # scripted group (container) (typed FeaturePython)
  n = 1
  ref = N_element
FEATURE [App::DocumentObjectGroupPython] O_element102  label="O_element : 056"  # scripted group (container) (typed FeaturePython)
  n = 2
  ref = O_element
FEATURE [App::DocumentObjectGroupPython] G4_VALINE  # scripted group (container) (typed FeaturePython)
  Dunit = g/cm3
  Dvalue = 1.23
  Group = -> [C_element120,H_element108,N_element047,O_element102]
  conduct = 2
  density = 1
  expand = 3
  formula = G4_VALINE
  name = G4_VALINE
  specific = 4
FEATURE [App::DocumentObjectGroupPython] H_element109  label="H_element : 0.009"  # scripted group (container) (typed FeaturePython)
  n = 0.009417
FEATURE [App::DocumentObjectGroupPython] C_element121  label="C_element : 0.281"  # scripted group (container) (typed FeaturePython)
  n = 0.280555
FEATURE [App::DocumentObjectGroupPython] F_element018  label="F_element : 0.710"  # scripted group (container) (typed FeaturePython)
  n = 0.710028
FEATURE [App::DocumentObjectGroupPython] G4_VITON  # scripted group (container) (typed FeaturePython)
  Dunit = g/cm3
  Dvalue = 1.8
  Group = -> [H_element109,C_element121,F_element018]
  conduct = 2
  density = 1
  expand = 3
  formula = G4_VITON
  name = G4_VITON
  specific = 4
FEATURE [App::DocumentObjectGroupPython] H_element110  label="H_element : 059"  # scripted group (container) (typed FeaturePython)
  n = 2
  ref = H_element
FEATURE [App::DocumentObjectGroupPython] O_element103  label="O_element : 057"  # scripted group (container) (typed FeaturePython)
  n = 1
  ref = O_element
FEATURE [App::DocumentObjectGroupPython] G4_WATER  # scripted group (container) (typed FeaturePython)
  Dunit = g/cm3
  Dvalue = 1
  Group = -> [H_element110,O_element103]
  conduct = 2
  density = 1
  expand = 3
  formula = G4_WATER
  name = G4_WATER
  specific = 4
FEATURE [App::DocumentObjectGroupPython] H_element111  label="H_element : 060"  # scripted group (container) (typed FeaturePython)
  n = 2
  ref = H_element
FEATURE [App::DocumentObjectGroupPython] O_element104  label="O_element : 058"  # scripted group (container) (typed FeaturePython)
  n = 1
  ref = O_element
FEATURE [App::DocumentObjectGroupPython] G4_WATER_VAPOR  # scripted group (container) (typed FeaturePython)
  Dunit = g/cm3
  Dvalue = 0.000756182
  Group = -> [H_element111,O_element104]
  conduct = 2
  density = 1
  expand = 3
  formula = G4_WATER_VAPOR
  name = G4_WATER_VAPOR
  specific = 4
FEATURE [App::DocumentObjectGroupPython] C_element122  label="C_element : 068"  # scripted group (container) (typed FeaturePython)
  n = 8
  ref = C_element
FEATURE [App::DocumentObjectGroupPython] H_element112  label="H_element : 061"  # scripted group (container) (typed FeaturePython)
  n = 10
  ref = H_element
FEATURE [App::DocumentObjectGroupPython] G4_XYLENE  # scripted group (container) (typed FeaturePython)
  Dunit = g/cm3
  Dvalue = 0.87
  Group = -> [C_element122,H_element112]
  conduct = 2
  density = 1
  expand = 3
  formula = G4_XYLENE
  name = G4_XYLENE
  specific = 4
FEATURE [App::DocumentObjectGroupPython] C_element123  label="C_element : 069"  # scripted group (container) (typed FeaturePython)
  n = 1
  ref = C_element
FEATURE [App::DocumentObjectGroupPython] G4_GRAPHITE  # scripted group (container) (typed FeaturePython)
  Dunit = g/cm3
  Dvalue = 2.21
  Group = -> [C_element123]
  conduct = 2
  density = 1
  expand = 3
  formula = G4_GRAPHITE
  name = G4_GRAPHITE
  specific = 4
FEATURE [App::DocumentObjectGroupPython] NIST  # scripted group (container) (typed FeaturePython)
  Group = -> [G4_A_150_TISSUE,G4_ACETONE,G4_ACETYLENE,G4_ADENINE,G4_ADIPOSE_TISSUE_ICRP,G4_AIR,G4_ALANINE,G4_ALUMINUM_OXIDE,G4_AMBER,G4_AMMONIA,G4_ANILINE,G4_ANTHRACENE,G4_B_100_BONE,G4_BAKELITE,G4_BARIUM_FLUORIDE,G4_BARIUM_SULFATE,G4_BENZENE,G4_BERYLLIUM_OXIDE,G4_BGO,G4_BLOOD_ICRP,G4_BONE_COMPACT_ICRU,G4_BONE_CORTICAL_ICRP,G4_BORON_CARBIDE,G4_BORON_OXIDE,G4_BRAIN_ICRP,G4_BUTANE,G4_N_BUTYL_ALCOHOL,G4_C_552,+152 more]
FEATURE [App::DocumentObjectGroupPython] H_element113  label="H_element : 062"  # scripted group (container) (typed FeaturePython)
  n = 1
  ref = H_element
FEATURE [App::DocumentObjectGroupPython] G4_H  # scripted group (container) (typed FeaturePython)
  Dunit = g/cm3
  Dvalue = 8.3748e-05
  Group = -> [H_element113]
  conduct = 2
  density = 1
  expand = 3
  formula = H
  name = G4_H
  specific = 4
FEATURE [App::DocumentObjectGroupPython] He_element001  label="He_element : 1"  # scripted group (container) (typed FeaturePython)
  n = 1
  ref = He_element
FEATURE [App::DocumentObjectGroupPython] G4_He  # scripted group (container) (typed FeaturePython)
  Dunit = g/cm3
  Dvalue = 0.000166322
  Group = -> [He_element001]
  conduct = 2
  density = 1
  expand = 3
  formula = He
  name = G4_He
  specific = 4
FEATURE [App::DocumentObjectGroupPython] Li_element008  label="Li_element : 008"  # scripted group (container) (typed FeaturePython)
  n = 1
  ref = Li_element
FEATURE [App::DocumentObjectGroupPython] G4_Li  # scripted group (container) (typed FeaturePython)
  Dunit = g/cm3
  Dvalue = 0.534
  Group = -> [Li_element008]
  conduct = 2
  density = 1
  expand = 3
  formula = Li
  name = G4_Li
  specific = 4
FEATURE [App::DocumentObjectGroupPython] Be_element002  label="Be_element : 002"  # scripted group (container) (typed FeaturePython)
  n = 1
  ref = Be_element
FEATURE [App::DocumentObjectGroupPython] G4_Be  # scripted group (container) (typed FeaturePython)
  Dunit = g/cm3
  Dvalue = 1.848
  Group = -> [Be_element002]
  conduct = 2
  density = 1
  expand = 3
  formula = Be
  name = G4_Be
  specific = 4
FEATURE [App::DocumentObjectGroupPython] B_element007  label="B_element : 007"  # scripted group (container) (typed FeaturePython)
  n = 1
  ref = B_element
FEATURE [App::DocumentObjectGroupPython] G4_B  # scripted group (container) (typed FeaturePython)
  Dunit = g/cm3
  Dvalue = 2.37
  Group = -> [B_element007]
  conduct = 2
  density = 1
  expand = 3
  formula = B
  name = G4_B
  specific = 4
FEATURE [App::DocumentObjectGroupPython] C_element124  label="C_element : 070"  # scripted group (container) (typed FeaturePython)
  n = 1
  ref = C_element
FEATURE [App::DocumentObjectGroupPython] G4_C  # scripted group (container) (typed FeaturePython)
  Dunit = g/cm3
  Dvalue = 2
  Group = -> [C_element124]
  conduct = 2
  density = 1
  expand = 3
  formula = C
  name = G4_C
  specific = 4
FEATURE [App::DocumentObjectGroupPython] N_element048  label="N_element : 021"  # scripted group (container) (typed FeaturePython)
  n = 1
  ref = N_element
FEATURE [App::DocumentObjectGroupPython] G4_N  # scripted group (container) (typed FeaturePython)
  Dunit = g/cm3
  Dvalue = 0.0011652
  Group = -> [N_element048]
  conduct = 2
  density = 1
  expand = 3
  formula = N
  name = G4_N
  specific = 4
FEATURE [App::DocumentObjectGroupPython] O_element105  label="O_element : 059"  # scripted group (container) (typed FeaturePython)
  n = 1
  ref = O_element
FEATURE [App::DocumentObjectGroupPython] G4_O  # scripted group (container) (typed FeaturePython)
  Dunit = g/cm3
  Dvalue = 0.00133151
  Group = -> [O_element105]
  conduct = 2
  density = 1
  expand = 3
  formula = O
  name = G4_O
  specific = 4
FEATURE [App::DocumentObjectGroupPython] F_element019  label="F_element : 008"  # scripted group (container) (typed FeaturePython)
  n = 1
  ref = F_element
FEATURE [App::DocumentObjectGroupPython] G4_F  # scripted group (container) (typed FeaturePython)
  Dunit = g/cm3
  Dvalue = 0.00158029
  Group = -> [F_element019]
  conduct = 2
  density = 1
  expand = 3
  formula = F
  name = G4_F
  specific = 4
FEATURE [App::DocumentObjectGroupPython] Ne_element001  label="Ne_element : 1"  # scripted group (container) (typed FeaturePython)
  n = 1
  ref = Ne_element
FEATURE [App::DocumentObjectGroupPython] G4_Ne  # scripted group (container) (typed FeaturePython)
  Dunit = g/cm3
  Dvalue = 0.000838505
  Group = -> [Ne_element001]
  conduct = 2
  density = 1
  expand = 3
  formula = Ne
  name = G4_Ne
  specific = 4
FEATURE [App::DocumentObjectGroupPython] Na_element020  label="Na_element : 005"  # scripted group (container) (typed FeaturePython)
  n = 1
  ref = Na_element
FEATURE [App::DocumentObjectGroupPython] G4_Na  # scripted group (container) (typed FeaturePython)
  Dunit = g/cm3
  Dvalue = 0.971
  Group = -> [Na_element020]
  conduct = 2
  density = 1
  expand = 3
  formula = Na
  name = G4_Na
  specific = 4
FEATURE [App::DocumentObjectGroupPython] Mg_element011  label="Mg_element : 005"  # scripted group (container) (typed FeaturePython)
  n = 1
  ref = Mg_element
FEATURE [App::DocumentObjectGroupPython] G4_Mg  # scripted group (container) (typed FeaturePython)
  Dunit = g/cm3
  Dvalue = 1.74
  Group = -> [Mg_element011]
  conduct = 2
  density = 1
  expand = 3
  formula = Mg
  name = G4_Mg
  specific = 4
FEATURE [App::DocumentObjectGroupPython] Al_element004  label="Al_element : 1"  # scripted group (container) (typed FeaturePython)
  n = 1
  ref = Al_element
FEATURE [App::DocumentObjectGroupPython] G4_Al  # scripted group (container) (typed FeaturePython)
  Dunit = g/cm3
  Dvalue = 2.699
  Group = -> [Al_element004]
  conduct = 2
  density = 1
  expand = 3
  formula = Al
  name = G4_Al
  specific = 4
FEATURE [App::DocumentObjectGroupPython] Si_element007  label="Si_element : 002"  # scripted group (container) (typed FeaturePython)
  n = 1
  ref = Si_element
FEATURE [App::DocumentObjectGroupPython] G4_Si  # scripted group (container) (typed FeaturePython)
  Dunit = g/cm3
  Dvalue = 2.33
  Group = -> [Si_element007]
  conduct = 2
  density = 1
  expand = 3
  formula = Si
  name = G4_Si
  specific = 4
FEATURE [App::DocumentObjectGroupPython] P_element013  label="P_element : 002"  # scripted group (container) (typed FeaturePython)
  n = 1
  ref = P_element
FEATURE [App::DocumentObjectGroupPython] G4_P  # scripted group (container) (typed FeaturePython)
  Dunit = g/cm3
  Dvalue = 2.2
  Group = -> [P_element013]
  conduct = 2
  density = 1
  expand = 3
  formula = P
  name = G4_P
  specific = 4
FEATURE [App::DocumentObjectGroupPython] S_element023  label="S_element : 007"  # scripted group (container) (typed FeaturePython)
  n = 1
  ref = S_element
FEATURE [App::DocumentObjectGroupPython] G4_S  # scripted group (container) (typed FeaturePython)
  Dunit = g/cm3
  Dvalue = 2
  Group = -> [S_element023]
  conduct = 2
  density = 1
  expand = 3
  formula = S
  name = G4_S
  specific = 4
FEATURE [App::DocumentObjectGroupPython] Cl_element029  label="Cl_element : 015"  # scripted group (container) (typed FeaturePython)
  n = 1
  ref = Cl_element
FEATURE [App::DocumentObjectGroupPython] G4_Cl  # scripted group (container) (typed FeaturePython)
  Dunit = g/cm3
  Dvalue = 0.00299473
  Group = -> [Cl_element029]
  conduct = 2
  density = 1
  expand = 3
  formula = Cl
  name = G4_Cl
  specific = 4
FEATURE [App::DocumentObjectGroupPython] Ar_element002  label="Ar_element : 1"  # scripted group (container) (typed FeaturePython)
  n = 1
  ref = Ar_element
FEATURE [App::DocumentObjectGroupPython] G4_Ar  # scripted group (container) (typed FeaturePython)
  Dunit = g/cm3
  Dvalue = 0.00166201
  Group = -> [Ar_element002]
  conduct = 2
  density = 1
  expand = 3
  formula = Ar
  name = G4_Ar
  specific = 4
FEATURE [App::DocumentObjectGroupPython] K_element013  label="K_element : 003"  # scripted group (container) (typed FeaturePython)
  n = 1
  ref = K_element
FEATURE [App::DocumentObjectGroupPython] G4_K  # scripted group (container) (typed FeaturePython)
  Dunit = g/cm3
  Dvalue = 0.862
  Group = -> [K_element013]
  conduct = 2
  density = 1
  expand = 3
  formula = K
  name = G4_K
  specific = 4
FEATURE [App::DocumentObjectGroupPython] Ca_element014  label="Ca_element : 007"  # scripted group (container) (typed FeaturePython)
  n = 1
  ref = Ca_element
FEATURE [App::DocumentObjectGroupPython] G4_Ca  # scripted group (container) (typed FeaturePython)
  Dunit = g/cm3
  Dvalue = 1.55
  Group = -> [Ca_element014]
  conduct = 2
  density = 1
  expand = 3
  formula = Ca
  name = G4_Ca
  specific = 4
FEATURE [App::DocumentObjectGroupPython] Sc_element001  label="Sc_element : 1"  # scripted group (container) (typed FeaturePython)
  n = 1
  ref = Sc_element
FEATURE [App::DocumentObjectGroupPython] G4_Sc  # scripted group (container) (typed FeaturePython)
  Dunit = g/cm3
  Dvalue = 2.989
  Group = -> [Sc_element001]
  conduct = 2
  density = 1
  expand = 3
  formula = Sc
  name = G4_Sc
  specific = 4
FEATURE [App::DocumentObjectGroupPython] Ti_element004  label="Ti_element : 002"  # scripted group (container) (typed FeaturePython)
  n = 1
  ref = Ti_element
FEATURE [App::DocumentObjectGroupPython] G4_Ti  # scripted group (container) (typed FeaturePython)
  Dunit = g/cm3
  Dvalue = 4.54
  Group = -> [Ti_element004]
  conduct = 2
  density = 1
  expand = 3
  formula = Ti
  name = G4_Ti
  specific = 4
FEATURE [App::DocumentObjectGroupPython] V_element001  label="V_element : 1"  # scripted group (container) (typed FeaturePython)
  n = 1
  ref = V_element
FEATURE [App::DocumentObjectGroupPython] G4_V  # scripted group (container) (typed FeaturePython)
  Dunit = g/cm3
  Dvalue = 6.11
  Group = -> [V_element001]
  conduct = 2
  density = 1
  expand = 3
  formula = V
  name = G4_V
  specific = 4
FEATURE [App::DocumentObjectGroupPython] Cr_element001  label="Cr_element : 1"  # scripted group (container) (typed FeaturePython)
  n = 1
  ref = Cr_element
FEATURE [App::DocumentObjectGroupPython] G4_Cr  # scripted group (container) (typed FeaturePython)
  Dunit = g/cm3
  Dvalue = 7.18
  Group = -> [Cr_element001]
  conduct = 2
  density = 1
  expand = 3
  formula = Cr
  name = G4_Cr
  specific = 4
FEATURE [App::DocumentObjectGroupPython] Mn_element001  label="Mn_element : 1"  # scripted group (container) (typed FeaturePython)
  n = 1
  ref = Mn_element
FEATURE [App::DocumentObjectGroupPython] G4_Mn  # scripted group (container) (typed FeaturePython)
  Dunit = g/cm3
  Dvalue = 7.44
  Group = -> [Mn_element001]
  conduct = 2
  density = 1
  expand = 3
  formula = Mn
  name = G4_Mn
  specific = 4
FEATURE [App::DocumentObjectGroupPython] Fe_element007  label="Fe_element : 004"  # scripted group (container) (typed FeaturePython)
  n = 1
  ref = Fe_element
FEATURE [App::DocumentObjectGroupPython] G4_Fe  # scripted group (container) (typed FeaturePython)
  Dunit = g/cm3
  Dvalue = 7.874
  Group = -> [Fe_element007]
  conduct = 2
  density = 1
  expand = 3
  formula = Fe
  name = G4_Fe
  specific = 4
FEATURE [App::DocumentObjectGroupPython] Co_element001  label="Co_element : 1"  # scripted group (container) (typed FeaturePython)
  n = 1
  ref = Co_element
FEATURE [App::DocumentObjectGroupPython] G4_Co  # scripted group (container) (typed FeaturePython)
  Dunit = g/cm3
  Dvalue = 8.9
  Group = -> [Co_element001]
  conduct = 2
  density = 1
  expand = 3
  formula = Co
  name = G4_Co
  specific = 4
FEATURE [App::DocumentObjectGroupPython] Ni_element001  label="Ni_element : 1"  # scripted group (container) (typed FeaturePython)
  n = 1
  ref = Ni_element
FEATURE [App::DocumentObjectGroupPython] G4_Ni  # scripted group (container) (typed FeaturePython)
  Dunit = g/cm3
  Dvalue = 8.902
  Group = -> [Ni_element001]
  conduct = 2
  density = 1
  expand = 3
  formula = Ni
  name = G4_Ni
  specific = 4
FEATURE [App::DocumentObjectGroupPython] Cu_element001  label="Cu_element : 1"  # scripted group (container) (typed FeaturePython)
  n = 1
  ref = Cu_element
FEATURE [App::DocumentObjectGroupPython] G4_Cu  # scripted group (container) (typed FeaturePython)
  Dunit = g/cm3
  Dvalue = 8.96
  Group = -> [Cu_element001]
  conduct = 2
  density = 1
  expand = 3
  formula = Cu
  name = G4_Cu
  specific = 4
FEATURE [App::DocumentObjectGroupPython] Zn_element001  label="Zn_element : 1"  # scripted group (container) (typed FeaturePython)
  n = 1
  ref = Zn_element
FEATURE [App::DocumentObjectGroupPython] G4_Zn  # scripted group (container) (typed FeaturePython)
  Dunit = g/cm3
  Dvalue = 7.133
  Group = -> [Zn_element001]
  conduct = 2
  density = 1
  expand = 3
  formula = Zn
  name = G4_Zn
  specific = 4
FEATURE [App::DocumentObjectGroupPython] Ga_element002  label="Ga_element : 002"  # scripted group (container) (typed FeaturePython)
  n = 1
  ref = Ga_element
FEATURE [App::DocumentObjectGroupPython] G4_Ga  # scripted group (container) (typed FeaturePython)
  Dunit = g/cm3
  Dvalue = 5.904
  Group = -> [Ga_element002]
  conduct = 2
  density = 1
  expand = 3
  formula = Ga
  name = G4_Ga
  specific = 4
FEATURE [App::DocumentObjectGroupPython] Ge_element002  label="Ge_element : 1"  # scripted group (container) (typed FeaturePython)
  n = 1
  ref = Ge_element
FEATURE [App::DocumentObjectGroupPython] G4_Ge  # scripted group (container) (typed FeaturePython)
  Dunit = g/cm3
  Dvalue = 5.323
  Group = -> [Ge_element002]
  conduct = 2
  density = 1
  expand = 3
  formula = Ge
  name = G4_Ge
  specific = 4
FEATURE [App::DocumentObjectGroupPython] As_element003  label="As_element : 002"  # scripted group (container) (typed FeaturePython)
  n = 1
  ref = As_element
FEATURE [App::DocumentObjectGroupPython] G4_As  # scripted group (container) (typed FeaturePython)
  Dunit = g/cm3
  Dvalue = 5.73
  Group = -> [As_element003]
  conduct = 2
  density = 1
  expand = 3
  formula = As
  name = G4_As
  specific = 4
FEATURE [App::DocumentObjectGroupPython] Se_element001  label="Se_element : 1"  # scripted group (container) (typed FeaturePython)
  n = 1
  ref = Se_element
FEATURE [App::DocumentObjectGroupPython] G4_Se  # scripted group (container) (typed FeaturePython)
  Dunit = g/cm3
  Dvalue = 4.5
  Group = -> [Se_element001]
  conduct = 2
  density = 1
  expand = 3
  formula = Se
  name = G4_Se
  specific = 4
FEATURE [App::DocumentObjectGroupPython] Br_element007  label="Br_element : 004"  # scripted group (container) (typed FeaturePython)
  n = 1
  ref = Br_element
FEATURE [App::DocumentObjectGroupPython] G4_Br  # scripted group (container) (typed FeaturePython)
  Dunit = g/cm3
  Dvalue = 0.0070721
  Group = -> [Br_element007]
  conduct = 2
  density = 1
  expand = 3
  formula = Br
  name = G4_Br
  specific = 4
FEATURE [App::DocumentObjectGroupPython] Kr_element001  label="Kr_element : 1"  # scripted group (container) (typed FeaturePython)
  n = 1
  ref = Kr_element
FEATURE [App::DocumentObjectGroupPython] G4_Kr  # scripted group (container) (typed FeaturePython)
  Dunit = g/cm3
  Dvalue = 0.00347832
  Group = -> [Kr_element001]
  conduct = 2
  density = 1
  expand = 3
  formula = Kr
  name = G4_Kr
  specific = 4
FEATURE [App::DocumentObjectGroupPython] Rb_element001  label="Rb_element : 1"  # scripted group (container) (typed FeaturePython)
  n = 1
  ref = Rb_element
FEATURE [App::DocumentObjectGroupPython] G4_Rb  # scripted group (container) (typed FeaturePython)
  Dunit = g/cm3
  Dvalue = 1.532
  Group = -> [Rb_element001]
  conduct = 2
  density = 1
  expand = 3
  formula = Rb
  name = G4_Rb
  specific = 4
FEATURE [App::DocumentObjectGroupPython] Sr_element001  label="Sr_element : 1"  # scripted group (container) (typed FeaturePython)
  n = 1
  ref = Sr_element
FEATURE [App::DocumentObjectGroupPython] G4_Sr  # scripted group (container) (typed FeaturePython)
  Dunit = g/cm3
  Dvalue = 2.54
  Group = -> [Sr_element001]
  conduct = 2
  density = 1
  expand = 3
  formula = Sr
  name = G4_Sr
  specific = 4
FEATURE [App::DocumentObjectGroupPython] Y_element001  label="Y_element : 1"  # scripted group (container) (typed FeaturePython)
  n = 1
  ref = Y_element
FEATURE [App::DocumentObjectGroupPython] G4_Y  # scripted group (container) (typed FeaturePython)
  Dunit = g/cm3
  Dvalue = 4.469
  Group = -> [Y_element001]
  conduct = 2
  density = 1
  expand = 3
  formula = Y
  name = G4_Y
  specific = 4
FEATURE [App::DocumentObjectGroupPython] Zr_element001  label="Zr_element : 1"  # scripted group (container) (typed FeaturePython)
  n = 1
  ref = Zr_element
FEATURE [App::DocumentObjectGroupPython] G4_Zr  # scripted group (container) (typed FeaturePython)
  Dunit = g/cm3
  Dvalue = 6.506
  Group = -> [Zr_element001]
  conduct = 2
  density = 1
  expand = 3
  formula = Zr
  name = G4_Zr
  specific = 4
FEATURE [App::DocumentObjectGroupPython] Nb_element001  label="Nb_element : 1"  # scripted group (container) (typed FeaturePython)
  n = 1
  ref = Nb_element
FEATURE [App::DocumentObjectGroupPython] G4_Nb  # scripted group (container) (typed FeaturePython)
  Dunit = g/cm3
  Dvalue = 8.57
  Group = -> [Nb_element001]
  conduct = 2
  density = 1
  expand = 3
  formula = Nb
  name = G4_Nb
  specific = 4
FEATURE [App::DocumentObjectGroupPython] Mo_element001  label="Mo_element : 1"  # scripted group (container) (typed FeaturePython)
  n = 1
  ref = Mo_element
FEATURE [App::DocumentObjectGroupPython] G4_Mo  # scripted group (container) (typed FeaturePython)
  Dunit = g/cm3
  Dvalue = 10.22
  Group = -> [Mo_element001]
  conduct = 2
  density = 1
  expand = 3
  formula = Mo
  name = G4_Mo
  specific = 4
FEATURE [App::DocumentObjectGroupPython] Tc_element001  label="Tc_element : 1"  # scripted group (container) (typed FeaturePython)
  n = 1
  ref = Tc_element
FEATURE [App::DocumentObjectGroupPython] G4_Tc  # scripted group (container) (typed FeaturePython)
  Dunit = g/cm3
  Dvalue = 11.5
  Group = -> [Tc_element001]
  conduct = 2
  density = 1
  expand = 3
  formula = Tc
  name = G4_Tc
  specific = 4
FEATURE [App::DocumentObjectGroupPython] Ru_element001  label="Ru_element : 1"  # scripted group (container) (typed FeaturePython)
  n = 1
  ref = Ru_element
FEATURE [App::DocumentObjectGroupPython] G4_Ru  # scripted group (container) (typed FeaturePython)
  Dunit = g/cm3
  Dvalue = 12.41
  Group = -> [Ru_element001]
  conduct = 2
  density = 1
  expand = 3
  formula = Ru
  name = G4_Ru
  specific = 4
FEATURE [App::DocumentObjectGroupPython] Rh_element001  label="Rh_element : 1"  # scripted group (container) (typed FeaturePython)
  n = 1
  ref = Rh_element
FEATURE [App::DocumentObjectGroupPython] G4_Rh  # scripted group (container) (typed FeaturePython)
  Dunit = g/cm3
  Dvalue = 12.41
  Group = -> [Rh_element001]
  conduct = 2
  density = 1
  expand = 3
  formula = Rh
  name = G4_Rh
  specific = 4
FEATURE [App::DocumentObjectGroupPython] Pd_element001  label="Pd_element : 1"  # scripted group (container) (typed FeaturePython)
  n = 1
  ref = Pd_element
FEATURE [App::DocumentObjectGroupPython] G4_Pd  # scripted group (container) (typed FeaturePython)
  Dunit = g/cm3
  Dvalue = 12.02
  Group = -> [Pd_element001]
  conduct = 2
  density = 1
  expand = 3
  formula = Pd
  name = G4_Pd
  specific = 4
FEATURE [App::DocumentObjectGroupPython] Ag_element006  label="Ag_element : 004"  # scripted group (container) (typed FeaturePython)
  n = 1
  ref = Ag_element
FEATURE [App::DocumentObjectGroupPython] G4_Ag  # scripted group (container) (typed FeaturePython)
  Dunit = g/cm3
  Dvalue = 10.5
  Group = -> [Ag_element006]
  conduct = 2
  density = 1
  expand = 3
  formula = Ag
  name = G4_Ag
  specific = 4
FEATURE [App::DocumentObjectGroupPython] Cd_element003  label="Cd_element : 003"  # scripted group (container) (typed FeaturePython)
  n = 1
  ref = Cd_element
FEATURE [App::DocumentObjectGroupPython] G4_Cd  # scripted group (container) (typed FeaturePython)
  Dunit = g/cm3
  Dvalue = 8.65
  Group = -> [Cd_element003]
  conduct = 2
  density = 1
  expand = 3
  formula = Cd
  name = G4_Cd
  specific = 4
FEATURE [App::DocumentObjectGroupPython] In_element001  label="In_element : 1"  # scripted group (container) (typed FeaturePython)
  n = 1
  ref = In_element
FEATURE [App::DocumentObjectGroupPython] G4_In  # scripted group (container) (typed FeaturePython)
  Dunit = g/cm3
  Dvalue = 7.31
  Group = -> [In_element001]
  conduct = 2
  density = 1
  expand = 3
  formula = In
  name = G4_In
  specific = 4
FEATURE [App::DocumentObjectGroupPython] Sn_element001  label="Sn_element : 1"  # scripted group (container) (typed FeaturePython)
  n = 1
  ref = Sn_element
FEATURE [App::DocumentObjectGroupPython] G4_Sn  # scripted group (container) (typed FeaturePython)
  Dunit = g/cm3
  Dvalue = 7.31
  Group = -> [Sn_element001]
  conduct = 2
  density = 1
  expand = 3
  formula = Sn
  name = G4_Sn
  specific = 4
FEATURE [App::DocumentObjectGroupPython] Sb_element001  label="Sb_element : 1"  # scripted group (container) (typed FeaturePython)
  n = 1
  ref = Sb_element
FEATURE [App::DocumentObjectGroupPython] G4_Sb  # scripted group (container) (typed FeaturePython)
  Dunit = g/cm3
  Dvalue = 6.691
  Group = -> [Sb_element001]
  conduct = 2
  density = 1
  expand = 3
  formula = Sb
  name = G4_Sb
  specific = 4
FEATURE [App::DocumentObjectGroupPython] Te_element002  label="Te_element : 002"  # scripted group (container) (typed FeaturePython)
  n = 1
  ref = Te_element
FEATURE [App::DocumentObjectGroupPython] G4_Te  # scripted group (container) (typed FeaturePython)
  Dunit = g/cm3
  Dvalue = 6.24
  Group = -> [Te_element002]
  conduct = 2
  density = 1
  expand = 3
  formula = Te
  name = G4_Te
  specific = 4
FEATURE [App::DocumentObjectGroupPython] I_element010  label="I_element : 006"  # scripted group (container) (typed FeaturePython)
  n = 1
  ref = I_element
FEATURE [App::DocumentObjectGroupPython] G4_I  # scripted group (container) (typed FeaturePython)
  Dunit = g/cm3
  Dvalue = 4.93
  Group = -> [I_element010]
  conduct = 2
  density = 1
  expand = 3
  formula = I
  name = G4_I
  specific = 4
FEATURE [App::DocumentObjectGroupPython] Xe_element001  label="Xe_element : 1"  # scripted group (container) (typed FeaturePython)
  n = 1
  ref = Xe_element
FEATURE [App::DocumentObjectGroupPython] G4_Xe  # scripted group (container) (typed FeaturePython)
  Dunit = g/cm3
  Dvalue = 0.00548536
  Group = -> [Xe_element001]
  conduct = 2
  density = 1
  expand = 3
  formula = Xe
  name = G4_Xe
  specific = 4
FEATURE [App::DocumentObjectGroupPython] Cs_element003  label="Cs_element : 003"  # scripted group (container) (typed FeaturePython)
  n = 1
  ref = Cs_element
FEATURE [App::DocumentObjectGroupPython] G4_Cs  # scripted group (container) (typed FeaturePython)
  Dunit = g/cm3
  Dvalue = 1.873
  Group = -> [Cs_element003]
  conduct = 2
  density = 1
  expand = 3
  formula = Cs
  name = G4_Cs
  specific = 4
FEATURE [App::DocumentObjectGroupPython] Ba_element003  label="Ba_element : 003"  # scripted group (container) (typed FeaturePython)
  n = 1
  ref = Ba_element
FEATURE [App::DocumentObjectGroupPython] G4_Ba  # scripted group (container) (typed FeaturePython)
  Dunit = g/cm3
  Dvalue = 3.5
  Group = -> [Ba_element003]
  conduct = 2
  density = 1
  expand = 3
  formula = Ba
  name = G4_Ba
  specific = 4
FEATURE [App::DocumentObjectGroupPython] La_element003  label="La_element : 003"  # scripted group (container) (typed FeaturePython)
  n = 1
  ref = La_element
FEATURE [App::DocumentObjectGroupPython] G4_La  # scripted group (container) (typed FeaturePython)
  Dunit = g/cm3
  Dvalue = 6.154
  Group = -> [La_element003]
  conduct = 2
  density = 1
  expand = 3
  formula = La
  name = G4_La
  specific = 4
FEATURE [App::DocumentObjectGroupPython] Ce_element002  label="Ce_element : 1"  # scripted group (container) (typed FeaturePython)
  n = 1
  ref = Ce_element
FEATURE [App::DocumentObjectGroupPython] G4_Ce  # scripted group (container) (typed FeaturePython)
  Dunit = g/cm3
  Dvalue = 6.657
  Group = -> [Ce_element002]
  conduct = 2
  density = 1
  expand = 3
  formula = Ce
  name = G4_Ce
  specific = 4
FEATURE [App::DocumentObjectGroupPython] Pr_element001  label="Pr_element : 1"  # scripted group (container) (typed FeaturePython)
  n = 1
  ref = Pr_element
FEATURE [App::DocumentObjectGroupPython] G4_Pr  # scripted group (container) (typed FeaturePython)
  Dunit = g/cm3
  Dvalue = 6.71
  Group = -> [Pr_element001]
  conduct = 2
  density = 1
  expand = 3
  formula = Pr
  name = G4_Pr
  specific = 4
FEATURE [App::DocumentObjectGroupPython] Nd_element001  label="Nd_element : 1"  # scripted group (container) (typed FeaturePython)
  n = 1
  ref = Nd_element
FEATURE [App::DocumentObjectGroupPython] G4_Nd  # scripted group (container) (typed FeaturePython)
  Dunit = g/cm3
  Dvalue = 6.9
  Group = -> [Nd_element001]
  conduct = 2
  density = 1
  expand = 3
  formula = Nd
  name = G4_Nd
  specific = 4
FEATURE [App::DocumentObjectGroupPython] Pm_element001  label="Pm_element : 1"  # scripted group (container) (typed FeaturePython)
  n = 1
  ref = Pm_element
FEATURE [App::DocumentObjectGroupPython] G4_Pm  # scripted group (container) (typed FeaturePython)
  Dunit = g/cm3
  Dvalue = 7.22
  Group = -> [Pm_element001]
  conduct = 2
  density = 1
  expand = 3
  formula = Pm
  name = G4_Pm
  specific = 4
FEATURE [App::DocumentObjectGroupPython] Sm_element001  label="Sm_element : 1"  # scripted group (container) (typed FeaturePython)
  n = 1
  ref = Sm_element
FEATURE [App::DocumentObjectGroupPython] G4_Sm  # scripted group (container) (typed FeaturePython)
  Dunit = g/cm3
  Dvalue = 7.46
  Group = -> [Sm_element001]
  conduct = 2
  density = 1
  expand = 3
  formula = Sm
  name = G4_Sm
  specific = 4
FEATURE [App::DocumentObjectGroupPython] Eu_element001  label="Eu_element : 1"  # scripted group (container) (typed FeaturePython)
  n = 1
  ref = Eu_element
FEATURE [App::DocumentObjectGroupPython] G4_Eu  # scripted group (container) (typed FeaturePython)
  Dunit = g/cm3
  Dvalue = 5.243
  Group = -> [Eu_element001]
  conduct = 2
  density = 1
  expand = 3
  formula = Eu
  name = G4_Eu
  specific = 4
FEATURE [App::DocumentObjectGroupPython] Gd_element002  label="Gd_element : 1"  # scripted group (container) (typed FeaturePython)
  n = 1
  ref = Gd_element
FEATURE [App::DocumentObjectGroupPython] G4_Gd  # scripted group (container) (typed FeaturePython)
  Dunit = g/cm3
  Dvalue = 7.9004
  Group = -> [Gd_element002]
  conduct = 2
  density = 1
  expand = 3
  formula = Gd
  name = G4_Gd
  specific = 4
FEATURE [App::DocumentObjectGroupPython] Tb_element001  label="Tb_element : 1"  # scripted group (container) (typed FeaturePython)
  n = 1
  ref = Tb_element
FEATURE [App::DocumentObjectGroupPython] G4_Tb  # scripted group (container) (typed FeaturePython)
  Dunit = g/cm3
  Dvalue = 8.229
  Group = -> [Tb_element001]
  conduct = 2
  density = 1
  expand = 3
  formula = Tb
  name = G4_Tb
  specific = 4
FEATURE [App::DocumentObjectGroupPython] Dy_element001  label="Dy_element : 1"  # scripted group (container) (typed FeaturePython)
  n = 1
  ref = Dy_element
FEATURE [App::DocumentObjectGroupPython] G4_Dy  # scripted group (container) (typed FeaturePython)
  Dunit = g/cm3
  Dvalue = 8.55
  Group = -> [Dy_element001]
  conduct = 2
  density = 1
  expand = 3
  formula = Dy
  name = G4_Dy
  specific = 4
FEATURE [App::DocumentObjectGroupPython] Ho_element001  label="Ho_element : 1"  # scripted group (container) (typed FeaturePython)
  n = 1
  ref = Ho_element
FEATURE [App::DocumentObjectGroupPython] G4_Ho  # scripted group (container) (typed FeaturePython)
  Dunit = g/cm3
  Dvalue = 8.795
  Group = -> [Ho_element001]
  conduct = 2
  density = 1
  expand = 3
  formula = Ho
  name = G4_Ho
  specific = 4
FEATURE [App::DocumentObjectGroupPython] Er_element001  label="Er_element : 1"  # scripted group (container) (typed FeaturePython)
  n = 1
  ref = Er_element
FEATURE [App::DocumentObjectGroupPython] G4_Er  # scripted group (container) (typed FeaturePython)
  Dunit = g/cm3
  Dvalue = 9.066
  Group = -> [Er_element001]
  conduct = 2
  density = 1
  expand = 3
  formula = Er
  name = G4_Er
  specific = 4
FEATURE [App::DocumentObjectGroupPython] Tm_element001  label="Tm_element : 1"  # scripted group (container) (typed FeaturePython)
  n = 1
  ref = Tm_element
FEATURE [App::DocumentObjectGroupPython] G4_Tm  # scripted group (container) (typed FeaturePython)
  Dunit = g/cm3
  Dvalue = 9.321
  Group = -> [Tm_element001]
  conduct = 2
  density = 1
  expand = 3
  formula = Tm
  name = G4_Tm
  specific = 4
FEATURE [App::DocumentObjectGroupPython] Yb_element001  label="Yb_element : 1"  # scripted group (container) (typed FeaturePython)
  n = 1
  ref = Yb_element
FEATURE [App::DocumentObjectGroupPython] G4_Yb  # scripted group (container) (typed FeaturePython)
  Dunit = g/cm3
  Dvalue = 6.73
  Group = -> [Yb_element001]
  conduct = 2
  density = 1
  expand = 3
  formula = Yb
  name = G4_Yb
  specific = 4
FEATURE [App::DocumentObjectGroupPython] Lu_element001  label="Lu_element : 1"  # scripted group (container) (typed FeaturePython)
  n = 1
  ref = Lu_element
FEATURE [App::DocumentObjectGroupPython] G4_Lu  # scripted group (container) (typed FeaturePython)
  Dunit = g/cm3
  Dvalue = 9.84
  Group = -> [Lu_element001]
  conduct = 2
  density = 1
  expand = 3
  formula = Lu
  name = G4_Lu
  specific = 4
FEATURE [App::DocumentObjectGroupPython] Hf_element001  label="Hf_element : 1"  # scripted group (container) (typed FeaturePython)
  n = 1
  ref = Hf_element
FEATURE [App::DocumentObjectGroupPython] G4_Hf  # scripted group (container) (typed FeaturePython)
  Dunit = g/cm3
  Dvalue = 13.31
  Group = -> [Hf_element001]
  conduct = 2
  density = 1
  expand = 3
  formula = Hf
  name = G4_Hf
  specific = 4
FEATURE [App::DocumentObjectGroupPython] Ta_element001  label="Ta_element : 1"  # scripted group (container) (typed FeaturePython)
  n = 1
  ref = Ta_element
FEATURE [App::DocumentObjectGroupPython] G4_Ta  # scripted group (container) (typed FeaturePython)
  Dunit = g/cm3
  Dvalue = 16.654
  Group = -> [Ta_element001]
  conduct = 2
  density = 1
  expand = 3
  formula = Ta
  name = G4_Ta
  specific = 4
FEATURE [App::DocumentObjectGroupPython] W_element004  label="W_element : 004"  # scripted group (container) (typed FeaturePython)
  n = 1
  ref = W_element
FEATURE [App::DocumentObjectGroupPython] G4_W  # scripted group (container) (typed FeaturePython)
  Dunit = g/cm3
  Dvalue = 19.3
  Group = -> [W_element004]
  conduct = 2
  density = 1
  expand = 3
  formula = W
  name = G4_W
  specific = 4
FEATURE [App::DocumentObjectGroupPython] Re_element001  label="Re_element : 1"  # scripted group (container) (typed FeaturePython)
  n = 1
  ref = Re_element
FEATURE [App::DocumentObjectGroupPython] G4_Re  # scripted group (container) (typed FeaturePython)
  Dunit = g/cm3
  Dvalue = 21.02
  Group = -> [Re_element001]
  conduct = 2
  density = 1
  expand = 3
  formula = Re
  name = G4_Re
  specific = 4
FEATURE [App::DocumentObjectGroupPython] Os_element001  label="Os_element : 1"  # scripted group (container) (typed FeaturePython)
  n = 1
  ref = Os_element
FEATURE [App::DocumentObjectGroupPython] G4_Os  # scripted group (container) (typed FeaturePython)
  Dunit = g/cm3
  Dvalue = 22.57
  Group = -> [Os_element001]
  conduct = 2
  density = 1
  expand = 3
  formula = Os
  name = G4_Os
  specific = 4
FEATURE [App::DocumentObjectGroupPython] Ir_element001  label="Ir_element : 1"  # scripted group (container) (typed FeaturePython)
  n = 1
  ref = Ir_element
FEATURE [App::DocumentObjectGroupPython] G4_Ir  # scripted group (container) (typed FeaturePython)
  Dunit = g/cm3
  Dvalue = 22.42
  Group = -> [Ir_element001]
  conduct = 2
  density = 1
  expand = 3
  formula = Ir
  name = G4_Ir
  specific = 4
FEATURE [App::DocumentObjectGroupPython] Pt_element001  label="Pt_element : 1"  # scripted group (container) (typed FeaturePython)
  n = 1
  ref = Pt_element
FEATURE [App::DocumentObjectGroupPython] G4_Pt  # scripted group (container) (typed FeaturePython)
  Dunit = g/cm3
  Dvalue = 21.45
  Group = -> [Pt_element001]
  conduct = 2
  density = 1
  expand = 3
  formula = Pt
  name = G4_Pt
  specific = 4
FEATURE [App::DocumentObjectGroupPython] Au_element001  label="Au_element : 1"  # scripted group (container) (typed FeaturePython)
  n = 1
  ref = Au_element
FEATURE [App::DocumentObjectGroupPython] G4_Au  # scripted group (container) (typed FeaturePython)
  Dunit = g/cm3
  Dvalue = 19.32
  Group = -> [Au_element001]
  conduct = 2
  density = 1
  expand = 3
  formula = Au
  name = G4_Au
  specific = 4
FEATURE [App::DocumentObjectGroupPython] Hg_element002  label="Hg_element : 002"  # scripted group (container) (typed FeaturePython)
  n = 1
  ref = Hg_element
FEATURE [App::DocumentObjectGroupPython] G4_Hg  # scripted group (container) (typed FeaturePython)
  Dunit = g/cm3
  Dvalue = 13.546
  Group = -> [Hg_element002]
  conduct = 2
  density = 1
  expand = 3
  formula = Hg
  name = G4_Hg
  specific = 4
FEATURE [App::DocumentObjectGroupPython] Tl_element002  label="Tl_element : 002"  # scripted group (container) (typed FeaturePython)
  n = 1
  ref = Tl_element
FEATURE [App::DocumentObjectGroupPython] G4_Tl  # scripted group (container) (typed FeaturePython)
  Dunit = g/cm3
  Dvalue = 11.72
  Group = -> [Tl_element002]
  conduct = 2
  density = 1
  expand = 3
  formula = Tl
  name = G4_Tl
  specific = 4
FEATURE [App::DocumentObjectGroupPython] Pb_element003  label="Pb_element : 1"  # scripted group (container) (typed FeaturePython)
  n = 1
  ref = Pb_element
FEATURE [App::DocumentObjectGroupPython] G4_Pb  # scripted group (container) (typed FeaturePython)
  Dunit = g/cm3
  Dvalue = 11.35
  Group = -> [Pb_element003]
  conduct = 2
  density = 1
  expand = 3
  formula = Pb
  name = G4_Pb
  specific = 4
FEATURE [App::DocumentObjectGroupPython] Bi_element002  label="Bi_element : 1"  # scripted group (container) (typed FeaturePython)
  n = 1
  ref = Bi_element
FEATURE [App::DocumentObjectGroupPython] G4_Bi  # scripted group (container) (typed FeaturePython)
  Dunit = g/cm3
  Dvalue = 9.747
  Group = -> [Bi_element002]
  conduct = 2
  density = 1
  expand = 3
  formula = Bi
  name = G4_Bi
  specific = 4
FEATURE [App::DocumentObjectGroupPython] Po_element001  label="Po_element : 1"  # scripted group (container) (typed FeaturePython)
  n = 1
  ref = Po_element
FEATURE [App::DocumentObjectGroupPython] G4_Po  # scripted group (container) (typed FeaturePython)
  Dunit = g/cm3
  Dvalue = 9.32
  Group = -> [Po_element001]
  conduct = 2
  density = 1
  expand = 3
  formula = Po
  name = G4_Po
  specific = 4
FEATURE [App::DocumentObjectGroupPython] At_element001  label="At_element : 1"  # scripted group (container) (typed FeaturePython)
  n = 1
  ref = At_element
FEATURE [App::DocumentObjectGroupPython] G4_At  # scripted group (container) (typed FeaturePython)
  Dunit = g/cm3
  Dvalue = 9.32
  Group = -> [At_element001]
  conduct = 2
  density = 1
  expand = 3
  formula = At
  name = G4_At
  specific = 4
FEATURE [App::DocumentObjectGroupPython] Rn_element001  label="Rn_element : 1"  # scripted group (container) (typed FeaturePython)
  n = 1
  ref = Rn_element
FEATURE [App::DocumentObjectGroupPython] G4_Rn  # scripted group (container) (typed FeaturePython)
  Dunit = g/cm3
  Dvalue = 0.00900662
  Group = -> [Rn_element001]
  conduct = 2
  density = 1
  expand = 3
  formula = Rn
  name = G4_Rn
  specific = 4
FEATURE [App::DocumentObjectGroupPython] Fr_element001  label="Fr_element : 1"  # scripted group (container) (typed FeaturePython)
  n = 1
  ref = Fr_element
FEATURE [App::DocumentObjectGroupPython] G4_Fr  # scripted group (container) (typed FeaturePython)
  Dunit = g/cm3
  Dvalue = 1
  Group = -> [Fr_element001]
  conduct = 2
  density = 1
  expand = 3
  formula = Fr
  name = G4_Fr
  specific = 4
FEATURE [App::DocumentObjectGroupPython] Ra_element001  label="Ra_element : 1"  # scripted group (container) (typed FeaturePython)
  n = 1
  ref = Ra_element
FEATURE [App::DocumentObjectGroupPython] G4_Ra  # scripted group (container) (typed FeaturePython)
  Dunit = g/cm3
  Dvalue = 5
  Group = -> [Ra_element001]
  conduct = 2
  density = 1
  expand = 3
  formula = Ra
  name = G4_Ra
  specific = 4
FEATURE [App::DocumentObjectGroupPython] Ac_element001  label="Ac_element : 1"  # scripted group (container) (typed FeaturePython)
  n = 1
  ref = Ac_element
FEATURE [App::DocumentObjectGroupPython] G4_Ac  # scripted group (container) (typed FeaturePython)
  Dunit = g/cm3
  Dvalue = 10.07
  Group = -> [Ac_element001]
  conduct = 2
  density = 1
  expand = 3
  formula = Ac
  name = G4_Ac
  specific = 4
FEATURE [App::DocumentObjectGroupPython] Th_element001  label="Th_element : 1"  # scripted group (container) (typed FeaturePython)
  n = 1
  ref = Th_element
FEATURE [App::DocumentObjectGroupPython] G4_Th  # scripted group (container) (typed FeaturePython)
  Dunit = g/cm3
  Dvalue = 11.72
  Group = -> [Th_element001]
  conduct = 2
  density = 1
  expand = 3
  formula = Th
  name = G4_Th
  specific = 4
FEATURE [App::DocumentObjectGroupPython] Pa_element001  label="Pa_element : 1"  # scripted group (container) (typed FeaturePython)
  n = 1
  ref = Pa_element
FEATURE [App::DocumentObjectGroupPython] G4_Pa  # scripted group (container) (typed FeaturePython)
  Dunit = g/cm3
  Dvalue = 15.37
  Group = -> [Pa_element001]
  conduct = 2
  density = 1
  expand = 3
  formula = Pa
  name = G4_Pa
  specific = 4
FEATURE [App::DocumentObjectGroupPython] U_element004  label="U_element : 004"  # scripted group (container) (typed FeaturePython)
  n = 1
  ref = U_element
FEATURE [App::DocumentObjectGroupPython] G4_U  # scripted group (container) (typed FeaturePython)
  Dunit = g/cm3
  Dvalue = 18.95
  Group = -> [U_element004]
  conduct = 2
  density = 1
  expand = 3
  formula = U
  name = G4_U
  specific = 4
FEATURE [App::DocumentObjectGroupPython] Np_element001  label="Np_element : 1"  # scripted group (container) (typed FeaturePython)
  n = 1
  ref = Np_element
FEATURE [App::DocumentObjectGroupPython] G4_Np  # scripted group (container) (typed FeaturePython)
  Dunit = g/cm3
  Dvalue = 20.25
  Group = -> [Np_element001]
  conduct = 2
  density = 1
  expand = 3
  formula = Np
  name = G4_Np
  specific = 4
FEATURE [App::DocumentObjectGroupPython] Pu_element002  label="Pu_element : 002"  # scripted group (container) (typed FeaturePython)
  n = 1
  ref = Pu_element
FEATURE [App::DocumentObjectGroupPython] G4_Pu  # scripted group (container) (typed FeaturePython)
  Dunit = g/cm3
  Dvalue = 19.84
  Group = -> [Pu_element002]
  conduct = 2
  density = 1
  expand = 3
  formula = Pu
  name = G4_Pu
  specific = 4
FEATURE [App::DocumentObjectGroupPython] Am_element001  label="Am_element : 1"  # scripted group (container) (typed FeaturePython)
  n = 1
  ref = Am_element
FEATURE [App::DocumentObjectGroupPython] G4_Am  # scripted group (container) (typed FeaturePython)
  Dunit = g/cm3
  Dvalue = 13.67
  Group = -> [Am_element001]
  conduct = 2
  density = 1
  expand = 3
  formula = Am
  name = G4_Am
  specific = 4
FEATURE [App::DocumentObjectGroupPython] Cm_element001  label="Cm_element : 1"  # scripted group (container) (typed FeaturePython)
  n = 1
  ref = Cm_element
FEATURE [App::DocumentObjectGroupPython] G4_Cm  # scripted group (container) (typed FeaturePython)
  Dunit = g/cm3
  Dvalue = 13.51
  Group = -> [Cm_element001]
  conduct = 2
  density = 1
  expand = 3
  formula = Cm
  name = G4_Cm
  specific = 4
FEATURE [App::DocumentObjectGroupPython] Bk_element001  label="Bk_element : 1"  # scripted group (container) (typed FeaturePython)
  n = 1
  ref = Bk_element
FEATURE [App::DocumentObjectGroupPython] G4_Bk  # scripted group (container) (typed FeaturePython)
  Dunit = g/cm3
  Dvalue = 14
  Group = -> [Bk_element001]
  conduct = 2
  density = 1
  expand = 3
  formula = Bk
  name = G4_Bk
  specific = 4
FEATURE [App::DocumentObjectGroupPython] Cf_element001  label="Cf_element : 1"  # scripted group (container) (typed FeaturePython)
  n = 1
  ref = Cf_element
FEATURE [App::DocumentObjectGroupPython] G4_Cf  # scripted group (container) (typed FeaturePython)
  Dunit = g/cm3
  Dvalue = 10
  Group = -> [Cf_element001]
  conduct = 2
  density = 1
  expand = 3
  formula = Cf
  name = G4_Cf
  specific = 4
FEATURE [App::DocumentObjectGroupPython] Element  # scripted group (container) (typed FeaturePython)
  Group = -> [G4_H,G4_He,G4_Li,G4_Be,G4_B,G4_C,G4_N,G4_O,G4_F,G4_Ne,G4_Na,G4_Mg,G4_Al,G4_Si,G4_P,G4_S,G4_Cl,G4_Ar,G4_K,G4_Ca,G4_Sc,G4_Ti,G4_V,G4_Cr,G4_Mn,G4_Fe,G4_Co,G4_Ni,G4_Cu,G4_Zn,G4_Ga,G4_Ge,G4_As,G4_Se,G4_Br,G4_Kr,G4_Rb,G4_Sr,G4_Y,G4_Zr,G4_Nb,G4_Mo,G4_Tc,G4_Ru,G4_Rh,G4_Pd,G4_Ag,G4_Cd,G4_In,G4_Sn,G4_Sb,G4_Te,G4_I,G4_Xe,G4_Cs,G4_Ba,G4_La,G4_Ce,G4_Pr,G4_Nd,G4_Pm,G4_Sm,G4_Eu,G4_Gd,G4_Tb,G4_Dy,G4_Ho,G4_Er,+30 more]
FEATURE [App::DocumentObjectGroupPython] H_element114  label="H_element : 063"  # scripted group (container) (typed FeaturePython)
  n = 2
  ref = H_element
FEATURE [App::DocumentObjectGroupPython] G4_lH2  # scripted group (container) (typed FeaturePython)
  Dunit = g/cm3
  Dvalue = 0.0708
  Group = -> [H_element114]
  conduct = 2
  density = 1
  expand = 3
  formula = G4_lH2
  name = G4_lH2
  specific = 4
FEATURE [App::DocumentObjectGroupPython] N_element049  label="N_element : 022"  # scripted group (container) (typed FeaturePython)
  n = 2
  ref = N_element
FEATURE [App::DocumentObjectGroupPython] G4_lN2  # scripted group (container) (typed FeaturePython)
  Dunit = g/cm3
  Dvalue = 0.807
  Group = -> [N_element049]
  conduct = 2
  density = 1
  expand = 3
  formula = G4_lN2
  name = G4_lN2
  specific = 4
FEATURE [App::DocumentObjectGroupPython] O_element106  label="O_element : 060"  # scripted group (container) (typed FeaturePython)
  n = 2
  ref = O_element
FEATURE [App::DocumentObjectGroupPython] G4_lO2  # scripted group (container) (typed FeaturePython)
  Dunit = g/cm3
  Dvalue = 1.141
  Group = -> [O_element106]
  conduct = 2
  density = 1
  expand = 3
  formula = G4_lO2
  name = G4_lO2
  specific = 4
FEATURE [App::DocumentObjectGroupPython] Ar  label="Ar : 1"  # scripted group (container) (typed FeaturePython)
  n = 1
  ref = Ar
FEATURE [App::DocumentObjectGroupPython] G4_lAr  # scripted group (container) (typed FeaturePython)
  Dunit = g/cm3
  Dvalue = 1.396
  Group = -> [Ar]
  conduct = 2
  density = 1
  expand = 3
  formula = G4_lAr
  name = G4_lAr
  specific = 4
FEATURE [App::DocumentObjectGroupPython] Br  label="Br : 1"  # scripted group (container) (typed FeaturePython)
  n = 1
  ref = Br
FEATURE [App::DocumentObjectGroupPython] G4_lBr  # scripted group (container) (typed FeaturePython)
  Dunit = g/cm3
  Dvalue = 3.1028
  Group = -> [Br]
  conduct = 2
  density = 1
  expand = 3
  formula = G4_lBr
  name = G4_lBr
  specific = 4
FEATURE [App::DocumentObjectGroupPython] Kr  label="Kr : 1"  # scripted group (container) (typed FeaturePython)
  n = 1
  ref = Kr
FEATURE [App::DocumentObjectGroupPython] G4_lKr  # scripted group (container) (typed FeaturePython)
  Dunit = g/cm3
  Dvalue = 2.418
  Group = -> [Kr]
  conduct = 2
  density = 1
  expand = 3
  formula = G4_lKr
  name = G4_lKr
  specific = 4
FEATURE [App::DocumentObjectGroupPython] Xe  label="Xe : 1"  # scripted group (container) (typed FeaturePython)
  n = 1
  ref = Xe
FEATURE [App::DocumentObjectGroupPython] G4_lXe  # scripted group (container) (typed FeaturePython)
  Dunit = g/cm3
  Dvalue = 2.953
  Group = -> [Xe]
  conduct = 2
  density = 1
  expand = 3
  formula = G4_lXe
  name = G4_lXe
  specific = 4
FEATURE [App::DocumentObjectGroupPython] O_element107  label="O_element : 061"  # scripted group (container) (typed FeaturePython)
  n = 4
  ref = O_element
FEATURE [App::DocumentObjectGroupPython] Pb_element004  label="Pb_element : 002"  # scripted group (container) (typed FeaturePython)
  n = 1
  ref = Pb_element
FEATURE [App::DocumentObjectGroupPython] W_element005  label="W_element : 005"  # scripted group (container) (typed FeaturePython)
  n = 1
  ref = W_element
FEATURE [App::DocumentObjectGroupPython] G4_PbWO4  # scripted group (container) (typed FeaturePython)
  Dunit = g/cm3
  Dvalue = 8.28
  Group = -> [O_element107,Pb_element004,W_element005]
  conduct = 2
  density = 1
  expand = 3
  formula = G4_PbWO4
  name = G4_PbWO4
  specific = 4
FEATURE [App::DocumentObjectGroupPython] alactic  label="alactic : 1"  # scripted group (container) (typed FeaturePython)
  n = 1
  ref = alactic
FEATURE [App::DocumentObjectGroupPython] G4_Galactic  # scripted group (container) (typed FeaturePython)
  Dunit = g/cm3
  Dvalue = 0
  Group = -> [alactic]
  conduct = 2
  density = 1
  expand = 3
  formula = G4_Galactic
  name = G4_Galactic
  specific = 4
FEATURE [App::DocumentObjectGroupPython] RAPHITE_POROUS  label="RAPHITE_POROUS : 1"  # scripted group (container) (typed FeaturePython)
  n = 1
  ref = RAPHITE_POROUS
FEATURE [App::DocumentObjectGroupPython] G4_GRAPHITE_POROUS  # scripted group (container) (typed FeaturePython)
  Dunit = g/cm3
  Dvalue = 1.7
  Group = -> [RAPHITE_POROUS]
  conduct = 2
  density = 1
  expand = 3
  formula = G4_GRAPHITE_POROUS
  name = G4_GRAPHITE_POROUS
  specific = 4
FEATURE [App::DocumentObjectGroupPython] H_element115  label="H_element : 0.150"  # scripted group (container) (typed FeaturePython)
  n = 0.080538
FEATURE [App::DocumentObjectGroupPython] C_element125  label="C_element : 0.600"  # scripted group (container) (typed FeaturePython)
  n = 0.599848
FEATURE [App::DocumentObjectGroupPython] O_element108  label="O_element : 0.320"  # scripted group (container) (typed FeaturePython)
  n = 0.319614
FEATURE [App::DocumentObjectGroupPython] G4_LUCITE  # scripted group (container) (typed FeaturePython)
  Dunit = g/cm3
  Dvalue = 1.19
  Group = -> [H_element115,C_element125,O_element108]
  conduct = 2
  density = 1
  expand = 3
  formula = G4_LUCITE
  name = G4_LUCITE
  specific = 4
FEATURE [App::DocumentObjectGroupPython] Cu_element002  label="Cu_element : 62"  # scripted group (container) (typed FeaturePython)
  n = 62
  ref = Cu_element
FEATURE [App::DocumentObjectGroupPython] Zn_element002  label="Zn_element : 35"  # scripted group (container) (typed FeaturePython)
  n = 35
  ref = Zn_element
FEATURE [App::DocumentObjectGroupPython] Pb_element005  label="Pb_element : 3"  # scripted group (container) (typed FeaturePython)
  n = 3
  ref = Pb_element
FEATURE [App::DocumentObjectGroupPython] G4_BRASS  # scripted group (container) (typed FeaturePython)
  Dunit = g/cm3
  Dvalue = 8.52
  Group = -> [Cu_element002,Zn_element002,Pb_element005]
  conduct = 2
  density = 1
  expand = 3
  formula = G4_BRASS
  name = G4_BRASS
  specific = 4
FEATURE [App::DocumentObjectGroupPython] Cu_element003  label="Cu_element : 89"  # scripted group (container) (typed FeaturePython)
  n = 89
  ref = Cu_element
FEATURE [App::DocumentObjectGroupPython] Zn_element003  label="Zn_element : 9"  # scripted group (container) (typed FeaturePython)
  n = 9
  ref = Zn_element
FEATURE [App::DocumentObjectGroupPython] Pb_element006  label="Pb_element : 2"  # scripted group (container) (typed FeaturePython)
  n = 2
  ref = Pb_element
FEATURE [App::DocumentObjectGroupPython] G4_BRONZE  # scripted group (container) (typed FeaturePython)
  Dunit = g/cm3
  Dvalue = 8.82
  Group = -> [Cu_element003,Zn_element003,Pb_element006]
  conduct = 2
  density = 1
  expand = 3
  formula = G4_BRONZE
  name = G4_BRONZE
  specific = 4
FEATURE [App::DocumentObjectGroupPython] Fe_element008  label="Fe_element : 74"  # scripted group (container) (typed FeaturePython)
  n = 74
  ref = Fe_element
FEATURE [App::DocumentObjectGroupPython] Cr_element002  label="Cr_element : 18"  # scripted group (container) (typed FeaturePython)
  n = 18
  ref = Cr_element
FEATURE [App::DocumentObjectGroupPython] Ni_element002  label="Ni_element : 8"  # scripted group (container) (typed FeaturePython)
  n = 8
  ref = Ni_element
FEATURE [App::DocumentObjectGroupPython] G4_STAINLESS_STEEL  label="G4_STAINLESS-STEEL"  # scripted group (container) (typed FeaturePython)
  Dunit = g/cm3
  Dvalue = 8
  Group = -> [Fe_element008,Cr_element002,Ni_element002]
  conduct = 2
  density = 1
  expand = 3
  formula = G4_STAINLESS-STEEL
  name = G4_STAINLESS-STEEL
  specific = 4
FEATURE [App::DocumentObjectGroupPython] H_element116  label="H_element : 064"  # scripted group (container) (typed FeaturePython)
  n = 18
  ref = H_element
FEATURE [App::DocumentObjectGroupPython] C_element126  label="C_element : 071"  # scripted group (container) (typed FeaturePython)
  n = 12
  ref = C_element
FEATURE [App::DocumentObjectGroupPython] O_element109  label="O_element : 062"  # scripted group (container) (typed FeaturePython)
  n = 7
  ref = O_element
FEATURE [App::DocumentObjectGroupPython] G4_CR39  # scripted group (container) (typed FeaturePython)
  Dunit = g/cm3
  Dvalue = 1.32
  Group = -> [H_element116,C_element126,O_element109]
  conduct = 2
  density = 1
  expand = 3
  formula = G4_CR39
  name = G4_CR39
  specific = 4
FEATURE [App::DocumentObjectGroupPython] H_element117  label="H_element : 38"  # scripted group (container) (typed FeaturePython)
  n = 38
  ref = H_element
FEATURE [App::DocumentObjectGroupPython] C_element127  label="C_element : 072"  # scripted group (container) (typed FeaturePython)
  n = 18
  ref = C_element
FEATURE [App::DocumentObjectGroupPython] O_element110  label="O_element : 063"  # scripted group (container) (typed FeaturePython)
  n = 1
  ref = O_element
FEATURE [App::DocumentObjectGroupPython] G4_OCTADECANOL  # scripted group (container) (typed FeaturePython)
  Dunit = g/cm3
  Dvalue = 0.812
  Group = -> [H_element117,C_element127,O_element110]
  conduct = 2
  density = 1
  expand = 3
  formula = G4_OCTADECANOL
  name = G4_OCTADECANOL
  specific = 4
FEATURE [App::DocumentObjectGroupPython] HEP  # scripted group (container) (typed FeaturePython)
  Group = -> [G4_lH2,G4_lN2,G4_lO2,G4_lAr,G4_lBr,G4_lKr,G4_lXe,G4_PbWO4,G4_Galactic,G4_GRAPHITE_POROUS,G4_LUCITE,G4_BRASS,G4_BRONZE,G4_STAINLESS_STEEL,G4_CR39,G4_OCTADECANOL]
FEATURE [App::DocumentObjectGroupPython] C_element128  label="C_element : 073"  # scripted group (container) (typed FeaturePython)
  n = 14
  ref = C_element
FEATURE [App::DocumentObjectGroupPython] H_element118  label="H_element : 065"  # scripted group (container) (typed FeaturePython)
  n = 10
  ref = H_element
FEATURE [App::DocumentObjectGroupPython] O_element111  label="O_element : 064"  # scripted group (container) (typed FeaturePython)
  n = 2
  ref = O_element
FEATURE [App::DocumentObjectGroupPython] N_element050  label="N_element : 023"  # scripted group (container) (typed FeaturePython)
  n = 2
  ref = N_element
FEATURE [App::DocumentObjectGroupPython] G4_KEVLAR  # scripted group (container) (typed FeaturePython)
  Dunit = g/cm3
  Dvalue = 1.44
  Group = -> [C_element128,H_element118,O_element111,N_element050]
  conduct = 2
  density = 1
  expand = 3
  formula = G4_KEVLAR
  name = G4_KEVLAR
  specific = 4
FEATURE [App::DocumentObjectGroupPython] C_element129  label="C_element : 074"  # scripted group (container) (typed FeaturePython)
  n = 10
  ref = C_element
FEATURE [App::DocumentObjectGroupPython] H_element119  label="H_element : 066"  # scripted group (container) (typed FeaturePython)
  n = 8
  ref = H_element
FEATURE [App::DocumentObjectGroupPython] O_element112  label="O_element : 065"  # scripted group (container) (typed FeaturePython)
  n = 4
  ref = O_element
FEATURE [App::DocumentObjectGroupPython] G4_DACRON  # scripted group (container) (typed FeaturePython)
  Dunit = g/cm3
  Dvalue = 1.4
  Group = -> [C_element129,H_element119,O_element112]
  conduct = 2
  density = 1
  expand = 3
  formula = G4_DACRON
  name = G4_DACRON
  specific = 4
FEATURE [App::DocumentObjectGroupPython] C_element130  label="C_element : 075"  # scripted group (container) (typed FeaturePython)
  n = 4
  ref = C_element
FEATURE [App::DocumentObjectGroupPython] H_element120  label="H_element : 067"  # scripted group (container) (typed FeaturePython)
  n = 5
  ref = H_element
FEATURE [App::DocumentObjectGroupPython] Cl_element030  label="Cl_element : 016"  # scripted group (container) (typed FeaturePython)
  n = 1
  ref = Cl_element
FEATURE [App::DocumentObjectGroupPython] G4_NEOPRENE  # scripted group (container) (typed FeaturePython)
  Dunit = g/cm3
  Dvalue = 1.23
  Group = -> [C_element130,H_element120,Cl_element030]
  conduct = 2
  density = 1
  expand = 3
  formula = G4_NEOPRENE
  name = G4_NEOPRENE
  specific = 4
FEATURE [App::DocumentObjectGroupPython] Space  # scripted group (container) (typed FeaturePython)
  Group = -> [G4_KEVLAR,G4_DACRON,G4_NEOPRENE]
FEATURE [App::DocumentObjectGroupPython] H_element121  label="H_element : 068"  # scripted group (container) (typed FeaturePython)
  n = 5
  ref = H_element
FEATURE [App::DocumentObjectGroupPython] C_element131  label="C_element : 076"  # scripted group (container) (typed FeaturePython)
  n = 4
  ref = C_element
FEATURE [App::DocumentObjectGroupPython] N_element051  label="N_element : 3"  # scripted group (container) (typed FeaturePython)
  n = 3
  ref = N_element
FEATURE [App::DocumentObjectGroupPython] O_element113  label="O_element : 066"  # scripted group (container) (typed FeaturePython)
  n = 1
  ref = O_element
FEATURE [App::DocumentObjectGroupPython] G4_CYTOSINE  # scripted group (container) (typed FeaturePython)
  Dunit = g/cm3
  Dvalue = 1.55
  Group = -> [H_element121,C_element131,N_element051,O_element113]
  conduct = 2
  density = 1
  expand = 3
  formula = G4_CYTOSINE
  name = G4_CYTOSINE
  specific = 4
FEATURE [App::DocumentObjectGroupPython] H_element122  label="H_element : 069"  # scripted group (container) (typed FeaturePython)
  n = 6
  ref = H_element
FEATURE [App::DocumentObjectGroupPython] C_element132  label="C_element : 077"  # scripted group (container) (typed FeaturePython)
  n = 5
  ref = C_element
FEATURE [App::DocumentObjectGroupPython] N_element052  label="N_element : 024"  # scripted group (container) (typed FeaturePython)
  n = 2
  ref = N_element
FEATURE [App::DocumentObjectGroupPython] O_element114  label="O_element : 067"  # scripted group (container) (typed FeaturePython)
  n = 2
  ref = O_element
FEATURE [App::DocumentObjectGroupPython] G4_THYMINE  # scripted group (container) (typed FeaturePython)
  Dunit = g/cm3
  Dvalue = 1.23
  Group = -> [H_element122,C_element132,N_element052,O_element114]
  conduct = 2
  density = 1
  expand = 3
  formula = G4_THYMINE
  name = G4_THYMINE
  specific = 4
FEATURE [App::DocumentObjectGroupPython] H_element123  label="H_element : 070"  # scripted group (container) (typed FeaturePython)
  n = 4
  ref = H_element
FEATURE [App::DocumentObjectGroupPython] C_element133  label="C_element : 078"  # scripted group (container) (typed FeaturePython)
  n = 4
  ref = C_element
FEATURE [App::DocumentObjectGroupPython] N_element053  label="N_element : 025"  # scripted group (container) (typed FeaturePython)
  n = 2
  ref = N_element
FEATURE [App::DocumentObjectGroupPython] O_element115  label="O_element : 068"  # scripted group (container) (typed FeaturePython)
  n = 2
  ref = O_element
FEATURE [App::DocumentObjectGroupPython] G4_URACIL  # scripted group (container) (typed FeaturePython)
  Dunit = g/cm3
  Dvalue = 1.32
  Group = -> [H_element123,C_element133,N_element053,O_element115]
  conduct = 2
  density = 1
  expand = 3
  formula = G4_URACIL
  name = G4_URACIL
  specific = 4
FEATURE [App::DocumentObjectGroupPython] H_element124  label="H_element : 071"  # scripted group (container) (typed FeaturePython)
  n = 4
  ref = H_element
FEATURE [App::DocumentObjectGroupPython] C_element134  label="C_element : 079"  # scripted group (container) (typed FeaturePython)
  n = 5
  ref = C_element
FEATURE [App::DocumentObjectGroupPython] N_element054  label="N_element : 026"  # scripted group (container) (typed FeaturePython)
  n = 5
  ref = N_element
FEATURE [App::DocumentObjectGroupPython] G4_DNA_ADENINE  # scripted group (container) (typed FeaturePython)
  Dunit = g/cm3
  Dvalue = 1
  Group = -> [H_element124,C_element134,N_element054]
  conduct = 2
  density = 1
  expand = 3
  formula = G4_DNA_ADENINE
  name = G4_DNA_ADENINE
  specific = 4
FEATURE [App::DocumentObjectGroupPython] H_element125  label="H_element : 072"  # scripted group (container) (typed FeaturePython)
  n = 4
  ref = H_element
FEATURE [App::DocumentObjectGroupPython] C_element135  label="C_element : 080"  # scripted group (container) (typed FeaturePython)
  n = 5
  ref = C_element
FEATURE [App::DocumentObjectGroupPython] N_element055  label="N_element : 027"  # scripted group (container) (typed FeaturePython)
  n = 5
  ref = N_element
FEATURE [App::DocumentObjectGroupPython] O_element116  label="O_element : 069"  # scripted group (container) (typed FeaturePython)
  n = 1
  ref = O_element
FEATURE [App::DocumentObjectGroupPython] G4_DNA_GUANINE  # scripted group (container) (typed FeaturePython)
  Dunit = g/cm3
  Dvalue = 1
  Group = -> [H_element125,C_element135,N_element055,O_element116]
  conduct = 2
  density = 1
  expand = 3
  formula = G4_DNA_GUANINE
  name = G4_DNA_GUANINE
  specific = 4
FEATURE [App::DocumentObjectGroupPython] H_element126  label="H_element : 073"  # scripted group (container) (typed FeaturePython)
  n = 4
  ref = H_element
FEATURE [App::DocumentObjectGroupPython] C_element136  label="C_element : 081"  # scripted group (container) (typed FeaturePython)
  n = 4
  ref = C_element
FEATURE [App::DocumentObjectGroupPython] N_element056  label="N_element : 028"  # scripted group (container) (typed FeaturePython)
  n = 3
  ref = N_element
FEATURE [App::DocumentObjectGroupPython] O_element117  label="O_element : 070"  # scripted group (container) (typed FeaturePython)
  n = 1
  ref = O_element
FEATURE [App::DocumentObjectGroupPython] G4_DNA_CYTOSINE  # scripted group (container) (typed FeaturePython)
  Dunit = g/cm3
  Dvalue = 1
  Group = -> [H_element126,C_element136,N_element056,O_element117]
  conduct = 2
  density = 1
  expand = 3
  formula = G4_DNA_CYTOSINE
  name = G4_DNA_CYTOSINE
  specific = 4
FEATURE [App::DocumentObjectGroupPython] H_element127  label="H_element : 074"  # scripted group (container) (typed FeaturePython)
  n = 5
  ref = H_element
FEATURE [App::DocumentObjectGroupPython] C_element137  label="C_element : 082"  # scripted group (container) (typed FeaturePython)
  n = 5
  ref = C_element
FEATURE [App::DocumentObjectGroupPython] N_element057  label="N_element : 029"  # scripted group (container) (typed FeaturePython)
  n = 2
  ref = N_element
FEATURE [App::DocumentObjectGroupPython] O_element118  label="O_element : 071"  # scripted group (container) (typed FeaturePython)
  n = 2
  ref = O_element
FEATURE [App::DocumentObjectGroupPython] G4_DNA_THYMINE  # scripted group (container) (typed FeaturePython)
  Dunit = g/cm3
  Dvalue = 1
  Group = -> [H_element127,C_element137,N_element057,O_element118]
  conduct = 2
  density = 1
  expand = 3
  formula = G4_DNA_THYMINE
  name = G4_DNA_THYMINE
  specific = 4
FEATURE [App::DocumentObjectGroupPython] H_element128  label="H_element : 075"  # scripted group (container) (typed FeaturePython)
  n = 3
  ref = H_element
FEATURE [App::DocumentObjectGroupPython] C_element138  label="C_element : 083"  # scripted group (container) (typed FeaturePython)
  n = 4
  ref = C_element
FEATURE [App::DocumentObjectGroupPython] N_element058  label="N_element : 030"  # scripted group (container) (typed FeaturePython)
  n = 2
  ref = N_element
FEATURE [App::DocumentObjectGroupPython] O_element119  label="O_element : 072"  # scripted group (container) (typed FeaturePython)
  n = 2
  ref = O_element
FEATURE [App::DocumentObjectGroupPython] G4_DNA_URACIL  # scripted group (container) (typed FeaturePython)
  Dunit = g/cm3
  Dvalue = 1
  Group = -> [H_element128,C_element138,N_element058,O_element119]
  conduct = 2
  density = 1
  expand = 3
  formula = G4_DNA_URACIL
  name = G4_DNA_URACIL
  specific = 4
FEATURE [App::DocumentObjectGroupPython] H_element129  label="H_element : 076"  # scripted group (container) (typed FeaturePython)
  n = 10
  ref = H_element
FEATURE [App::DocumentObjectGroupPython] C_element139  label="C_element : 084"  # scripted group (container) (typed FeaturePython)
  n = 10
  ref = C_element
FEATURE [App::DocumentObjectGroupPython] N_element059  label="N_element : 031"  # scripted group (container) (typed FeaturePython)
  n = 5
  ref = N_element
FEATURE [App::DocumentObjectGroupPython] O_element120  label="O_element : 073"  # scripted group (container) (typed FeaturePython)
  n = 4
  ref = O_element
FEATURE [App::DocumentObjectGroupPython] G4_DNA_ADENOSINE  # scripted group (container) (typed FeaturePython)
  Dunit = g/cm3
  Dvalue = 1
  Group = -> [H_element129,C_element139,N_element059,O_element120]
  conduct = 2
  density = 1
  expand = 3
  formula = G4_DNA_ADENOSINE
  name = G4_DNA_ADENOSINE
  specific = 4
FEATURE [App::DocumentObjectGroupPython] H_element130  label="H_element : 077"  # scripted group (container) (typed FeaturePython)
  n = 10
  ref = H_element
FEATURE [App::DocumentObjectGroupPython] C_element140  label="C_element : 085"  # scripted group (container) (typed FeaturePython)
  n = 10
  ref = C_element
FEATURE [App::DocumentObjectGroupPython] N_element060  label="N_element : 032"  # scripted group (container) (typed FeaturePython)
  n = 5
  ref = N_element
FEATURE [App::DocumentObjectGroupPython] O_element121  label="O_element : 074"  # scripted group (container) (typed FeaturePython)
  n = 5
  ref = O_element
FEATURE [App::DocumentObjectGroupPython] G4_DNA_GUANOSINE  # scripted group (container) (typed FeaturePython)
  Dunit = g/cm3
  Dvalue = 1
  Group = -> [H_element130,C_element140,N_element060,O_element121]
  conduct = 2
  density = 1
  expand = 3
  formula = G4_DNA_GUANOSINE
  name = G4_DNA_GUANOSINE
  specific = 4
FEATURE [App::DocumentObjectGroupPython] H_element131  label="H_element : 078"  # scripted group (container) (typed FeaturePython)
  n = 10
  ref = H_element
FEATURE [App::DocumentObjectGroupPython] C_element141  label="C_element : 086"  # scripted group (container) (typed FeaturePython)
  n = 9
  ref = C_element
FEATURE [App::DocumentObjectGroupPython] N_element061  label="N_element : 033"  # scripted group (container) (typed FeaturePython)
  n = 3
  ref = N_element
FEATURE [App::DocumentObjectGroupPython] O_element122  label="O_element : 075"  # scripted group (container) (typed FeaturePython)
  n = 5
  ref = O_element
FEATURE [App::DocumentObjectGroupPython] G4_DNA_CYTIDINE  # scripted group (container) (typed FeaturePython)
  Dunit = g/cm3
  Dvalue = 1
  Group = -> [H_element131,C_element141,N_element061,O_element122]
  conduct = 2
  density = 1
  expand = 3
  formula = G4_DNA_CYTIDINE
  name = G4_DNA_CYTIDINE
  specific = 4
FEATURE [App::DocumentObjectGroupPython] H_element132  label="H_element : 079"  # scripted group (container) (typed FeaturePython)
  n = 9
  ref = H_element
FEATURE [App::DocumentObjectGroupPython] C_element142  label="C_element : 087"  # scripted group (container) (typed FeaturePython)
  n = 9
  ref = C_element
FEATURE [App::DocumentObjectGroupPython] N_element062  label="N_element : 034"  # scripted group (container) (typed FeaturePython)
  n = 2
  ref = N_element
FEATURE [App::DocumentObjectGroupPython] O_element123  label="O_element : 076"  # scripted group (container) (typed FeaturePython)
  n = 6
  ref = O_element
FEATURE [App::DocumentObjectGroupPython] G4_DNA_URIDINE  # scripted group (container) (typed FeaturePython)
  Dunit = g/cm3
  Dvalue = 1
  Group = -> [H_element132,C_element142,N_element062,O_element123]
  conduct = 2
  density = 1
  expand = 3
  formula = G4_DNA_URIDINE
  name = G4_DNA_URIDINE
  specific = 4
FEATURE [App::DocumentObjectGroupPython] H_element133  label="H_element : 080"  # scripted group (container) (typed FeaturePython)
  n = 11
  ref = H_element
FEATURE [App::DocumentObjectGroupPython] C_element143  label="C_element : 088"  # scripted group (container) (typed FeaturePython)
  n = 10
  ref = C_element
FEATURE [App::DocumentObjectGroupPython] N_element063  label="N_element : 035"  # scripted group (container) (typed FeaturePython)
  n = 2
  ref = N_element
FEATURE [App::DocumentObjectGroupPython] O_element124  label="O_element : 077"  # scripted group (container) (typed FeaturePython)
  n = 6
  ref = O_element
FEATURE [App::DocumentObjectGroupPython] G4_DNA_METHYLURIDINE  # scripted group (container) (typed FeaturePython)
  Dunit = g/cm3
  Dvalue = 1
  Group = -> [H_element133,C_element143,N_element063,O_element124]
  conduct = 2
  density = 1
  expand = 3
  formula = G4_DNA_METHYLURIDINE
  name = G4_DNA_METHYLURIDINE
  specific = 4
FEATURE [App::DocumentObjectGroupPython] P_element014  label="P_element : 003"  # scripted group (container) (typed FeaturePython)
  n = 1
  ref = P_element
FEATURE [App::DocumentObjectGroupPython] O_element125  label="O_element : 078"  # scripted group (container) (typed FeaturePython)
  n = 3
  ref = O_element
FEATURE [App::DocumentObjectGroupPython] G4_DNA_MONOPHOSPHATE  # scripted group (container) (typed FeaturePython)
  Dunit = g/cm3
  Dvalue = 1
  Group = -> [P_element014,O_element125]
  conduct = 2
  density = 1
  expand = 3
  formula = G4_DNA_MONOPHOSPHATE
  name = G4_DNA_MONOPHOSPHATE
  specific = 4
FEATURE [App::DocumentObjectGroupPython] H_element134  label="H_element : 081"  # scripted group (container) (typed FeaturePython)
  n = 10
  ref = H_element
FEATURE [App::DocumentObjectGroupPython] C_element144  label="C_element : 089"  # scripted group (container) (typed FeaturePython)
  n = 10
  ref = C_element
FEATURE [App::DocumentObjectGroupPython] N_element064  label="N_element : 036"  # scripted group (container) (typed FeaturePython)
  n = 5
  ref = N_element
FEATURE [App::DocumentObjectGroupPython] O_element126  label="O_element : 079"  # scripted group (container) (typed FeaturePython)
  n = 7
  ref = O_element
FEATURE [App::DocumentObjectGroupPython] P_element015  label="P_element : 004"  # scripted group (container) (typed FeaturePython)
  n = 1
  ref = P_element
FEATURE [App::DocumentObjectGroupPython] G4_DNA_A  # scripted group (container) (typed FeaturePython)
  Dunit = g/cm3
  Dvalue = 1
  Group = -> [H_element134,C_element144,N_element064,O_element126,P_element015]
  conduct = 2
  density = 1
  expand = 3
  formula = G4_DNA_A
  name = G4_DNA_A
  specific = 4
FEATURE [App::DocumentObjectGroupPython] H_element135  label="H_element : 082"  # scripted group (container) (typed FeaturePython)
  n = 10
  ref = H_element
FEATURE [App::DocumentObjectGroupPython] C_element145  label="C_element : 090"  # scripted group (container) (typed FeaturePython)
  n = 10
  ref = C_element
FEATURE [App::DocumentObjectGroupPython] N_element065  label="N_element : 037"  # scripted group (container) (typed FeaturePython)
  n = 5
  ref = N_element
FEATURE [App::DocumentObjectGroupPython] O_element127  label="O_element : 8"  # scripted group (container) (typed FeaturePython)
  n = 8
  ref = O_element
FEATURE [App::DocumentObjectGroupPython] P_element016  label="P_element : 005"  # scripted group (container) (typed FeaturePython)
  n = 1
  ref = P_element
FEATURE [App::DocumentObjectGroupPython] G4_DNA_G  # scripted group (container) (typed FeaturePython)
  Dunit = g/cm3
  Dvalue = 1
  Group = -> [H_element135,C_element145,N_element065,O_element127,P_element016]
  conduct = 2
  density = 1
  expand = 3
  formula = G4_DNA_G
  name = G4_DNA_G
  specific = 4
FEATURE [App::DocumentObjectGroupPython] H_element136  label="H_element : 083"  # scripted group (container) (typed FeaturePython)
  n = 10
  ref = H_element
FEATURE [App::DocumentObjectGroupPython] C_element146  label="C_element : 091"  # scripted group (container) (typed FeaturePython)
  n = 9
  ref = C_element
FEATURE [App::DocumentObjectGroupPython] N_element066  label="N_element : 038"  # scripted group (container) (typed FeaturePython)
  n = 3
  ref = N_element
FEATURE [App::DocumentObjectGroupPython] O_element128  label="O_element : 080"  # scripted group (container) (typed FeaturePython)
  n = 8
  ref = O_element
FEATURE [App::DocumentObjectGroupPython] P_element017  label="P_element : 006"  # scripted group (container) (typed FeaturePython)
  n = 1
  ref = P_element
FEATURE [App::DocumentObjectGroupPython] G4_DNA_C  # scripted group (container) (typed FeaturePython)
  Dunit = g/cm3
  Dvalue = 1
  Group = -> [H_element136,C_element146,N_element066,O_element128,P_element017]
  conduct = 2
  density = 1
  expand = 3
  formula = G4_DNA_C
  name = G4_DNA_C
  specific = 4
FEATURE [App::DocumentObjectGroupPython] H_element137  label="H_element : 084"  # scripted group (container) (typed FeaturePython)
  n = 9
  ref = H_element
FEATURE [App::DocumentObjectGroupPython] C_element147  label="C_element : 092"  # scripted group (container) (typed FeaturePython)
  n = 9
  ref = C_element
FEATURE [App::DocumentObjectGroupPython] N_element067  label="N_element : 039"  # scripted group (container) (typed FeaturePython)
  n = 2
  ref = N_element
FEATURE [App::DocumentObjectGroupPython] O_element129  label="O_element : 9"  # scripted group (container) (typed FeaturePython)
  n = 9
  ref = O_element
FEATURE [App::DocumentObjectGroupPython] P_element018  label="P_element : 007"  # scripted group (container) (typed FeaturePython)
  n = 1
  ref = P_element
FEATURE [App::DocumentObjectGroupPython] G4_DNA_U  # scripted group (container) (typed FeaturePython)
  Dunit = g/cm3
  Dvalue = 1
  Group = -> [H_element137,C_element147,N_element067,O_element129,P_element018]
  conduct = 2
  density = 1
  expand = 3
  formula = G4_DNA_U
  name = G4_DNA_U
  specific = 4
FEATURE [App::DocumentObjectGroupPython] H_element138  label="H_element : 085"  # scripted group (container) (typed FeaturePython)
  n = 11
  ref = H_element
FEATURE [App::DocumentObjectGroupPython] C_element148  label="C_element : 093"  # scripted group (container) (typed FeaturePython)
  n = 10
  ref = C_element
FEATURE [App::DocumentObjectGroupPython] N_element068  label="N_element : 040"  # scripted group (container) (typed FeaturePython)
  n = 2
  ref = N_element
FEATURE [App::DocumentObjectGroupPython] O_element130  label="O_element : 081"  # scripted group (container) (typed FeaturePython)
  n = 9
  ref = O_element
FEATURE [App::DocumentObjectGroupPython] P_element019  label="P_element : 008"  # scripted group (container) (typed FeaturePython)
  n = 1
  ref = P_element
FEATURE [App::DocumentObjectGroupPython] G4_DNA_MU  # scripted group (container) (typed FeaturePython)
  Dunit = g/cm3
  Dvalue = 1
  Group = -> [H_element138,C_element148,N_element068,O_element130,P_element019]
  conduct = 2
  density = 1
  expand = 3
  formula = G4_DNA_MU
  name = G4_DNA_MU
  specific = 4
FEATURE [App::DocumentObjectGroupPython] BioChemical  # scripted group (container) (typed FeaturePython)
  Group = -> [G4_CYTOSINE,G4_THYMINE,G4_URACIL,G4_DNA_ADENINE,G4_DNA_GUANINE,G4_DNA_CYTOSINE,G4_DNA_THYMINE,G4_DNA_URACIL,G4_DNA_ADENOSINE,G4_DNA_GUANOSINE,G4_DNA_CYTIDINE,G4_DNA_URIDINE,G4_DNA_METHYLURIDINE,G4_DNA_MONOPHOSPHATE,G4_DNA_A,G4_DNA_G,G4_DNA_C,G4_DNA_U,G4_DNA_MU]
FEATURE [App::DocumentObjectGroupPython] G4Materials  # scripted group (container) (typed FeaturePython)
  Group = -> [NIST,Element,HEP,Space,BioChemical]
  version = 1
FEATURE [App::DocumentObjectGroupPython] Geant4  # scripted group (container) (typed FeaturePython)
  Group = -> [G4Isotopes,G4Elements,G4Materials]
FEATURE [App::DocumentObjectGroupPython] Materials  # scripted group (container) (typed FeaturePython)
  Group = -> [Geant4]
FEATURE [Part::FeaturePython] GDMLBox_WorldBox  # WARN: FeaturePython — macro-defined, semantics opaque (R4)
  lunit = 2
  material = 7
  x = 400
  y = 400
  z = 400
FEATURE [Part::FeaturePython] GDMLBox_Box  # WARN: FeaturePython — macro-defined, semantics opaque (R4)
  lunit = 2
  material = 0
  x = 10
  y = 10
  z = 10
FEATURE [Part::FeaturePython] GDMLTube_Tube  # WARN: FeaturePython — macro-defined, semantics opaque (R4)
  aunit = 1
  deltaphi = 360
  lunit = 2
  material = 0
  rmax = 3
  rmin = 0
  startphi = 0
  z = 20
FEATURE [Part::Cut] Cut
  Base = -> GDMLBox_Box
  Placement = pos=(15,0,0) rot=(0,0,1;0rad)
  Tool = -> GDMLTube_Tube
  material = 5
FEATURE [Part::FeaturePython] Array  # Draft array (typed FeaturePython)
  Angle = 360
  ArrayType = 1
  Axis = (0,0,1)
  Base = -> Cut
  Center = (0,0,0)
  Fuse = false
  IntervalAxis = (0,0,0)
  IntervalX = (50,0,0)
  IntervalY = (0,50,0)
  IntervalZ = (0,0,50)
  NumberCircles = 3
  NumberPolar = 5
  NumberX = 2
  NumberY = 2
  NumberZ = 1
  RadialDistance = 50
  Symmetry = 1
  TangentialDistance = 25
FEATURE [Part::FeaturePython] Array001  # Draft array (typed FeaturePython)
  Angle = 360
  ArrayType = 0
  Axis = (0,0,1)
  Base = -> Array
  Center = (0,0,0)
  Fuse = false
  IntervalAxis = (0,0,0)
  IntervalX = (100,0,0)
  IntervalY = (0,100,0)
  IntervalZ = (0,0,100)
  NumberCircles = 3
  NumberPolar = 5
  NumberX = 2
  NumberY = 2
  NumberZ = 1
  RadialDistance = 50
  Symmetry = 1
  TangentialDistance = 25
  material = 193
FEATURE [App::Part] Bool_Cut  label="Arrays_of_solids"
  Group = -> [GDMLBox_Box,GDMLTube_Tube,Cut,Array,Array001]
  Origin = -> Origin003
FEATURE [App::Part] worldVOL
  Group = -> [GDMLBox_WorldBox,Bool_Cut]
  Origin = -> Origin
